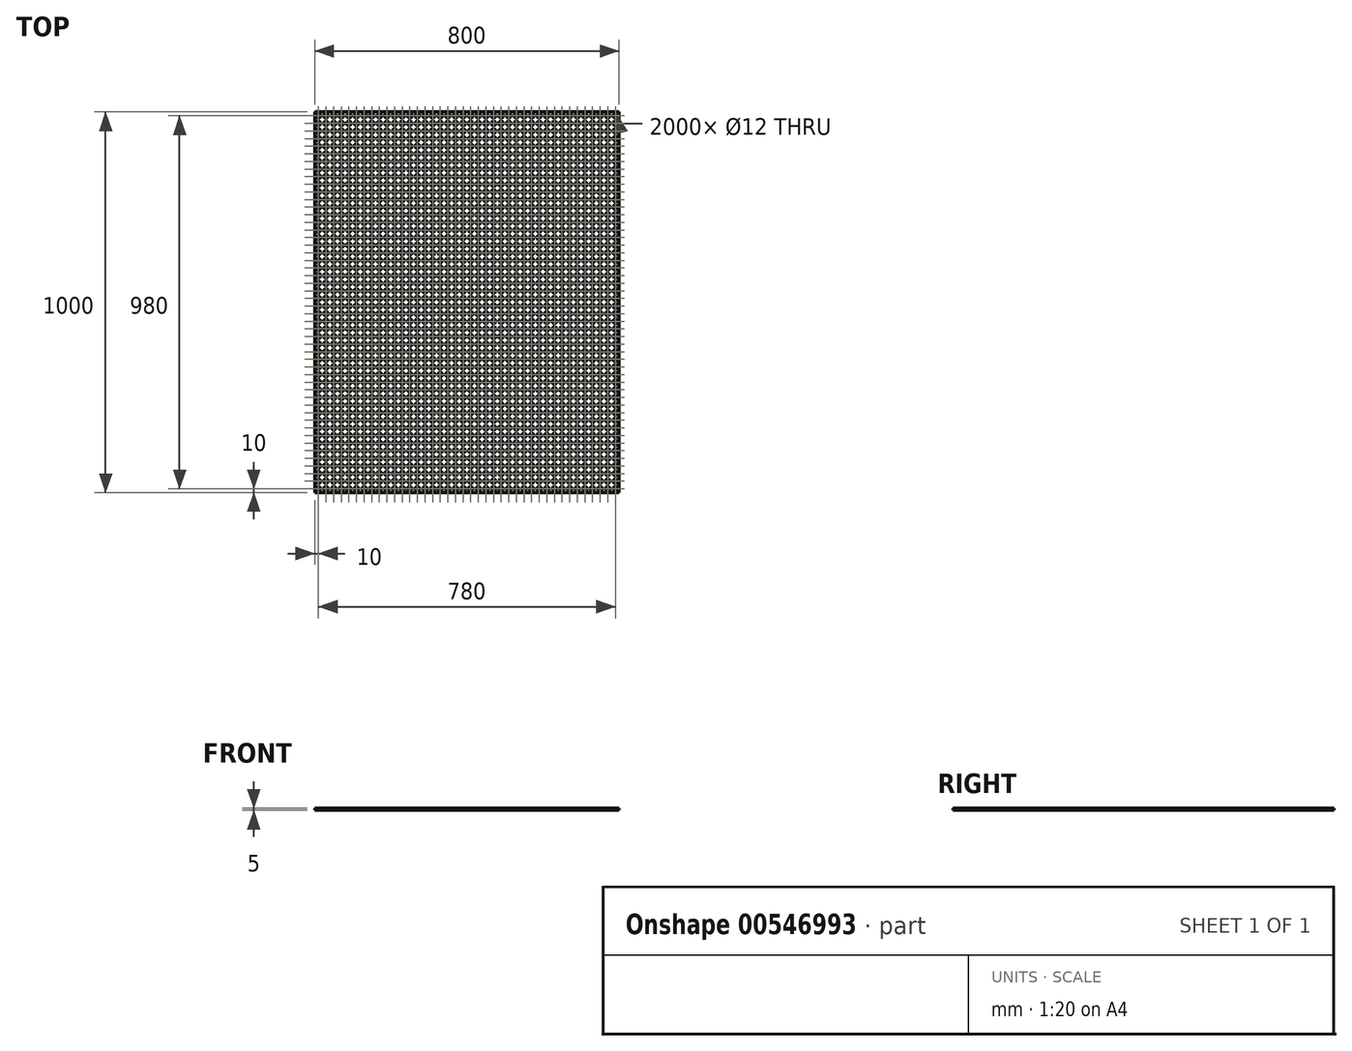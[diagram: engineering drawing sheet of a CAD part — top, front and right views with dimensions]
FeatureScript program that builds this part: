
annotation { "Feature Type Name" : "Feature", "Feature Type Description" : "" }
export const myFeature = defineFeature(function(context is Context, id is Id, definition is map)
    precondition{}
    {
        {
            var Q0;
            Q0=qCreatedBy(makeId("Top.planeOp"),FACE);
            var sketch = newSketch(context, id + "F0", { "sketchPlane" : qUnion([Q0])});
            skLineSegment(sketch, "E0.bottom", {"start": v(-409.32, 246.6) * mm, "end": v(390.68, 246.6) * mm});
            skLineSegment(sketch, "E0.top", {"start": v(-409.32, -753.4) * mm, "end": v(390.68, -753.4) * mm});
            skLineSegment(sketch, "E0.left", {"start": v(-409.32, 246.6) * mm, "end": v(-409.32, -753.4) * mm});
            skLineSegment(sketch, "E0.right", {"start": v(390.68, 246.6) * mm, "end": v(390.68, -753.4) * mm});
            skSolve(sketch);
        }
        {
            var Q0;
            Q0=makeQuery(id+"F0.imprint","IMPRINT",FACE,{"disambiguationData":[TD([[makeQuery(id+"F0.imprint","IMPRINT",EDGE,{"derivedFrom":sQuery(id+"F0.wireOp",EDGE,"E0.bottom")}),-1.0]])]});
            extrude(context, id + "F1", {"entities" : qUnion([Q0]), "depth" : 5 * mm, "offsetDistance" : 25 * mm});
        }
        {
            var Q0;
            Q0=makeQuery(id+"F1.opExtrude","CAP_FACE",FACE,{"disambiguationData":[OSD([sQuery(id+"F0.wireOp",EDGE,"E0.bottom"),sQuery(id+"F0.wireOp",EDGE,"E0.top"),sQuery(id+"F0.wireOp",EDGE,"E0.left"),sQuery(id+"F0.wireOp",EDGE,"E0.right")])],"isStart":false});
            var sketch = newSketch(context, id + "F2", { "sketchPlane" : qUnion([Q0])});
            skCircle(sketch, "E1", {"center": v(-399.32, 236.6) * mm, "radius": 6 * mm});
            skCircle(sketch, "E2.0.1.0", {"center": v(-399.32, 216.6) * mm, "radius": 6 * mm});
            skCircle(sketch, "E2.0.2.0", {"center": v(-399.32, 196.6) * mm, "radius": 6 * mm});
            skCircle(sketch, "E2.0.3.0", {"center": v(-399.32, 176.6) * mm, "radius": 6 * mm});
            skCircle(sketch, "E2.0.4.0", {"center": v(-399.32, 156.6) * mm, "radius": 6 * mm});
            skCircle(sketch, "E2.0.5.0", {"center": v(-399.32, 136.6) * mm, "radius": 6 * mm});
            skCircle(sketch, "E2.0.6.0", {"center": v(-399.32, 116.6) * mm, "radius": 6 * mm});
            skCircle(sketch, "E2.0.7.0", {"center": v(-399.32, 96.6) * mm, "radius": 6 * mm});
            skCircle(sketch, "E2.0.8.0", {"center": v(-399.32, 76.6) * mm, "radius": 6 * mm});
            skCircle(sketch, "E2.0.9.0", {"center": v(-399.32, 56.6) * mm, "radius": 6 * mm});
            skCircle(sketch, "E2.0.10.0", {"center": v(-399.32, 36.6) * mm, "radius": 6 * mm});
            skCircle(sketch, "E2.0.11.0", {"center": v(-399.32, 16.6) * mm, "radius": 6 * mm});
            skCircle(sketch, "E2.0.12.0", {"center": v(-399.32, -3.4) * mm, "radius": 6 * mm});
            skCircle(sketch, "E2.0.13.0", {"center": v(-399.32, -23.4) * mm, "radius": 6 * mm});
            skCircle(sketch, "E2.0.14.0", {"center": v(-399.32, -43.4) * mm, "radius": 6 * mm});
            skCircle(sketch, "E2.0.15.0", {"center": v(-399.32, -63.4) * mm, "radius": 6 * mm});
            skCircle(sketch, "E2.0.16.0", {"center": v(-399.32, -83.4) * mm, "radius": 6 * mm});
            skCircle(sketch, "E2.0.17.0", {"center": v(-399.32, -103.4) * mm, "radius": 6 * mm});
            skCircle(sketch, "E2.0.18.0", {"center": v(-399.32, -123.4) * mm, "radius": 6 * mm});
            skCircle(sketch, "E2.0.19.0", {"center": v(-399.32, -143.4) * mm, "radius": 6 * mm});
            skCircle(sketch, "E2.0.20.0", {"center": v(-399.32, -163.4) * mm, "radius": 6 * mm});
            skCircle(sketch, "E2.0.21.0", {"center": v(-399.32, -183.4) * mm, "radius": 6 * mm});
            skCircle(sketch, "E2.0.22.0", {"center": v(-399.32, -203.4) * mm, "radius": 6 * mm});
            skCircle(sketch, "E2.0.23.0", {"center": v(-399.32, -223.4) * mm, "radius": 6 * mm});
            skCircle(sketch, "E2.0.24.0", {"center": v(-399.32, -243.4) * mm, "radius": 6 * mm});
            skCircle(sketch, "E2.0.25.0", {"center": v(-399.32, -263.4) * mm, "radius": 6 * mm});
            skCircle(sketch, "E2.0.26.0", {"center": v(-399.32, -283.4) * mm, "radius": 6 * mm});
            skCircle(sketch, "E2.0.27.0", {"center": v(-399.32, -303.4) * mm, "radius": 6 * mm});
            skCircle(sketch, "E2.0.28.0", {"center": v(-399.32, -323.4) * mm, "radius": 6 * mm});
            skCircle(sketch, "E2.0.29.0", {"center": v(-399.32, -343.4) * mm, "radius": 6 * mm});
            skCircle(sketch, "E2.0.30.0", {"center": v(-399.32, -363.4) * mm, "radius": 6 * mm});
            skCircle(sketch, "E2.0.31.0", {"center": v(-399.32, -383.4) * mm, "radius": 6 * mm});
            skCircle(sketch, "E2.0.32.0", {"center": v(-399.32, -403.4) * mm, "radius": 6 * mm});
            skCircle(sketch, "E2.0.33.0", {"center": v(-399.32, -423.4) * mm, "radius": 6 * mm});
            skCircle(sketch, "E2.0.34.0", {"center": v(-399.32, -443.4) * mm, "radius": 6 * mm});
            skCircle(sketch, "E2.0.35.0", {"center": v(-399.32, -463.4) * mm, "radius": 6 * mm});
            skCircle(sketch, "E2.0.36.0", {"center": v(-399.32, -483.4) * mm, "radius": 6 * mm});
            skCircle(sketch, "E2.0.37.0", {"center": v(-399.32, -503.4) * mm, "radius": 6 * mm});
            skCircle(sketch, "E2.0.38.0", {"center": v(-399.32, -523.4) * mm, "radius": 6 * mm});
            skCircle(sketch, "E2.0.39.0", {"center": v(-399.32, -543.4) * mm, "radius": 6 * mm});
            skCircle(sketch, "E2.0.40.0", {"center": v(-399.32, -563.4) * mm, "radius": 6 * mm});
            skCircle(sketch, "E2.0.41.0", {"center": v(-399.32, -583.4) * mm, "radius": 6 * mm});
            skCircle(sketch, "E2.0.42.0", {"center": v(-399.32, -603.4) * mm, "radius": 6 * mm});
            skCircle(sketch, "E2.0.43.0", {"center": v(-399.32, -623.4) * mm, "radius": 6 * mm});
            skCircle(sketch, "E2.0.44.0", {"center": v(-399.32, -643.4) * mm, "radius": 6 * mm});
            skCircle(sketch, "E2.0.45.0", {"center": v(-399.32, -663.4) * mm, "radius": 6 * mm});
            skCircle(sketch, "E2.0.46.0", {"center": v(-399.32, -683.4) * mm, "radius": 6 * mm});
            skCircle(sketch, "E2.0.47.0", {"center": v(-399.32, -703.4) * mm, "radius": 6 * mm});
            skCircle(sketch, "E2.0.48.0", {"center": v(-399.32, -723.4) * mm, "radius": 6 * mm});
            skCircle(sketch, "E2.0.49.0", {"center": v(-399.32, -743.4) * mm, "radius": 6 * mm});
            skCircle(sketch, "E2.1.0.0", {"center": v(-379.32, 236.6) * mm, "radius": 6 * mm});
            skCircle(sketch, "E2.1.1.0", {"center": v(-379.32, 216.6) * mm, "radius": 6 * mm});
            skCircle(sketch, "E2.1.2.0", {"center": v(-379.32, 196.6) * mm, "radius": 6 * mm});
            skCircle(sketch, "E2.1.3.0", {"center": v(-379.32, 176.6) * mm, "radius": 6 * mm});
            skCircle(sketch, "E2.1.4.0", {"center": v(-379.32, 156.6) * mm, "radius": 6 * mm});
            skCircle(sketch, "E2.1.5.0", {"center": v(-379.32, 136.6) * mm, "radius": 6 * mm});
            skCircle(sketch, "E2.1.6.0", {"center": v(-379.32, 116.6) * mm, "radius": 6 * mm});
            skCircle(sketch, "E2.1.7.0", {"center": v(-379.32, 96.6) * mm, "radius": 6 * mm});
            skCircle(sketch, "E2.1.8.0", {"center": v(-379.32, 76.6) * mm, "radius": 6 * mm});
            skCircle(sketch, "E2.1.9.0", {"center": v(-379.32, 56.6) * mm, "radius": 6 * mm});
            skCircle(sketch, "E2.1.10.0", {"center": v(-379.32, 36.6) * mm, "radius": 6 * mm});
            skCircle(sketch, "E2.1.11.0", {"center": v(-379.32, 16.6) * mm, "radius": 6 * mm});
            skCircle(sketch, "E2.1.12.0", {"center": v(-379.32, -3.4) * mm, "radius": 6 * mm});
            skCircle(sketch, "E2.1.13.0", {"center": v(-379.32, -23.4) * mm, "radius": 6 * mm});
            skCircle(sketch, "E2.1.14.0", {"center": v(-379.32, -43.4) * mm, "radius": 6 * mm});
            skCircle(sketch, "E2.1.15.0", {"center": v(-379.32, -63.4) * mm, "radius": 6 * mm});
            skCircle(sketch, "E2.1.16.0", {"center": v(-379.32, -83.4) * mm, "radius": 6 * mm});
            skCircle(sketch, "E2.1.17.0", {"center": v(-379.32, -103.4) * mm, "radius": 6 * mm});
            skCircle(sketch, "E2.1.18.0", {"center": v(-379.32, -123.4) * mm, "radius": 6 * mm});
            skCircle(sketch, "E2.1.19.0", {"center": v(-379.32, -143.4) * mm, "radius": 6 * mm});
            skCircle(sketch, "E2.1.20.0", {"center": v(-379.32, -163.4) * mm, "radius": 6 * mm});
            skCircle(sketch, "E2.1.21.0", {"center": v(-379.32, -183.4) * mm, "radius": 6 * mm});
            skCircle(sketch, "E2.1.22.0", {"center": v(-379.32, -203.4) * mm, "radius": 6 * mm});
            skCircle(sketch, "E2.1.23.0", {"center": v(-379.32, -223.4) * mm, "radius": 6 * mm});
            skCircle(sketch, "E2.1.24.0", {"center": v(-379.32, -243.4) * mm, "radius": 6 * mm});
            skCircle(sketch, "E2.1.25.0", {"center": v(-379.32, -263.4) * mm, "radius": 6 * mm});
            skCircle(sketch, "E2.1.26.0", {"center": v(-379.32, -283.4) * mm, "radius": 6 * mm});
            skCircle(sketch, "E2.1.27.0", {"center": v(-379.32, -303.4) * mm, "radius": 6 * mm});
            skCircle(sketch, "E2.1.28.0", {"center": v(-379.32, -323.4) * mm, "radius": 6 * mm});
            skCircle(sketch, "E2.1.29.0", {"center": v(-379.32, -343.4) * mm, "radius": 6 * mm});
            skCircle(sketch, "E2.1.30.0", {"center": v(-379.32, -363.4) * mm, "radius": 6 * mm});
            skCircle(sketch, "E2.1.31.0", {"center": v(-379.32, -383.4) * mm, "radius": 6 * mm});
            skCircle(sketch, "E2.1.32.0", {"center": v(-379.32, -403.4) * mm, "radius": 6 * mm});
            skCircle(sketch, "E2.1.33.0", {"center": v(-379.32, -423.4) * mm, "radius": 6 * mm});
            skCircle(sketch, "E2.1.34.0", {"center": v(-379.32, -443.4) * mm, "radius": 6 * mm});
            skCircle(sketch, "E2.1.35.0", {"center": v(-379.32, -463.4) * mm, "radius": 6 * mm});
            skCircle(sketch, "E2.1.36.0", {"center": v(-379.32, -483.4) * mm, "radius": 6 * mm});
            skCircle(sketch, "E2.1.37.0", {"center": v(-379.32, -503.4) * mm, "radius": 6 * mm});
            skCircle(sketch, "E2.1.38.0", {"center": v(-379.32, -523.4) * mm, "radius": 6 * mm});
            skCircle(sketch, "E2.1.39.0", {"center": v(-379.32, -543.4) * mm, "radius": 6 * mm});
            skCircle(sketch, "E2.1.40.0", {"center": v(-379.32, -563.4) * mm, "radius": 6 * mm});
            skCircle(sketch, "E2.1.41.0", {"center": v(-379.32, -583.4) * mm, "radius": 6 * mm});
            skCircle(sketch, "E2.1.42.0", {"center": v(-379.32, -603.4) * mm, "radius": 6 * mm});
            skCircle(sketch, "E2.1.43.0", {"center": v(-379.32, -623.4) * mm, "radius": 6 * mm});
            skCircle(sketch, "E2.1.44.0", {"center": v(-379.32, -643.4) * mm, "radius": 6 * mm});
            skCircle(sketch, "E2.1.45.0", {"center": v(-379.32, -663.4) * mm, "radius": 6 * mm});
            skCircle(sketch, "E2.1.46.0", {"center": v(-379.32, -683.4) * mm, "radius": 6 * mm});
            skCircle(sketch, "E2.1.47.0", {"center": v(-379.32, -703.4) * mm, "radius": 6 * mm});
            skCircle(sketch, "E2.1.48.0", {"center": v(-379.32, -723.4) * mm, "radius": 6 * mm});
            skCircle(sketch, "E2.1.49.0", {"center": v(-379.32, -743.4) * mm, "radius": 6 * mm});
            skCircle(sketch, "E2.2.0.0", {"center": v(-359.32, 236.6) * mm, "radius": 6 * mm});
            skCircle(sketch, "E2.2.1.0", {"center": v(-359.32, 216.6) * mm, "radius": 6 * mm});
            skCircle(sketch, "E2.2.2.0", {"center": v(-359.32, 196.6) * mm, "radius": 6 * mm});
            skCircle(sketch, "E2.2.3.0", {"center": v(-359.32, 176.6) * mm, "radius": 6 * mm});
            skCircle(sketch, "E2.2.4.0", {"center": v(-359.32, 156.6) * mm, "radius": 6 * mm});
            skCircle(sketch, "E2.2.5.0", {"center": v(-359.32, 136.6) * mm, "radius": 6 * mm});
            skCircle(sketch, "E2.2.6.0", {"center": v(-359.32, 116.6) * mm, "radius": 6 * mm});
            skCircle(sketch, "E2.2.7.0", {"center": v(-359.32, 96.6) * mm, "radius": 6 * mm});
            skCircle(sketch, "E2.2.8.0", {"center": v(-359.32, 76.6) * mm, "radius": 6 * mm});
            skCircle(sketch, "E2.2.9.0", {"center": v(-359.32, 56.6) * mm, "radius": 6 * mm});
            skCircle(sketch, "E2.2.10.0", {"center": v(-359.32, 36.6) * mm, "radius": 6 * mm});
            skCircle(sketch, "E2.2.11.0", {"center": v(-359.32, 16.6) * mm, "radius": 6 * mm});
            skCircle(sketch, "E2.2.12.0", {"center": v(-359.32, -3.4) * mm, "radius": 6 * mm});
            skCircle(sketch, "E2.2.13.0", {"center": v(-359.32, -23.4) * mm, "radius": 6 * mm});
            skCircle(sketch, "E2.2.14.0", {"center": v(-359.32, -43.4) * mm, "radius": 6 * mm});
            skCircle(sketch, "E2.2.15.0", {"center": v(-359.32, -63.4) * mm, "radius": 6 * mm});
            skCircle(sketch, "E2.2.16.0", {"center": v(-359.32, -83.4) * mm, "radius": 6 * mm});
            skCircle(sketch, "E2.2.17.0", {"center": v(-359.32, -103.4) * mm, "radius": 6 * mm});
            skCircle(sketch, "E2.2.18.0", {"center": v(-359.32, -123.4) * mm, "radius": 6 * mm});
            skCircle(sketch, "E2.2.19.0", {"center": v(-359.32, -143.4) * mm, "radius": 6 * mm});
            skCircle(sketch, "E2.2.20.0", {"center": v(-359.32, -163.4) * mm, "radius": 6 * mm});
            skCircle(sketch, "E2.2.21.0", {"center": v(-359.32, -183.4) * mm, "radius": 6 * mm});
            skCircle(sketch, "E2.2.22.0", {"center": v(-359.32, -203.4) * mm, "radius": 6 * mm});
            skCircle(sketch, "E2.2.23.0", {"center": v(-359.32, -223.4) * mm, "radius": 6 * mm});
            skCircle(sketch, "E2.2.24.0", {"center": v(-359.32, -243.4) * mm, "radius": 6 * mm});
            skCircle(sketch, "E2.2.25.0", {"center": v(-359.32, -263.4) * mm, "radius": 6 * mm});
            skCircle(sketch, "E2.2.26.0", {"center": v(-359.32, -283.4) * mm, "radius": 6 * mm});
            skCircle(sketch, "E2.2.27.0", {"center": v(-359.32, -303.4) * mm, "radius": 6 * mm});
            skCircle(sketch, "E2.2.28.0", {"center": v(-359.32, -323.4) * mm, "radius": 6 * mm});
            skCircle(sketch, "E2.2.29.0", {"center": v(-359.32, -343.4) * mm, "radius": 6 * mm});
            skCircle(sketch, "E2.2.30.0", {"center": v(-359.32, -363.4) * mm, "radius": 6 * mm});
            skCircle(sketch, "E2.2.31.0", {"center": v(-359.32, -383.4) * mm, "radius": 6 * mm});
            skCircle(sketch, "E2.2.32.0", {"center": v(-359.32, -403.4) * mm, "radius": 6 * mm});
            skCircle(sketch, "E2.2.33.0", {"center": v(-359.32, -423.4) * mm, "radius": 6 * mm});
            skCircle(sketch, "E2.2.34.0", {"center": v(-359.32, -443.4) * mm, "radius": 6 * mm});
            skCircle(sketch, "E2.2.35.0", {"center": v(-359.32, -463.4) * mm, "radius": 6 * mm});
            skCircle(sketch, "E2.2.36.0", {"center": v(-359.32, -483.4) * mm, "radius": 6 * mm});
            skCircle(sketch, "E2.2.37.0", {"center": v(-359.32, -503.4) * mm, "radius": 6 * mm});
            skCircle(sketch, "E2.2.38.0", {"center": v(-359.32, -523.4) * mm, "radius": 6 * mm});
            skCircle(sketch, "E2.2.39.0", {"center": v(-359.32, -543.4) * mm, "radius": 6 * mm});
            skCircle(sketch, "E2.2.40.0", {"center": v(-359.32, -563.4) * mm, "radius": 6 * mm});
            skCircle(sketch, "E2.2.41.0", {"center": v(-359.32, -583.4) * mm, "radius": 6 * mm});
            skCircle(sketch, "E2.2.42.0", {"center": v(-359.32, -603.4) * mm, "radius": 6 * mm});
            skCircle(sketch, "E2.2.43.0", {"center": v(-359.32, -623.4) * mm, "radius": 6 * mm});
            skCircle(sketch, "E2.2.44.0", {"center": v(-359.32, -643.4) * mm, "radius": 6 * mm});
            skCircle(sketch, "E2.2.45.0", {"center": v(-359.32, -663.4) * mm, "radius": 6 * mm});
            skCircle(sketch, "E2.2.46.0", {"center": v(-359.32, -683.4) * mm, "radius": 6 * mm});
            skCircle(sketch, "E2.2.47.0", {"center": v(-359.32, -703.4) * mm, "radius": 6 * mm});
            skCircle(sketch, "E2.2.48.0", {"center": v(-359.32, -723.4) * mm, "radius": 6 * mm});
            skCircle(sketch, "E2.2.49.0", {"center": v(-359.32, -743.4) * mm, "radius": 6 * mm});
            skCircle(sketch, "E2.3.0.0", {"center": v(-339.32, 236.6) * mm, "radius": 6 * mm});
            skCircle(sketch, "E2.3.1.0", {"center": v(-339.32, 216.6) * mm, "radius": 6 * mm});
            skCircle(sketch, "E2.3.2.0", {"center": v(-339.32, 196.6) * mm, "radius": 6 * mm});
            skCircle(sketch, "E2.3.3.0", {"center": v(-339.32, 176.6) * mm, "radius": 6 * mm});
            skCircle(sketch, "E2.3.4.0", {"center": v(-339.32, 156.6) * mm, "radius": 6 * mm});
            skCircle(sketch, "E2.3.5.0", {"center": v(-339.32, 136.6) * mm, "radius": 6 * mm});
            skCircle(sketch, "E2.3.6.0", {"center": v(-339.32, 116.6) * mm, "radius": 6 * mm});
            skCircle(sketch, "E2.3.7.0", {"center": v(-339.32, 96.6) * mm, "radius": 6 * mm});
            skCircle(sketch, "E2.3.8.0", {"center": v(-339.32, 76.6) * mm, "radius": 6 * mm});
            skCircle(sketch, "E2.3.9.0", {"center": v(-339.32, 56.6) * mm, "radius": 6 * mm});
            skCircle(sketch, "E2.3.10.0", {"center": v(-339.32, 36.6) * mm, "radius": 6 * mm});
            skCircle(sketch, "E2.3.11.0", {"center": v(-339.32, 16.6) * mm, "radius": 6 * mm});
            skCircle(sketch, "E2.3.12.0", {"center": v(-339.32, -3.4) * mm, "radius": 6 * mm});
            skCircle(sketch, "E2.3.13.0", {"center": v(-339.32, -23.4) * mm, "radius": 6 * mm});
            skCircle(sketch, "E2.3.14.0", {"center": v(-339.32, -43.4) * mm, "radius": 6 * mm});
            skCircle(sketch, "E2.3.15.0", {"center": v(-339.32, -63.4) * mm, "radius": 6 * mm});
            skCircle(sketch, "E2.3.16.0", {"center": v(-339.32, -83.4) * mm, "radius": 6 * mm});
            skCircle(sketch, "E2.3.17.0", {"center": v(-339.32, -103.4) * mm, "radius": 6 * mm});
            skCircle(sketch, "E2.3.18.0", {"center": v(-339.32, -123.4) * mm, "radius": 6 * mm});
            skCircle(sketch, "E2.3.19.0", {"center": v(-339.32, -143.4) * mm, "radius": 6 * mm});
            skCircle(sketch, "E2.3.20.0", {"center": v(-339.32, -163.4) * mm, "radius": 6 * mm});
            skCircle(sketch, "E2.3.21.0", {"center": v(-339.32, -183.4) * mm, "radius": 6 * mm});
            skCircle(sketch, "E2.3.22.0", {"center": v(-339.32, -203.4) * mm, "radius": 6 * mm});
            skCircle(sketch, "E2.3.23.0", {"center": v(-339.32, -223.4) * mm, "radius": 6 * mm});
            skCircle(sketch, "E2.3.24.0", {"center": v(-339.32, -243.4) * mm, "radius": 6 * mm});
            skCircle(sketch, "E2.3.25.0", {"center": v(-339.32, -263.4) * mm, "radius": 6 * mm});
            skCircle(sketch, "E2.3.26.0", {"center": v(-339.32, -283.4) * mm, "radius": 6 * mm});
            skCircle(sketch, "E2.3.27.0", {"center": v(-339.32, -303.4) * mm, "radius": 6 * mm});
            skCircle(sketch, "E2.3.28.0", {"center": v(-339.32, -323.4) * mm, "radius": 6 * mm});
            skCircle(sketch, "E2.3.29.0", {"center": v(-339.32, -343.4) * mm, "radius": 6 * mm});
            skCircle(sketch, "E2.3.30.0", {"center": v(-339.32, -363.4) * mm, "radius": 6 * mm});
            skCircle(sketch, "E2.3.31.0", {"center": v(-339.32, -383.4) * mm, "radius": 6 * mm});
            skCircle(sketch, "E2.3.32.0", {"center": v(-339.32, -403.4) * mm, "radius": 6 * mm});
            skCircle(sketch, "E2.3.33.0", {"center": v(-339.32, -423.4) * mm, "radius": 6 * mm});
            skCircle(sketch, "E2.3.34.0", {"center": v(-339.32, -443.4) * mm, "radius": 6 * mm});
            skCircle(sketch, "E2.3.35.0", {"center": v(-339.32, -463.4) * mm, "radius": 6 * mm});
            skCircle(sketch, "E2.3.36.0", {"center": v(-339.32, -483.4) * mm, "radius": 6 * mm});
            skCircle(sketch, "E2.3.37.0", {"center": v(-339.32, -503.4) * mm, "radius": 6 * mm});
            skCircle(sketch, "E2.3.38.0", {"center": v(-339.32, -523.4) * mm, "radius": 6 * mm});
            skCircle(sketch, "E2.3.39.0", {"center": v(-339.32, -543.4) * mm, "radius": 6 * mm});
            skCircle(sketch, "E2.3.40.0", {"center": v(-339.32, -563.4) * mm, "radius": 6 * mm});
            skCircle(sketch, "E2.3.41.0", {"center": v(-339.32, -583.4) * mm, "radius": 6 * mm});
            skCircle(sketch, "E2.3.42.0", {"center": v(-339.32, -603.4) * mm, "radius": 6 * mm});
            skCircle(sketch, "E2.3.43.0", {"center": v(-339.32, -623.4) * mm, "radius": 6 * mm});
            skCircle(sketch, "E2.3.44.0", {"center": v(-339.32, -643.4) * mm, "radius": 6 * mm});
            skCircle(sketch, "E2.3.45.0", {"center": v(-339.32, -663.4) * mm, "radius": 6 * mm});
            skCircle(sketch, "E2.3.46.0", {"center": v(-339.32, -683.4) * mm, "radius": 6 * mm});
            skCircle(sketch, "E2.3.47.0", {"center": v(-339.32, -703.4) * mm, "radius": 6 * mm});
            skCircle(sketch, "E2.3.48.0", {"center": v(-339.32, -723.4) * mm, "radius": 6 * mm});
            skCircle(sketch, "E2.3.49.0", {"center": v(-339.32, -743.4) * mm, "radius": 6 * mm});
            skCircle(sketch, "E2.4.0.0", {"center": v(-319.32, 236.6) * mm, "radius": 6 * mm});
            skCircle(sketch, "E2.4.1.0", {"center": v(-319.32, 216.6) * mm, "radius": 6 * mm});
            skCircle(sketch, "E2.4.2.0", {"center": v(-319.32, 196.6) * mm, "radius": 6 * mm});
            skCircle(sketch, "E2.4.3.0", {"center": v(-319.32, 176.6) * mm, "radius": 6 * mm});
            skCircle(sketch, "E2.4.4.0", {"center": v(-319.32, 156.6) * mm, "radius": 6 * mm});
            skCircle(sketch, "E2.4.5.0", {"center": v(-319.32, 136.6) * mm, "radius": 6 * mm});
            skCircle(sketch, "E2.4.6.0", {"center": v(-319.32, 116.6) * mm, "radius": 6 * mm});
            skCircle(sketch, "E2.4.7.0", {"center": v(-319.32, 96.6) * mm, "radius": 6 * mm});
            skCircle(sketch, "E2.4.8.0", {"center": v(-319.32, 76.6) * mm, "radius": 6 * mm});
            skCircle(sketch, "E2.4.9.0", {"center": v(-319.32, 56.6) * mm, "radius": 6 * mm});
            skCircle(sketch, "E2.4.10.0", {"center": v(-319.32, 36.6) * mm, "radius": 6 * mm});
            skCircle(sketch, "E2.4.11.0", {"center": v(-319.32, 16.6) * mm, "radius": 6 * mm});
            skCircle(sketch, "E2.4.12.0", {"center": v(-319.32, -3.4) * mm, "radius": 6 * mm});
            skCircle(sketch, "E2.4.13.0", {"center": v(-319.32, -23.4) * mm, "radius": 6 * mm});
            skCircle(sketch, "E2.4.14.0", {"center": v(-319.32, -43.4) * mm, "radius": 6 * mm});
            skCircle(sketch, "E2.4.15.0", {"center": v(-319.32, -63.4) * mm, "radius": 6 * mm});
            skCircle(sketch, "E2.4.16.0", {"center": v(-319.32, -83.4) * mm, "radius": 6 * mm});
            skCircle(sketch, "E2.4.17.0", {"center": v(-319.32, -103.4) * mm, "radius": 6 * mm});
            skCircle(sketch, "E2.4.18.0", {"center": v(-319.32, -123.4) * mm, "radius": 6 * mm});
            skCircle(sketch, "E2.4.19.0", {"center": v(-319.32, -143.4) * mm, "radius": 6 * mm});
            skCircle(sketch, "E2.4.20.0", {"center": v(-319.32, -163.4) * mm, "radius": 6 * mm});
            skCircle(sketch, "E2.4.21.0", {"center": v(-319.32, -183.4) * mm, "radius": 6 * mm});
            skCircle(sketch, "E2.4.22.0", {"center": v(-319.32, -203.4) * mm, "radius": 6 * mm});
            skCircle(sketch, "E2.4.23.0", {"center": v(-319.32, -223.4) * mm, "radius": 6 * mm});
            skCircle(sketch, "E2.4.24.0", {"center": v(-319.32, -243.4) * mm, "radius": 6 * mm});
            skCircle(sketch, "E2.4.25.0", {"center": v(-319.32, -263.4) * mm, "radius": 6 * mm});
            skCircle(sketch, "E2.4.26.0", {"center": v(-319.32, -283.4) * mm, "radius": 6 * mm});
            skCircle(sketch, "E2.4.27.0", {"center": v(-319.32, -303.4) * mm, "radius": 6 * mm});
            skCircle(sketch, "E2.4.28.0", {"center": v(-319.32, -323.4) * mm, "radius": 6 * mm});
            skCircle(sketch, "E2.4.29.0", {"center": v(-319.32, -343.4) * mm, "radius": 6 * mm});
            skCircle(sketch, "E2.4.30.0", {"center": v(-319.32, -363.4) * mm, "radius": 6 * mm});
            skCircle(sketch, "E2.4.31.0", {"center": v(-319.32, -383.4) * mm, "radius": 6 * mm});
            skCircle(sketch, "E2.4.32.0", {"center": v(-319.32, -403.4) * mm, "radius": 6 * mm});
            skCircle(sketch, "E2.4.33.0", {"center": v(-319.32, -423.4) * mm, "radius": 6 * mm});
            skCircle(sketch, "E2.4.34.0", {"center": v(-319.32, -443.4) * mm, "radius": 6 * mm});
            skCircle(sketch, "E2.4.35.0", {"center": v(-319.32, -463.4) * mm, "radius": 6 * mm});
            skCircle(sketch, "E2.4.36.0", {"center": v(-319.32, -483.4) * mm, "radius": 6 * mm});
            skCircle(sketch, "E2.4.37.0", {"center": v(-319.32, -503.4) * mm, "radius": 6 * mm});
            skCircle(sketch, "E2.4.38.0", {"center": v(-319.32, -523.4) * mm, "radius": 6 * mm});
            skCircle(sketch, "E2.4.39.0", {"center": v(-319.32, -543.4) * mm, "radius": 6 * mm});
            skCircle(sketch, "E2.4.40.0", {"center": v(-319.32, -563.4) * mm, "radius": 6 * mm});
            skCircle(sketch, "E2.4.41.0", {"center": v(-319.32, -583.4) * mm, "radius": 6 * mm});
            skCircle(sketch, "E2.4.42.0", {"center": v(-319.32, -603.4) * mm, "radius": 6 * mm});
            skCircle(sketch, "E2.4.43.0", {"center": v(-319.32, -623.4) * mm, "radius": 6 * mm});
            skCircle(sketch, "E2.4.44.0", {"center": v(-319.32, -643.4) * mm, "radius": 6 * mm});
            skCircle(sketch, "E2.4.45.0", {"center": v(-319.32, -663.4) * mm, "radius": 6 * mm});
            skCircle(sketch, "E2.4.46.0", {"center": v(-319.32, -683.4) * mm, "radius": 6 * mm});
            skCircle(sketch, "E2.4.47.0", {"center": v(-319.32, -703.4) * mm, "radius": 6 * mm});
            skCircle(sketch, "E2.4.48.0", {"center": v(-319.32, -723.4) * mm, "radius": 6 * mm});
            skCircle(sketch, "E2.4.49.0", {"center": v(-319.32, -743.4) * mm, "radius": 6 * mm});
            skCircle(sketch, "E2.5.0.0", {"center": v(-299.32, 236.6) * mm, "radius": 6 * mm});
            skCircle(sketch, "E2.5.1.0", {"center": v(-299.32, 216.6) * mm, "radius": 6 * mm});
            skCircle(sketch, "E2.5.2.0", {"center": v(-299.32, 196.6) * mm, "radius": 6 * mm});
            skCircle(sketch, "E2.5.3.0", {"center": v(-299.32, 176.6) * mm, "radius": 6 * mm});
            skCircle(sketch, "E2.5.4.0", {"center": v(-299.32, 156.6) * mm, "radius": 6 * mm});
            skCircle(sketch, "E2.5.5.0", {"center": v(-299.32, 136.6) * mm, "radius": 6 * mm});
            skCircle(sketch, "E2.5.6.0", {"center": v(-299.32, 116.6) * mm, "radius": 6 * mm});
            skCircle(sketch, "E2.5.7.0", {"center": v(-299.32, 96.6) * mm, "radius": 6 * mm});
            skCircle(sketch, "E2.5.8.0", {"center": v(-299.32, 76.6) * mm, "radius": 6 * mm});
            skCircle(sketch, "E2.5.9.0", {"center": v(-299.32, 56.6) * mm, "radius": 6 * mm});
            skCircle(sketch, "E2.5.10.0", {"center": v(-299.32, 36.6) * mm, "radius": 6 * mm});
            skCircle(sketch, "E2.5.11.0", {"center": v(-299.32, 16.6) * mm, "radius": 6 * mm});
            skCircle(sketch, "E2.5.12.0", {"center": v(-299.32, -3.4) * mm, "radius": 6 * mm});
            skCircle(sketch, "E2.5.13.0", {"center": v(-299.32, -23.4) * mm, "radius": 6 * mm});
            skCircle(sketch, "E2.5.14.0", {"center": v(-299.32, -43.4) * mm, "radius": 6 * mm});
            skCircle(sketch, "E2.5.15.0", {"center": v(-299.32, -63.4) * mm, "radius": 6 * mm});
            skCircle(sketch, "E2.5.16.0", {"center": v(-299.32, -83.4) * mm, "radius": 6 * mm});
            skCircle(sketch, "E2.5.17.0", {"center": v(-299.32, -103.4) * mm, "radius": 6 * mm});
            skCircle(sketch, "E2.5.18.0", {"center": v(-299.32, -123.4) * mm, "radius": 6 * mm});
            skCircle(sketch, "E2.5.19.0", {"center": v(-299.32, -143.4) * mm, "radius": 6 * mm});
            skCircle(sketch, "E2.5.20.0", {"center": v(-299.32, -163.4) * mm, "radius": 6 * mm});
            skCircle(sketch, "E2.5.21.0", {"center": v(-299.32, -183.4) * mm, "radius": 6 * mm});
            skCircle(sketch, "E2.5.22.0", {"center": v(-299.32, -203.4) * mm, "radius": 6 * mm});
            skCircle(sketch, "E2.5.23.0", {"center": v(-299.32, -223.4) * mm, "radius": 6 * mm});
            skCircle(sketch, "E2.5.24.0", {"center": v(-299.32, -243.4) * mm, "radius": 6 * mm});
            skCircle(sketch, "E2.5.25.0", {"center": v(-299.32, -263.4) * mm, "radius": 6 * mm});
            skCircle(sketch, "E2.5.26.0", {"center": v(-299.32, -283.4) * mm, "radius": 6 * mm});
            skCircle(sketch, "E2.5.27.0", {"center": v(-299.32, -303.4) * mm, "radius": 6 * mm});
            skCircle(sketch, "E2.5.28.0", {"center": v(-299.32, -323.4) * mm, "radius": 6 * mm});
            skCircle(sketch, "E2.5.29.0", {"center": v(-299.32, -343.4) * mm, "radius": 6 * mm});
            skCircle(sketch, "E2.5.30.0", {"center": v(-299.32, -363.4) * mm, "radius": 6 * mm});
            skCircle(sketch, "E2.5.31.0", {"center": v(-299.32, -383.4) * mm, "radius": 6 * mm});
            skCircle(sketch, "E2.5.32.0", {"center": v(-299.32, -403.4) * mm, "radius": 6 * mm});
            skCircle(sketch, "E2.5.33.0", {"center": v(-299.32, -423.4) * mm, "radius": 6 * mm});
            skCircle(sketch, "E2.5.34.0", {"center": v(-299.32, -443.4) * mm, "radius": 6 * mm});
            skCircle(sketch, "E2.5.35.0", {"center": v(-299.32, -463.4) * mm, "radius": 6 * mm});
            skCircle(sketch, "E2.5.36.0", {"center": v(-299.32, -483.4) * mm, "radius": 6 * mm});
            skCircle(sketch, "E2.5.37.0", {"center": v(-299.32, -503.4) * mm, "radius": 6 * mm});
            skCircle(sketch, "E2.5.38.0", {"center": v(-299.32, -523.4) * mm, "radius": 6 * mm});
            skCircle(sketch, "E2.5.39.0", {"center": v(-299.32, -543.4) * mm, "radius": 6 * mm});
            skCircle(sketch, "E2.5.40.0", {"center": v(-299.32, -563.4) * mm, "radius": 6 * mm});
            skCircle(sketch, "E2.5.41.0", {"center": v(-299.32, -583.4) * mm, "radius": 6 * mm});
            skCircle(sketch, "E2.5.42.0", {"center": v(-299.32, -603.4) * mm, "radius": 6 * mm});
            skCircle(sketch, "E2.5.43.0", {"center": v(-299.32, -623.4) * mm, "radius": 6 * mm});
            skCircle(sketch, "E2.5.44.0", {"center": v(-299.32, -643.4) * mm, "radius": 6 * mm});
            skCircle(sketch, "E2.5.45.0", {"center": v(-299.32, -663.4) * mm, "radius": 6 * mm});
            skCircle(sketch, "E2.5.46.0", {"center": v(-299.32, -683.4) * mm, "radius": 6 * mm});
            skCircle(sketch, "E2.5.47.0", {"center": v(-299.32, -703.4) * mm, "radius": 6 * mm});
            skCircle(sketch, "E2.5.48.0", {"center": v(-299.32, -723.4) * mm, "radius": 6 * mm});
            skCircle(sketch, "E2.5.49.0", {"center": v(-299.32, -743.4) * mm, "radius": 6 * mm});
            skCircle(sketch, "E2.6.0.0", {"center": v(-279.32, 236.6) * mm, "radius": 6 * mm});
            skCircle(sketch, "E2.6.1.0", {"center": v(-279.32, 216.6) * mm, "radius": 6 * mm});
            skCircle(sketch, "E2.6.2.0", {"center": v(-279.32, 196.6) * mm, "radius": 6 * mm});
            skCircle(sketch, "E2.6.3.0", {"center": v(-279.32, 176.6) * mm, "radius": 6 * mm});
            skCircle(sketch, "E2.6.4.0", {"center": v(-279.32, 156.6) * mm, "radius": 6 * mm});
            skCircle(sketch, "E2.6.5.0", {"center": v(-279.32, 136.6) * mm, "radius": 6 * mm});
            skCircle(sketch, "E2.6.6.0", {"center": v(-279.32, 116.6) * mm, "radius": 6 * mm});
            skCircle(sketch, "E2.6.7.0", {"center": v(-279.32, 96.6) * mm, "radius": 6 * mm});
            skCircle(sketch, "E2.6.8.0", {"center": v(-279.32, 76.6) * mm, "radius": 6 * mm});
            skCircle(sketch, "E2.6.9.0", {"center": v(-279.32, 56.6) * mm, "radius": 6 * mm});
            skCircle(sketch, "E2.6.10.0", {"center": v(-279.32, 36.6) * mm, "radius": 6 * mm});
            skCircle(sketch, "E2.6.11.0", {"center": v(-279.32, 16.6) * mm, "radius": 6 * mm});
            skCircle(sketch, "E2.6.12.0", {"center": v(-279.32, -3.4) * mm, "radius": 6 * mm});
            skCircle(sketch, "E2.6.13.0", {"center": v(-279.32, -23.4) * mm, "radius": 6 * mm});
            skCircle(sketch, "E2.6.14.0", {"center": v(-279.32, -43.4) * mm, "radius": 6 * mm});
            skCircle(sketch, "E2.6.15.0", {"center": v(-279.32, -63.4) * mm, "radius": 6 * mm});
            skCircle(sketch, "E2.6.16.0", {"center": v(-279.32, -83.4) * mm, "radius": 6 * mm});
            skCircle(sketch, "E2.6.17.0", {"center": v(-279.32, -103.4) * mm, "radius": 6 * mm});
            skCircle(sketch, "E2.6.18.0", {"center": v(-279.32, -123.4) * mm, "radius": 6 * mm});
            skCircle(sketch, "E2.6.19.0", {"center": v(-279.32, -143.4) * mm, "radius": 6 * mm});
            skCircle(sketch, "E2.6.20.0", {"center": v(-279.32, -163.4) * mm, "radius": 6 * mm});
            skCircle(sketch, "E2.6.21.0", {"center": v(-279.32, -183.4) * mm, "radius": 6 * mm});
            skCircle(sketch, "E2.6.22.0", {"center": v(-279.32, -203.4) * mm, "radius": 6 * mm});
            skCircle(sketch, "E2.6.23.0", {"center": v(-279.32, -223.4) * mm, "radius": 6 * mm});
            skCircle(sketch, "E2.6.24.0", {"center": v(-279.32, -243.4) * mm, "radius": 6 * mm});
            skCircle(sketch, "E2.6.25.0", {"center": v(-279.32, -263.4) * mm, "radius": 6 * mm});
            skCircle(sketch, "E2.6.26.0", {"center": v(-279.32, -283.4) * mm, "radius": 6 * mm});
            skCircle(sketch, "E2.6.27.0", {"center": v(-279.32, -303.4) * mm, "radius": 6 * mm});
            skCircle(sketch, "E2.6.28.0", {"center": v(-279.32, -323.4) * mm, "radius": 6 * mm});
            skCircle(sketch, "E2.6.29.0", {"center": v(-279.32, -343.4) * mm, "radius": 6 * mm});
            skCircle(sketch, "E2.6.30.0", {"center": v(-279.32, -363.4) * mm, "radius": 6 * mm});
            skCircle(sketch, "E2.6.31.0", {"center": v(-279.32, -383.4) * mm, "radius": 6 * mm});
            skCircle(sketch, "E2.6.32.0", {"center": v(-279.32, -403.4) * mm, "radius": 6 * mm});
            skCircle(sketch, "E2.6.33.0", {"center": v(-279.32, -423.4) * mm, "radius": 6 * mm});
            skCircle(sketch, "E2.6.34.0", {"center": v(-279.32, -443.4) * mm, "radius": 6 * mm});
            skCircle(sketch, "E2.6.35.0", {"center": v(-279.32, -463.4) * mm, "radius": 6 * mm});
            skCircle(sketch, "E2.6.36.0", {"center": v(-279.32, -483.4) * mm, "radius": 6 * mm});
            skCircle(sketch, "E2.6.37.0", {"center": v(-279.32, -503.4) * mm, "radius": 6 * mm});
            skCircle(sketch, "E2.6.38.0", {"center": v(-279.32, -523.4) * mm, "radius": 6 * mm});
            skCircle(sketch, "E2.6.39.0", {"center": v(-279.32, -543.4) * mm, "radius": 6 * mm});
            skCircle(sketch, "E2.6.40.0", {"center": v(-279.32, -563.4) * mm, "radius": 6 * mm});
            skCircle(sketch, "E2.6.41.0", {"center": v(-279.32, -583.4) * mm, "radius": 6 * mm});
            skCircle(sketch, "E2.6.42.0", {"center": v(-279.32, -603.4) * mm, "radius": 6 * mm});
            skCircle(sketch, "E2.6.43.0", {"center": v(-279.32, -623.4) * mm, "radius": 6 * mm});
            skCircle(sketch, "E2.6.44.0", {"center": v(-279.32, -643.4) * mm, "radius": 6 * mm});
            skCircle(sketch, "E2.6.45.0", {"center": v(-279.32, -663.4) * mm, "radius": 6 * mm});
            skCircle(sketch, "E2.6.46.0", {"center": v(-279.32, -683.4) * mm, "radius": 6 * mm});
            skCircle(sketch, "E2.6.47.0", {"center": v(-279.32, -703.4) * mm, "radius": 6 * mm});
            skCircle(sketch, "E2.6.48.0", {"center": v(-279.32, -723.4) * mm, "radius": 6 * mm});
            skCircle(sketch, "E2.6.49.0", {"center": v(-279.32, -743.4) * mm, "radius": 6 * mm});
            skCircle(sketch, "E2.7.0.0", {"center": v(-259.32, 236.6) * mm, "radius": 6 * mm});
            skCircle(sketch, "E2.7.1.0", {"center": v(-259.32, 216.6) * mm, "radius": 6 * mm});
            skCircle(sketch, "E2.7.2.0", {"center": v(-259.32, 196.6) * mm, "radius": 6 * mm});
            skCircle(sketch, "E2.7.3.0", {"center": v(-259.32, 176.6) * mm, "radius": 6 * mm});
            skCircle(sketch, "E2.7.4.0", {"center": v(-259.32, 156.6) * mm, "radius": 6 * mm});
            skCircle(sketch, "E2.7.5.0", {"center": v(-259.32, 136.6) * mm, "radius": 6 * mm});
            skCircle(sketch, "E2.7.6.0", {"center": v(-259.32, 116.6) * mm, "radius": 6 * mm});
            skCircle(sketch, "E2.7.7.0", {"center": v(-259.32, 96.6) * mm, "radius": 6 * mm});
            skCircle(sketch, "E2.7.8.0", {"center": v(-259.32, 76.6) * mm, "radius": 6 * mm});
            skCircle(sketch, "E2.7.9.0", {"center": v(-259.32, 56.6) * mm, "radius": 6 * mm});
            skCircle(sketch, "E2.7.10.0", {"center": v(-259.32, 36.6) * mm, "radius": 6 * mm});
            skCircle(sketch, "E2.7.11.0", {"center": v(-259.32, 16.6) * mm, "radius": 6 * mm});
            skCircle(sketch, "E2.7.12.0", {"center": v(-259.32, -3.4) * mm, "radius": 6 * mm});
            skCircle(sketch, "E2.7.13.0", {"center": v(-259.32, -23.4) * mm, "radius": 6 * mm});
            skCircle(sketch, "E2.7.14.0", {"center": v(-259.32, -43.4) * mm, "radius": 6 * mm});
            skCircle(sketch, "E2.7.15.0", {"center": v(-259.32, -63.4) * mm, "radius": 6 * mm});
            skCircle(sketch, "E2.7.16.0", {"center": v(-259.32, -83.4) * mm, "radius": 6 * mm});
            skCircle(sketch, "E2.7.17.0", {"center": v(-259.32, -103.4) * mm, "radius": 6 * mm});
            skCircle(sketch, "E2.7.18.0", {"center": v(-259.32, -123.4) * mm, "radius": 6 * mm});
            skCircle(sketch, "E2.7.19.0", {"center": v(-259.32, -143.4) * mm, "radius": 6 * mm});
            skCircle(sketch, "E2.7.20.0", {"center": v(-259.32, -163.4) * mm, "radius": 6 * mm});
            skCircle(sketch, "E2.7.21.0", {"center": v(-259.32, -183.4) * mm, "radius": 6 * mm});
            skCircle(sketch, "E2.7.22.0", {"center": v(-259.32, -203.4) * mm, "radius": 6 * mm});
            skCircle(sketch, "E2.7.23.0", {"center": v(-259.32, -223.4) * mm, "radius": 6 * mm});
            skCircle(sketch, "E2.7.24.0", {"center": v(-259.32, -243.4) * mm, "radius": 6 * mm});
            skCircle(sketch, "E2.7.25.0", {"center": v(-259.32, -263.4) * mm, "radius": 6 * mm});
            skCircle(sketch, "E2.7.26.0", {"center": v(-259.32, -283.4) * mm, "radius": 6 * mm});
            skCircle(sketch, "E2.7.27.0", {"center": v(-259.32, -303.4) * mm, "radius": 6 * mm});
            skCircle(sketch, "E2.7.28.0", {"center": v(-259.32, -323.4) * mm, "radius": 6 * mm});
            skCircle(sketch, "E2.7.29.0", {"center": v(-259.32, -343.4) * mm, "radius": 6 * mm});
            skCircle(sketch, "E2.7.30.0", {"center": v(-259.32, -363.4) * mm, "radius": 6 * mm});
            skCircle(sketch, "E2.7.31.0", {"center": v(-259.32, -383.4) * mm, "radius": 6 * mm});
            skCircle(sketch, "E2.7.32.0", {"center": v(-259.32, -403.4) * mm, "radius": 6 * mm});
            skCircle(sketch, "E2.7.33.0", {"center": v(-259.32, -423.4) * mm, "radius": 6 * mm});
            skCircle(sketch, "E2.7.34.0", {"center": v(-259.32, -443.4) * mm, "radius": 6 * mm});
            skCircle(sketch, "E2.7.35.0", {"center": v(-259.32, -463.4) * mm, "radius": 6 * mm});
            skCircle(sketch, "E2.7.36.0", {"center": v(-259.32, -483.4) * mm, "radius": 6 * mm});
            skCircle(sketch, "E2.7.37.0", {"center": v(-259.32, -503.4) * mm, "radius": 6 * mm});
            skCircle(sketch, "E2.7.38.0", {"center": v(-259.32, -523.4) * mm, "radius": 6 * mm});
            skCircle(sketch, "E2.7.39.0", {"center": v(-259.32, -543.4) * mm, "radius": 6 * mm});
            skCircle(sketch, "E2.7.40.0", {"center": v(-259.32, -563.4) * mm, "radius": 6 * mm});
            skCircle(sketch, "E2.7.41.0", {"center": v(-259.32, -583.4) * mm, "radius": 6 * mm});
            skCircle(sketch, "E2.7.42.0", {"center": v(-259.32, -603.4) * mm, "radius": 6 * mm});
            skCircle(sketch, "E2.7.43.0", {"center": v(-259.32, -623.4) * mm, "radius": 6 * mm});
            skCircle(sketch, "E2.7.44.0", {"center": v(-259.32, -643.4) * mm, "radius": 6 * mm});
            skCircle(sketch, "E2.7.45.0", {"center": v(-259.32, -663.4) * mm, "radius": 6 * mm});
            skCircle(sketch, "E2.7.46.0", {"center": v(-259.32, -683.4) * mm, "radius": 6 * mm});
            skCircle(sketch, "E2.7.47.0", {"center": v(-259.32, -703.4) * mm, "radius": 6 * mm});
            skCircle(sketch, "E2.7.48.0", {"center": v(-259.32, -723.4) * mm, "radius": 6 * mm});
            skCircle(sketch, "E2.7.49.0", {"center": v(-259.32, -743.4) * mm, "radius": 6 * mm});
            skCircle(sketch, "E2.8.0.0", {"center": v(-239.32, 236.6) * mm, "radius": 6 * mm});
            skCircle(sketch, "E2.8.1.0", {"center": v(-239.32, 216.6) * mm, "radius": 6 * mm});
            skCircle(sketch, "E2.8.2.0", {"center": v(-239.32, 196.6) * mm, "radius": 6 * mm});
            skCircle(sketch, "E2.8.3.0", {"center": v(-239.32, 176.6) * mm, "radius": 6 * mm});
            skCircle(sketch, "E2.8.4.0", {"center": v(-239.32, 156.6) * mm, "radius": 6 * mm});
            skCircle(sketch, "E2.8.5.0", {"center": v(-239.32, 136.6) * mm, "radius": 6 * mm});
            skCircle(sketch, "E2.8.6.0", {"center": v(-239.32, 116.6) * mm, "radius": 6 * mm});
            skCircle(sketch, "E2.8.7.0", {"center": v(-239.32, 96.6) * mm, "radius": 6 * mm});
            skCircle(sketch, "E2.8.8.0", {"center": v(-239.32, 76.6) * mm, "radius": 6 * mm});
            skCircle(sketch, "E2.8.9.0", {"center": v(-239.32, 56.6) * mm, "radius": 6 * mm});
            skCircle(sketch, "E2.8.10.0", {"center": v(-239.32, 36.6) * mm, "radius": 6 * mm});
            skCircle(sketch, "E2.8.11.0", {"center": v(-239.32, 16.6) * mm, "radius": 6 * mm});
            skCircle(sketch, "E2.8.12.0", {"center": v(-239.32, -3.4) * mm, "radius": 6 * mm});
            skCircle(sketch, "E2.8.13.0", {"center": v(-239.32, -23.4) * mm, "radius": 6 * mm});
            skCircle(sketch, "E2.8.14.0", {"center": v(-239.32, -43.4) * mm, "radius": 6 * mm});
            skCircle(sketch, "E2.8.15.0", {"center": v(-239.32, -63.4) * mm, "radius": 6 * mm});
            skCircle(sketch, "E2.8.16.0", {"center": v(-239.32, -83.4) * mm, "radius": 6 * mm});
            skCircle(sketch, "E2.8.17.0", {"center": v(-239.32, -103.4) * mm, "radius": 6 * mm});
            skCircle(sketch, "E2.8.18.0", {"center": v(-239.32, -123.4) * mm, "radius": 6 * mm});
            skCircle(sketch, "E2.8.19.0", {"center": v(-239.32, -143.4) * mm, "radius": 6 * mm});
            skCircle(sketch, "E2.8.20.0", {"center": v(-239.32, -163.4) * mm, "radius": 6 * mm});
            skCircle(sketch, "E2.8.21.0", {"center": v(-239.32, -183.4) * mm, "radius": 6 * mm});
            skCircle(sketch, "E2.8.22.0", {"center": v(-239.32, -203.4) * mm, "radius": 6 * mm});
            skCircle(sketch, "E2.8.23.0", {"center": v(-239.32, -223.4) * mm, "radius": 6 * mm});
            skCircle(sketch, "E2.8.24.0", {"center": v(-239.32, -243.4) * mm, "radius": 6 * mm});
            skCircle(sketch, "E2.8.25.0", {"center": v(-239.32, -263.4) * mm, "radius": 6 * mm});
            skCircle(sketch, "E2.8.26.0", {"center": v(-239.32, -283.4) * mm, "radius": 6 * mm});
            skCircle(sketch, "E2.8.27.0", {"center": v(-239.32, -303.4) * mm, "radius": 6 * mm});
            skCircle(sketch, "E2.8.28.0", {"center": v(-239.32, -323.4) * mm, "radius": 6 * mm});
            skCircle(sketch, "E2.8.29.0", {"center": v(-239.32, -343.4) * mm, "radius": 6 * mm});
            skCircle(sketch, "E2.8.30.0", {"center": v(-239.32, -363.4) * mm, "radius": 6 * mm});
            skCircle(sketch, "E2.8.31.0", {"center": v(-239.32, -383.4) * mm, "radius": 6 * mm});
            skCircle(sketch, "E2.8.32.0", {"center": v(-239.32, -403.4) * mm, "radius": 6 * mm});
            skCircle(sketch, "E2.8.33.0", {"center": v(-239.32, -423.4) * mm, "radius": 6 * mm});
            skCircle(sketch, "E2.8.34.0", {"center": v(-239.32, -443.4) * mm, "radius": 6 * mm});
            skCircle(sketch, "E2.8.35.0", {"center": v(-239.32, -463.4) * mm, "radius": 6 * mm});
            skCircle(sketch, "E2.8.36.0", {"center": v(-239.32, -483.4) * mm, "radius": 6 * mm});
            skCircle(sketch, "E2.8.37.0", {"center": v(-239.32, -503.4) * mm, "radius": 6 * mm});
            skCircle(sketch, "E2.8.38.0", {"center": v(-239.32, -523.4) * mm, "radius": 6 * mm});
            skCircle(sketch, "E2.8.39.0", {"center": v(-239.32, -543.4) * mm, "radius": 6 * mm});
            skCircle(sketch, "E2.8.40.0", {"center": v(-239.32, -563.4) * mm, "radius": 6 * mm});
            skCircle(sketch, "E2.8.41.0", {"center": v(-239.32, -583.4) * mm, "radius": 6 * mm});
            skCircle(sketch, "E2.8.42.0", {"center": v(-239.32, -603.4) * mm, "radius": 6 * mm});
            skCircle(sketch, "E2.8.43.0", {"center": v(-239.32, -623.4) * mm, "radius": 6 * mm});
            skCircle(sketch, "E2.8.44.0", {"center": v(-239.32, -643.4) * mm, "radius": 6 * mm});
            skCircle(sketch, "E2.8.45.0", {"center": v(-239.32, -663.4) * mm, "radius": 6 * mm});
            skCircle(sketch, "E2.8.46.0", {"center": v(-239.32, -683.4) * mm, "radius": 6 * mm});
            skCircle(sketch, "E2.8.47.0", {"center": v(-239.32, -703.4) * mm, "radius": 6 * mm});
            skCircle(sketch, "E2.8.48.0", {"center": v(-239.32, -723.4) * mm, "radius": 6 * mm});
            skCircle(sketch, "E2.8.49.0", {"center": v(-239.32, -743.4) * mm, "radius": 6 * mm});
            skCircle(sketch, "E2.9.0.0", {"center": v(-219.32, 236.6) * mm, "radius": 6 * mm});
            skCircle(sketch, "E2.9.1.0", {"center": v(-219.32, 216.6) * mm, "radius": 6 * mm});
            skCircle(sketch, "E2.9.2.0", {"center": v(-219.32, 196.6) * mm, "radius": 6 * mm});
            skCircle(sketch, "E2.9.3.0", {"center": v(-219.32, 176.6) * mm, "radius": 6 * mm});
            skCircle(sketch, "E2.9.4.0", {"center": v(-219.32, 156.6) * mm, "radius": 6 * mm});
            skCircle(sketch, "E2.9.5.0", {"center": v(-219.32, 136.6) * mm, "radius": 6 * mm});
            skCircle(sketch, "E2.9.6.0", {"center": v(-219.32, 116.6) * mm, "radius": 6 * mm});
            skCircle(sketch, "E2.9.7.0", {"center": v(-219.32, 96.6) * mm, "radius": 6 * mm});
            skCircle(sketch, "E2.9.8.0", {"center": v(-219.32, 76.6) * mm, "radius": 6 * mm});
            skCircle(sketch, "E2.9.9.0", {"center": v(-219.32, 56.6) * mm, "radius": 6 * mm});
            skCircle(sketch, "E2.9.10.0", {"center": v(-219.32, 36.6) * mm, "radius": 6 * mm});
            skCircle(sketch, "E2.9.11.0", {"center": v(-219.32, 16.6) * mm, "radius": 6 * mm});
            skCircle(sketch, "E2.9.12.0", {"center": v(-219.32, -3.4) * mm, "radius": 6 * mm});
            skCircle(sketch, "E2.9.13.0", {"center": v(-219.32, -23.4) * mm, "radius": 6 * mm});
            skCircle(sketch, "E2.9.14.0", {"center": v(-219.32, -43.4) * mm, "radius": 6 * mm});
            skCircle(sketch, "E2.9.15.0", {"center": v(-219.32, -63.4) * mm, "radius": 6 * mm});
            skCircle(sketch, "E2.9.16.0", {"center": v(-219.32, -83.4) * mm, "radius": 6 * mm});
            skCircle(sketch, "E2.9.17.0", {"center": v(-219.32, -103.4) * mm, "radius": 6 * mm});
            skCircle(sketch, "E2.9.18.0", {"center": v(-219.32, -123.4) * mm, "radius": 6 * mm});
            skCircle(sketch, "E2.9.19.0", {"center": v(-219.32, -143.4) * mm, "radius": 6 * mm});
            skCircle(sketch, "E2.9.20.0", {"center": v(-219.32, -163.4) * mm, "radius": 6 * mm});
            skCircle(sketch, "E2.9.21.0", {"center": v(-219.32, -183.4) * mm, "radius": 6 * mm});
            skCircle(sketch, "E2.9.22.0", {"center": v(-219.32, -203.4) * mm, "radius": 6 * mm});
            skCircle(sketch, "E2.9.23.0", {"center": v(-219.32, -223.4) * mm, "radius": 6 * mm});
            skCircle(sketch, "E2.9.24.0", {"center": v(-219.32, -243.4) * mm, "radius": 6 * mm});
            skCircle(sketch, "E2.9.25.0", {"center": v(-219.32, -263.4) * mm, "radius": 6 * mm});
            skCircle(sketch, "E2.9.26.0", {"center": v(-219.32, -283.4) * mm, "radius": 6 * mm});
            skCircle(sketch, "E2.9.27.0", {"center": v(-219.32, -303.4) * mm, "radius": 6 * mm});
            skCircle(sketch, "E2.9.28.0", {"center": v(-219.32, -323.4) * mm, "radius": 6 * mm});
            skCircle(sketch, "E2.9.29.0", {"center": v(-219.32, -343.4) * mm, "radius": 6 * mm});
            skCircle(sketch, "E2.9.30.0", {"center": v(-219.32, -363.4) * mm, "radius": 6 * mm});
            skCircle(sketch, "E2.9.31.0", {"center": v(-219.32, -383.4) * mm, "radius": 6 * mm});
            skCircle(sketch, "E2.9.32.0", {"center": v(-219.32, -403.4) * mm, "radius": 6 * mm});
            skCircle(sketch, "E2.9.33.0", {"center": v(-219.32, -423.4) * mm, "radius": 6 * mm});
            skCircle(sketch, "E2.9.34.0", {"center": v(-219.32, -443.4) * mm, "radius": 6 * mm});
            skCircle(sketch, "E2.9.35.0", {"center": v(-219.32, -463.4) * mm, "radius": 6 * mm});
            skCircle(sketch, "E2.9.36.0", {"center": v(-219.32, -483.4) * mm, "radius": 6 * mm});
            skCircle(sketch, "E2.9.37.0", {"center": v(-219.32, -503.4) * mm, "radius": 6 * mm});
            skCircle(sketch, "E2.9.38.0", {"center": v(-219.32, -523.4) * mm, "radius": 6 * mm});
            skCircle(sketch, "E2.9.39.0", {"center": v(-219.32, -543.4) * mm, "radius": 6 * mm});
            skCircle(sketch, "E2.9.40.0", {"center": v(-219.32, -563.4) * mm, "radius": 6 * mm});
            skCircle(sketch, "E2.9.41.0", {"center": v(-219.32, -583.4) * mm, "radius": 6 * mm});
            skCircle(sketch, "E2.9.42.0", {"center": v(-219.32, -603.4) * mm, "radius": 6 * mm});
            skCircle(sketch, "E2.9.43.0", {"center": v(-219.32, -623.4) * mm, "radius": 6 * mm});
            skCircle(sketch, "E2.9.44.0", {"center": v(-219.32, -643.4) * mm, "radius": 6 * mm});
            skCircle(sketch, "E2.9.45.0", {"center": v(-219.32, -663.4) * mm, "radius": 6 * mm});
            skCircle(sketch, "E2.9.46.0", {"center": v(-219.32, -683.4) * mm, "radius": 6 * mm});
            skCircle(sketch, "E2.9.47.0", {"center": v(-219.32, -703.4) * mm, "radius": 6 * mm});
            skCircle(sketch, "E2.9.48.0", {"center": v(-219.32, -723.4) * mm, "radius": 6 * mm});
            skCircle(sketch, "E2.9.49.0", {"center": v(-219.32, -743.4) * mm, "radius": 6 * mm});
            skCircle(sketch, "E2.10.0.0", {"center": v(-199.32, 236.6) * mm, "radius": 6 * mm});
            skCircle(sketch, "E2.10.1.0", {"center": v(-199.32, 216.6) * mm, "radius": 6 * mm});
            skCircle(sketch, "E2.10.2.0", {"center": v(-199.32, 196.6) * mm, "radius": 6 * mm});
            skCircle(sketch, "E2.10.3.0", {"center": v(-199.32, 176.6) * mm, "radius": 6 * mm});
            skCircle(sketch, "E2.10.4.0", {"center": v(-199.32, 156.6) * mm, "radius": 6 * mm});
            skCircle(sketch, "E2.10.5.0", {"center": v(-199.32, 136.6) * mm, "radius": 6 * mm});
            skCircle(sketch, "E2.10.6.0", {"center": v(-199.32, 116.6) * mm, "radius": 6 * mm});
            skCircle(sketch, "E2.10.7.0", {"center": v(-199.32, 96.6) * mm, "radius": 6 * mm});
            skCircle(sketch, "E2.10.8.0", {"center": v(-199.32, 76.6) * mm, "radius": 6 * mm});
            skCircle(sketch, "E2.10.9.0", {"center": v(-199.32, 56.6) * mm, "radius": 6 * mm});
            skCircle(sketch, "E2.10.10.0", {"center": v(-199.32, 36.6) * mm, "radius": 6 * mm});
            skCircle(sketch, "E2.10.11.0", {"center": v(-199.32, 16.6) * mm, "radius": 6 * mm});
            skCircle(sketch, "E2.10.12.0", {"center": v(-199.32, -3.4) * mm, "radius": 6 * mm});
            skCircle(sketch, "E2.10.13.0", {"center": v(-199.32, -23.4) * mm, "radius": 6 * mm});
            skCircle(sketch, "E2.10.14.0", {"center": v(-199.32, -43.4) * mm, "radius": 6 * mm});
            skCircle(sketch, "E2.10.15.0", {"center": v(-199.32, -63.4) * mm, "radius": 6 * mm});
            skCircle(sketch, "E2.10.16.0", {"center": v(-199.32, -83.4) * mm, "radius": 6 * mm});
            skCircle(sketch, "E2.10.17.0", {"center": v(-199.32, -103.4) * mm, "radius": 6 * mm});
            skCircle(sketch, "E2.10.18.0", {"center": v(-199.32, -123.4) * mm, "radius": 6 * mm});
            skCircle(sketch, "E2.10.19.0", {"center": v(-199.32, -143.4) * mm, "radius": 6 * mm});
            skCircle(sketch, "E2.10.20.0", {"center": v(-199.32, -163.4) * mm, "radius": 6 * mm});
            skCircle(sketch, "E2.10.21.0", {"center": v(-199.32, -183.4) * mm, "radius": 6 * mm});
            skCircle(sketch, "E2.10.22.0", {"center": v(-199.32, -203.4) * mm, "radius": 6 * mm});
            skCircle(sketch, "E2.10.23.0", {"center": v(-199.32, -223.4) * mm, "radius": 6 * mm});
            skCircle(sketch, "E2.10.24.0", {"center": v(-199.32, -243.4) * mm, "radius": 6 * mm});
            skCircle(sketch, "E2.10.25.0", {"center": v(-199.32, -263.4) * mm, "radius": 6 * mm});
            skCircle(sketch, "E2.10.26.0", {"center": v(-199.32, -283.4) * mm, "radius": 6 * mm});
            skCircle(sketch, "E2.10.27.0", {"center": v(-199.32, -303.4) * mm, "radius": 6 * mm});
            skCircle(sketch, "E2.10.28.0", {"center": v(-199.32, -323.4) * mm, "radius": 6 * mm});
            skCircle(sketch, "E2.10.29.0", {"center": v(-199.32, -343.4) * mm, "radius": 6 * mm});
            skCircle(sketch, "E2.10.30.0", {"center": v(-199.32, -363.4) * mm, "radius": 6 * mm});
            skCircle(sketch, "E2.10.31.0", {"center": v(-199.32, -383.4) * mm, "radius": 6 * mm});
            skCircle(sketch, "E2.10.32.0", {"center": v(-199.32, -403.4) * mm, "radius": 6 * mm});
            skCircle(sketch, "E2.10.33.0", {"center": v(-199.32, -423.4) * mm, "radius": 6 * mm});
            skCircle(sketch, "E2.10.34.0", {"center": v(-199.32, -443.4) * mm, "radius": 6 * mm});
            skCircle(sketch, "E2.10.35.0", {"center": v(-199.32, -463.4) * mm, "radius": 6 * mm});
            skCircle(sketch, "E2.10.36.0", {"center": v(-199.32, -483.4) * mm, "radius": 6 * mm});
            skCircle(sketch, "E2.10.37.0", {"center": v(-199.32, -503.4) * mm, "radius": 6 * mm});
            skCircle(sketch, "E2.10.38.0", {"center": v(-199.32, -523.4) * mm, "radius": 6 * mm});
            skCircle(sketch, "E2.10.39.0", {"center": v(-199.32, -543.4) * mm, "radius": 6 * mm});
            skCircle(sketch, "E2.10.40.0", {"center": v(-199.32, -563.4) * mm, "radius": 6 * mm});
            skCircle(sketch, "E2.10.41.0", {"center": v(-199.32, -583.4) * mm, "radius": 6 * mm});
            skCircle(sketch, "E2.10.42.0", {"center": v(-199.32, -603.4) * mm, "radius": 6 * mm});
            skCircle(sketch, "E2.10.43.0", {"center": v(-199.32, -623.4) * mm, "radius": 6 * mm});
            skCircle(sketch, "E2.10.44.0", {"center": v(-199.32, -643.4) * mm, "radius": 6 * mm});
            skCircle(sketch, "E2.10.45.0", {"center": v(-199.32, -663.4) * mm, "radius": 6 * mm});
            skCircle(sketch, "E2.10.46.0", {"center": v(-199.32, -683.4) * mm, "radius": 6 * mm});
            skCircle(sketch, "E2.10.47.0", {"center": v(-199.32, -703.4) * mm, "radius": 6 * mm});
            skCircle(sketch, "E2.10.48.0", {"center": v(-199.32, -723.4) * mm, "radius": 6 * mm});
            skCircle(sketch, "E2.10.49.0", {"center": v(-199.32, -743.4) * mm, "radius": 6 * mm});
            skCircle(sketch, "E2.11.0.0", {"center": v(-179.32, 236.6) * mm, "radius": 6 * mm});
            skCircle(sketch, "E2.11.1.0", {"center": v(-179.32, 216.6) * mm, "radius": 6 * mm});
            skCircle(sketch, "E2.11.2.0", {"center": v(-179.32, 196.6) * mm, "radius": 6 * mm});
            skCircle(sketch, "E2.11.3.0", {"center": v(-179.32, 176.6) * mm, "radius": 6 * mm});
            skCircle(sketch, "E2.11.4.0", {"center": v(-179.32, 156.6) * mm, "radius": 6 * mm});
            skCircle(sketch, "E2.11.5.0", {"center": v(-179.32, 136.6) * mm, "radius": 6 * mm});
            skCircle(sketch, "E2.11.6.0", {"center": v(-179.32, 116.6) * mm, "radius": 6 * mm});
            skCircle(sketch, "E2.11.7.0", {"center": v(-179.32, 96.6) * mm, "radius": 6 * mm});
            skCircle(sketch, "E2.11.8.0", {"center": v(-179.32, 76.6) * mm, "radius": 6 * mm});
            skCircle(sketch, "E2.11.9.0", {"center": v(-179.32, 56.6) * mm, "radius": 6 * mm});
            skCircle(sketch, "E2.11.10.0", {"center": v(-179.32, 36.6) * mm, "radius": 6 * mm});
            skCircle(sketch, "E2.11.11.0", {"center": v(-179.32, 16.6) * mm, "radius": 6 * mm});
            skCircle(sketch, "E2.11.12.0", {"center": v(-179.32, -3.4) * mm, "radius": 6 * mm});
            skCircle(sketch, "E2.11.13.0", {"center": v(-179.32, -23.4) * mm, "radius": 6 * mm});
            skCircle(sketch, "E2.11.14.0", {"center": v(-179.32, -43.4) * mm, "radius": 6 * mm});
            skCircle(sketch, "E2.11.15.0", {"center": v(-179.32, -63.4) * mm, "radius": 6 * mm});
            skCircle(sketch, "E2.11.16.0", {"center": v(-179.32, -83.4) * mm, "radius": 6 * mm});
            skCircle(sketch, "E2.11.17.0", {"center": v(-179.32, -103.4) * mm, "radius": 6 * mm});
            skCircle(sketch, "E2.11.18.0", {"center": v(-179.32, -123.4) * mm, "radius": 6 * mm});
            skCircle(sketch, "E2.11.19.0", {"center": v(-179.32, -143.4) * mm, "radius": 6 * mm});
            skCircle(sketch, "E2.11.20.0", {"center": v(-179.32, -163.4) * mm, "radius": 6 * mm});
            skCircle(sketch, "E2.11.21.0", {"center": v(-179.32, -183.4) * mm, "radius": 6 * mm});
            skCircle(sketch, "E2.11.22.0", {"center": v(-179.32, -203.4) * mm, "radius": 6 * mm});
            skCircle(sketch, "E2.11.23.0", {"center": v(-179.32, -223.4) * mm, "radius": 6 * mm});
            skCircle(sketch, "E2.11.24.0", {"center": v(-179.32, -243.4) * mm, "radius": 6 * mm});
            skCircle(sketch, "E2.11.25.0", {"center": v(-179.32, -263.4) * mm, "radius": 6 * mm});
            skCircle(sketch, "E2.11.26.0", {"center": v(-179.32, -283.4) * mm, "radius": 6 * mm});
            skCircle(sketch, "E2.11.27.0", {"center": v(-179.32, -303.4) * mm, "radius": 6 * mm});
            skCircle(sketch, "E2.11.28.0", {"center": v(-179.32, -323.4) * mm, "radius": 6 * mm});
            skCircle(sketch, "E2.11.29.0", {"center": v(-179.32, -343.4) * mm, "radius": 6 * mm});
            skCircle(sketch, "E2.11.30.0", {"center": v(-179.32, -363.4) * mm, "radius": 6 * mm});
            skCircle(sketch, "E2.11.31.0", {"center": v(-179.32, -383.4) * mm, "radius": 6 * mm});
            skCircle(sketch, "E2.11.32.0", {"center": v(-179.32, -403.4) * mm, "radius": 6 * mm});
            skCircle(sketch, "E2.11.33.0", {"center": v(-179.32, -423.4) * mm, "radius": 6 * mm});
            skCircle(sketch, "E2.11.34.0", {"center": v(-179.32, -443.4) * mm, "radius": 6 * mm});
            skCircle(sketch, "E2.11.35.0", {"center": v(-179.32, -463.4) * mm, "radius": 6 * mm});
            skCircle(sketch, "E2.11.36.0", {"center": v(-179.32, -483.4) * mm, "radius": 6 * mm});
            skCircle(sketch, "E2.11.37.0", {"center": v(-179.32, -503.4) * mm, "radius": 6 * mm});
            skCircle(sketch, "E2.11.38.0", {"center": v(-179.32, -523.4) * mm, "radius": 6 * mm});
            skCircle(sketch, "E2.11.39.0", {"center": v(-179.32, -543.4) * mm, "radius": 6 * mm});
            skCircle(sketch, "E2.11.40.0", {"center": v(-179.32, -563.4) * mm, "radius": 6 * mm});
            skCircle(sketch, "E2.11.41.0", {"center": v(-179.32, -583.4) * mm, "radius": 6 * mm});
            skCircle(sketch, "E2.11.42.0", {"center": v(-179.32, -603.4) * mm, "radius": 6 * mm});
            skCircle(sketch, "E2.11.43.0", {"center": v(-179.32, -623.4) * mm, "radius": 6 * mm});
            skCircle(sketch, "E2.11.44.0", {"center": v(-179.32, -643.4) * mm, "radius": 6 * mm});
            skCircle(sketch, "E2.11.45.0", {"center": v(-179.32, -663.4) * mm, "radius": 6 * mm});
            skCircle(sketch, "E2.11.46.0", {"center": v(-179.32, -683.4) * mm, "radius": 6 * mm});
            skCircle(sketch, "E2.11.47.0", {"center": v(-179.32, -703.4) * mm, "radius": 6 * mm});
            skCircle(sketch, "E2.11.48.0", {"center": v(-179.32, -723.4) * mm, "radius": 6 * mm});
            skCircle(sketch, "E2.11.49.0", {"center": v(-179.32, -743.4) * mm, "radius": 6 * mm});
            skCircle(sketch, "E2.12.0.0", {"center": v(-159.32, 236.6) * mm, "radius": 6 * mm});
            skCircle(sketch, "E2.12.1.0", {"center": v(-159.32, 216.6) * mm, "radius": 6 * mm});
            skCircle(sketch, "E2.12.2.0", {"center": v(-159.32, 196.6) * mm, "radius": 6 * mm});
            skCircle(sketch, "E2.12.3.0", {"center": v(-159.32, 176.6) * mm, "radius": 6 * mm});
            skCircle(sketch, "E2.12.4.0", {"center": v(-159.32, 156.6) * mm, "radius": 6 * mm});
            skCircle(sketch, "E2.12.5.0", {"center": v(-159.32, 136.6) * mm, "radius": 6 * mm});
            skCircle(sketch, "E2.12.6.0", {"center": v(-159.32, 116.6) * mm, "radius": 6 * mm});
            skCircle(sketch, "E2.12.7.0", {"center": v(-159.32, 96.6) * mm, "radius": 6 * mm});
            skCircle(sketch, "E2.12.8.0", {"center": v(-159.32, 76.6) * mm, "radius": 6 * mm});
            skCircle(sketch, "E2.12.9.0", {"center": v(-159.32, 56.6) * mm, "radius": 6 * mm});
            skCircle(sketch, "E2.12.10.0", {"center": v(-159.32, 36.6) * mm, "radius": 6 * mm});
            skCircle(sketch, "E2.12.11.0", {"center": v(-159.32, 16.6) * mm, "radius": 6 * mm});
            skCircle(sketch, "E2.12.12.0", {"center": v(-159.32, -3.4) * mm, "radius": 6 * mm});
            skCircle(sketch, "E2.12.13.0", {"center": v(-159.32, -23.4) * mm, "radius": 6 * mm});
            skCircle(sketch, "E2.12.14.0", {"center": v(-159.32, -43.4) * mm, "radius": 6 * mm});
            skCircle(sketch, "E2.12.15.0", {"center": v(-159.32, -63.4) * mm, "radius": 6 * mm});
            skCircle(sketch, "E2.12.16.0", {"center": v(-159.32, -83.4) * mm, "radius": 6 * mm});
            skCircle(sketch, "E2.12.17.0", {"center": v(-159.32, -103.4) * mm, "radius": 6 * mm});
            skCircle(sketch, "E2.12.18.0", {"center": v(-159.32, -123.4) * mm, "radius": 6 * mm});
            skCircle(sketch, "E2.12.19.0", {"center": v(-159.32, -143.4) * mm, "radius": 6 * mm});
            skCircle(sketch, "E2.12.20.0", {"center": v(-159.32, -163.4) * mm, "radius": 6 * mm});
            skCircle(sketch, "E2.12.21.0", {"center": v(-159.32, -183.4) * mm, "radius": 6 * mm});
            skCircle(sketch, "E2.12.22.0", {"center": v(-159.32, -203.4) * mm, "radius": 6 * mm});
            skCircle(sketch, "E2.12.23.0", {"center": v(-159.32, -223.4) * mm, "radius": 6 * mm});
            skCircle(sketch, "E2.12.24.0", {"center": v(-159.32, -243.4) * mm, "radius": 6 * mm});
            skCircle(sketch, "E2.12.25.0", {"center": v(-159.32, -263.4) * mm, "radius": 6 * mm});
            skCircle(sketch, "E2.12.26.0", {"center": v(-159.32, -283.4) * mm, "radius": 6 * mm});
            skCircle(sketch, "E2.12.27.0", {"center": v(-159.32, -303.4) * mm, "radius": 6 * mm});
            skCircle(sketch, "E2.12.28.0", {"center": v(-159.32, -323.4) * mm, "radius": 6 * mm});
            skCircle(sketch, "E2.12.29.0", {"center": v(-159.32, -343.4) * mm, "radius": 6 * mm});
            skCircle(sketch, "E2.12.30.0", {"center": v(-159.32, -363.4) * mm, "radius": 6 * mm});
            skCircle(sketch, "E2.12.31.0", {"center": v(-159.32, -383.4) * mm, "radius": 6 * mm});
            skCircle(sketch, "E2.12.32.0", {"center": v(-159.32, -403.4) * mm, "radius": 6 * mm});
            skCircle(sketch, "E2.12.33.0", {"center": v(-159.32, -423.4) * mm, "radius": 6 * mm});
            skCircle(sketch, "E2.12.34.0", {"center": v(-159.32, -443.4) * mm, "radius": 6 * mm});
            skCircle(sketch, "E2.12.35.0", {"center": v(-159.32, -463.4) * mm, "radius": 6 * mm});
            skCircle(sketch, "E2.12.36.0", {"center": v(-159.32, -483.4) * mm, "radius": 6 * mm});
            skCircle(sketch, "E2.12.37.0", {"center": v(-159.32, -503.4) * mm, "radius": 6 * mm});
            skCircle(sketch, "E2.12.38.0", {"center": v(-159.32, -523.4) * mm, "radius": 6 * mm});
            skCircle(sketch, "E2.12.39.0", {"center": v(-159.32, -543.4) * mm, "radius": 6 * mm});
            skCircle(sketch, "E2.12.40.0", {"center": v(-159.32, -563.4) * mm, "radius": 6 * mm});
            skCircle(sketch, "E2.12.41.0", {"center": v(-159.32, -583.4) * mm, "radius": 6 * mm});
            skCircle(sketch, "E2.12.42.0", {"center": v(-159.32, -603.4) * mm, "radius": 6 * mm});
            skCircle(sketch, "E2.12.43.0", {"center": v(-159.32, -623.4) * mm, "radius": 6 * mm});
            skCircle(sketch, "E2.12.44.0", {"center": v(-159.32, -643.4) * mm, "radius": 6 * mm});
            skCircle(sketch, "E2.12.45.0", {"center": v(-159.32, -663.4) * mm, "radius": 6 * mm});
            skCircle(sketch, "E2.12.46.0", {"center": v(-159.32, -683.4) * mm, "radius": 6 * mm});
            skCircle(sketch, "E2.12.47.0", {"center": v(-159.32, -703.4) * mm, "radius": 6 * mm});
            skCircle(sketch, "E2.12.48.0", {"center": v(-159.32, -723.4) * mm, "radius": 6 * mm});
            skCircle(sketch, "E2.12.49.0", {"center": v(-159.32, -743.4) * mm, "radius": 6 * mm});
            skCircle(sketch, "E2.13.0.0", {"center": v(-139.32, 236.6) * mm, "radius": 6 * mm});
            skCircle(sketch, "E2.13.1.0", {"center": v(-139.32, 216.6) * mm, "radius": 6 * mm});
            skCircle(sketch, "E2.13.2.0", {"center": v(-139.32, 196.6) * mm, "radius": 6 * mm});
            skCircle(sketch, "E2.13.3.0", {"center": v(-139.32, 176.6) * mm, "radius": 6 * mm});
            skCircle(sketch, "E2.13.4.0", {"center": v(-139.32, 156.6) * mm, "radius": 6 * mm});
            skCircle(sketch, "E2.13.5.0", {"center": v(-139.32, 136.6) * mm, "radius": 6 * mm});
            skCircle(sketch, "E2.13.6.0", {"center": v(-139.32, 116.6) * mm, "radius": 6 * mm});
            skCircle(sketch, "E2.13.7.0", {"center": v(-139.32, 96.6) * mm, "radius": 6 * mm});
            skCircle(sketch, "E2.13.8.0", {"center": v(-139.32, 76.6) * mm, "radius": 6 * mm});
            skCircle(sketch, "E2.13.9.0", {"center": v(-139.32, 56.6) * mm, "radius": 6 * mm});
            skCircle(sketch, "E2.13.10.0", {"center": v(-139.32, 36.6) * mm, "radius": 6 * mm});
            skCircle(sketch, "E2.13.11.0", {"center": v(-139.32, 16.6) * mm, "radius": 6 * mm});
            skCircle(sketch, "E2.13.12.0", {"center": v(-139.32, -3.4) * mm, "radius": 6 * mm});
            skCircle(sketch, "E2.13.13.0", {"center": v(-139.32, -23.4) * mm, "radius": 6 * mm});
            skCircle(sketch, "E2.13.14.0", {"center": v(-139.32, -43.4) * mm, "radius": 6 * mm});
            skCircle(sketch, "E2.13.15.0", {"center": v(-139.32, -63.4) * mm, "radius": 6 * mm});
            skCircle(sketch, "E2.13.16.0", {"center": v(-139.32, -83.4) * mm, "radius": 6 * mm});
            skCircle(sketch, "E2.13.17.0", {"center": v(-139.32, -103.4) * mm, "radius": 6 * mm});
            skCircle(sketch, "E2.13.18.0", {"center": v(-139.32, -123.4) * mm, "radius": 6 * mm});
            skCircle(sketch, "E2.13.19.0", {"center": v(-139.32, -143.4) * mm, "radius": 6 * mm});
            skCircle(sketch, "E2.13.20.0", {"center": v(-139.32, -163.4) * mm, "radius": 6 * mm});
            skCircle(sketch, "E2.13.21.0", {"center": v(-139.32, -183.4) * mm, "radius": 6 * mm});
            skCircle(sketch, "E2.13.22.0", {"center": v(-139.32, -203.4) * mm, "radius": 6 * mm});
            skCircle(sketch, "E2.13.23.0", {"center": v(-139.32, -223.4) * mm, "radius": 6 * mm});
            skCircle(sketch, "E2.13.24.0", {"center": v(-139.32, -243.4) * mm, "radius": 6 * mm});
            skCircle(sketch, "E2.13.25.0", {"center": v(-139.32, -263.4) * mm, "radius": 6 * mm});
            skCircle(sketch, "E2.13.26.0", {"center": v(-139.32, -283.4) * mm, "radius": 6 * mm});
            skCircle(sketch, "E2.13.27.0", {"center": v(-139.32, -303.4) * mm, "radius": 6 * mm});
            skCircle(sketch, "E2.13.28.0", {"center": v(-139.32, -323.4) * mm, "radius": 6 * mm});
            skCircle(sketch, "E2.13.29.0", {"center": v(-139.32, -343.4) * mm, "radius": 6 * mm});
            skCircle(sketch, "E2.13.30.0", {"center": v(-139.32, -363.4) * mm, "radius": 6 * mm});
            skCircle(sketch, "E2.13.31.0", {"center": v(-139.32, -383.4) * mm, "radius": 6 * mm});
            skCircle(sketch, "E2.13.32.0", {"center": v(-139.32, -403.4) * mm, "radius": 6 * mm});
            skCircle(sketch, "E2.13.33.0", {"center": v(-139.32, -423.4) * mm, "radius": 6 * mm});
            skCircle(sketch, "E2.13.34.0", {"center": v(-139.32, -443.4) * mm, "radius": 6 * mm});
            skCircle(sketch, "E2.13.35.0", {"center": v(-139.32, -463.4) * mm, "radius": 6 * mm});
            skCircle(sketch, "E2.13.36.0", {"center": v(-139.32, -483.4) * mm, "radius": 6 * mm});
            skCircle(sketch, "E2.13.37.0", {"center": v(-139.32, -503.4) * mm, "radius": 6 * mm});
            skCircle(sketch, "E2.13.38.0", {"center": v(-139.32, -523.4) * mm, "radius": 6 * mm});
            skCircle(sketch, "E2.13.39.0", {"center": v(-139.32, -543.4) * mm, "radius": 6 * mm});
            skCircle(sketch, "E2.13.40.0", {"center": v(-139.32, -563.4) * mm, "radius": 6 * mm});
            skCircle(sketch, "E2.13.41.0", {"center": v(-139.32, -583.4) * mm, "radius": 6 * mm});
            skCircle(sketch, "E2.13.42.0", {"center": v(-139.32, -603.4) * mm, "radius": 6 * mm});
            skCircle(sketch, "E2.13.43.0", {"center": v(-139.32, -623.4) * mm, "radius": 6 * mm});
            skCircle(sketch, "E2.13.44.0", {"center": v(-139.32, -643.4) * mm, "radius": 6 * mm});
            skCircle(sketch, "E2.13.45.0", {"center": v(-139.32, -663.4) * mm, "radius": 6 * mm});
            skCircle(sketch, "E2.13.46.0", {"center": v(-139.32, -683.4) * mm, "radius": 6 * mm});
            skCircle(sketch, "E2.13.47.0", {"center": v(-139.32, -703.4) * mm, "radius": 6 * mm});
            skCircle(sketch, "E2.13.48.0", {"center": v(-139.32, -723.4) * mm, "radius": 6 * mm});
            skCircle(sketch, "E2.13.49.0", {"center": v(-139.32, -743.4) * mm, "radius": 6 * mm});
            skCircle(sketch, "E2.14.0.0", {"center": v(-119.32, 236.6) * mm, "radius": 6 * mm});
            skCircle(sketch, "E2.14.1.0", {"center": v(-119.32, 216.6) * mm, "radius": 6 * mm});
            skCircle(sketch, "E2.14.2.0", {"center": v(-119.32, 196.6) * mm, "radius": 6 * mm});
            skCircle(sketch, "E2.14.3.0", {"center": v(-119.32, 176.6) * mm, "radius": 6 * mm});
            skCircle(sketch, "E2.14.4.0", {"center": v(-119.32, 156.6) * mm, "radius": 6 * mm});
            skCircle(sketch, "E2.14.5.0", {"center": v(-119.32, 136.6) * mm, "radius": 6 * mm});
            skCircle(sketch, "E2.14.6.0", {"center": v(-119.32, 116.6) * mm, "radius": 6 * mm});
            skCircle(sketch, "E2.14.7.0", {"center": v(-119.32, 96.6) * mm, "radius": 6 * mm});
            skCircle(sketch, "E2.14.8.0", {"center": v(-119.32, 76.6) * mm, "radius": 6 * mm});
            skCircle(sketch, "E2.14.9.0", {"center": v(-119.32, 56.6) * mm, "radius": 6 * mm});
            skCircle(sketch, "E2.14.10.0", {"center": v(-119.32, 36.6) * mm, "radius": 6 * mm});
            skCircle(sketch, "E2.14.11.0", {"center": v(-119.32, 16.6) * mm, "radius": 6 * mm});
            skCircle(sketch, "E2.14.12.0", {"center": v(-119.32, -3.4) * mm, "radius": 6 * mm});
            skCircle(sketch, "E2.14.13.0", {"center": v(-119.32, -23.4) * mm, "radius": 6 * mm});
            skCircle(sketch, "E2.14.14.0", {"center": v(-119.32, -43.4) * mm, "radius": 6 * mm});
            skCircle(sketch, "E2.14.15.0", {"center": v(-119.32, -63.4) * mm, "radius": 6 * mm});
            skCircle(sketch, "E2.14.16.0", {"center": v(-119.32, -83.4) * mm, "radius": 6 * mm});
            skCircle(sketch, "E2.14.17.0", {"center": v(-119.32, -103.4) * mm, "radius": 6 * mm});
            skCircle(sketch, "E2.14.18.0", {"center": v(-119.32, -123.4) * mm, "radius": 6 * mm});
            skCircle(sketch, "E2.14.19.0", {"center": v(-119.32, -143.4) * mm, "radius": 6 * mm});
            skCircle(sketch, "E2.14.20.0", {"center": v(-119.32, -163.4) * mm, "radius": 6 * mm});
            skCircle(sketch, "E2.14.21.0", {"center": v(-119.32, -183.4) * mm, "radius": 6 * mm});
            skCircle(sketch, "E2.14.22.0", {"center": v(-119.32, -203.4) * mm, "radius": 6 * mm});
            skCircle(sketch, "E2.14.23.0", {"center": v(-119.32, -223.4) * mm, "radius": 6 * mm});
            skCircle(sketch, "E2.14.24.0", {"center": v(-119.32, -243.4) * mm, "radius": 6 * mm});
            skCircle(sketch, "E2.14.25.0", {"center": v(-119.32, -263.4) * mm, "radius": 6 * mm});
            skCircle(sketch, "E2.14.26.0", {"center": v(-119.32, -283.4) * mm, "radius": 6 * mm});
            skCircle(sketch, "E2.14.27.0", {"center": v(-119.32, -303.4) * mm, "radius": 6 * mm});
            skCircle(sketch, "E2.14.28.0", {"center": v(-119.32, -323.4) * mm, "radius": 6 * mm});
            skCircle(sketch, "E2.14.29.0", {"center": v(-119.32, -343.4) * mm, "radius": 6 * mm});
            skCircle(sketch, "E2.14.30.0", {"center": v(-119.32, -363.4) * mm, "radius": 6 * mm});
            skCircle(sketch, "E2.14.31.0", {"center": v(-119.32, -383.4) * mm, "radius": 6 * mm});
            skCircle(sketch, "E2.14.32.0", {"center": v(-119.32, -403.4) * mm, "radius": 6 * mm});
            skCircle(sketch, "E2.14.33.0", {"center": v(-119.32, -423.4) * mm, "radius": 6 * mm});
            skCircle(sketch, "E2.14.34.0", {"center": v(-119.32, -443.4) * mm, "radius": 6 * mm});
            skCircle(sketch, "E2.14.35.0", {"center": v(-119.32, -463.4) * mm, "radius": 6 * mm});
            skCircle(sketch, "E2.14.36.0", {"center": v(-119.32, -483.4) * mm, "radius": 6 * mm});
            skCircle(sketch, "E2.14.37.0", {"center": v(-119.32, -503.4) * mm, "radius": 6 * mm});
            skCircle(sketch, "E2.14.38.0", {"center": v(-119.32, -523.4) * mm, "radius": 6 * mm});
            skCircle(sketch, "E2.14.39.0", {"center": v(-119.32, -543.4) * mm, "radius": 6 * mm});
            skCircle(sketch, "E2.14.40.0", {"center": v(-119.32, -563.4) * mm, "radius": 6 * mm});
            skCircle(sketch, "E2.14.41.0", {"center": v(-119.32, -583.4) * mm, "radius": 6 * mm});
            skCircle(sketch, "E2.14.42.0", {"center": v(-119.32, -603.4) * mm, "radius": 6 * mm});
            skCircle(sketch, "E2.14.43.0", {"center": v(-119.32, -623.4) * mm, "radius": 6 * mm});
            skCircle(sketch, "E2.14.44.0", {"center": v(-119.32, -643.4) * mm, "radius": 6 * mm});
            skCircle(sketch, "E2.14.45.0", {"center": v(-119.32, -663.4) * mm, "radius": 6 * mm});
            skCircle(sketch, "E2.14.46.0", {"center": v(-119.32, -683.4) * mm, "radius": 6 * mm});
            skCircle(sketch, "E2.14.47.0", {"center": v(-119.32, -703.4) * mm, "radius": 6 * mm});
            skCircle(sketch, "E2.14.48.0", {"center": v(-119.32, -723.4) * mm, "radius": 6 * mm});
            skCircle(sketch, "E2.14.49.0", {"center": v(-119.32, -743.4) * mm, "radius": 6 * mm});
            skCircle(sketch, "E2.15.0.0", {"center": v(-99.32, 236.6) * mm, "radius": 6 * mm});
            skCircle(sketch, "E2.15.1.0", {"center": v(-99.32, 216.6) * mm, "radius": 6 * mm});
            skCircle(sketch, "E2.15.2.0", {"center": v(-99.32, 196.6) * mm, "radius": 6 * mm});
            skCircle(sketch, "E2.15.3.0", {"center": v(-99.32, 176.6) * mm, "radius": 6 * mm});
            skCircle(sketch, "E2.15.4.0", {"center": v(-99.32, 156.6) * mm, "radius": 6 * mm});
            skCircle(sketch, "E2.15.5.0", {"center": v(-99.32, 136.6) * mm, "radius": 6 * mm});
            skCircle(sketch, "E2.15.6.0", {"center": v(-99.32, 116.6) * mm, "radius": 6 * mm});
            skCircle(sketch, "E2.15.7.0", {"center": v(-99.32, 96.6) * mm, "radius": 6 * mm});
            skCircle(sketch, "E2.15.8.0", {"center": v(-99.32, 76.6) * mm, "radius": 6 * mm});
            skCircle(sketch, "E2.15.9.0", {"center": v(-99.32, 56.6) * mm, "radius": 6 * mm});
            skCircle(sketch, "E2.15.10.0", {"center": v(-99.32, 36.6) * mm, "radius": 6 * mm});
            skCircle(sketch, "E2.15.11.0", {"center": v(-99.32, 16.6) * mm, "radius": 6 * mm});
            skCircle(sketch, "E2.15.12.0", {"center": v(-99.32, -3.4) * mm, "radius": 6 * mm});
            skCircle(sketch, "E2.15.13.0", {"center": v(-99.32, -23.4) * mm, "radius": 6 * mm});
            skCircle(sketch, "E2.15.14.0", {"center": v(-99.32, -43.4) * mm, "radius": 6 * mm});
            skCircle(sketch, "E2.15.15.0", {"center": v(-99.32, -63.4) * mm, "radius": 6 * mm});
            skCircle(sketch, "E2.15.16.0", {"center": v(-99.32, -83.4) * mm, "radius": 6 * mm});
            skCircle(sketch, "E2.15.17.0", {"center": v(-99.32, -103.4) * mm, "radius": 6 * mm});
            skCircle(sketch, "E2.15.18.0", {"center": v(-99.32, -123.4) * mm, "radius": 6 * mm});
            skCircle(sketch, "E2.15.19.0", {"center": v(-99.32, -143.4) * mm, "radius": 6 * mm});
            skCircle(sketch, "E2.15.20.0", {"center": v(-99.32, -163.4) * mm, "radius": 6 * mm});
            skCircle(sketch, "E2.15.21.0", {"center": v(-99.32, -183.4) * mm, "radius": 6 * mm});
            skCircle(sketch, "E2.15.22.0", {"center": v(-99.32, -203.4) * mm, "radius": 6 * mm});
            skCircle(sketch, "E2.15.23.0", {"center": v(-99.32, -223.4) * mm, "radius": 6 * mm});
            skCircle(sketch, "E2.15.24.0", {"center": v(-99.32, -243.4) * mm, "radius": 6 * mm});
            skCircle(sketch, "E2.15.25.0", {"center": v(-99.32, -263.4) * mm, "radius": 6 * mm});
            skCircle(sketch, "E2.15.26.0", {"center": v(-99.32, -283.4) * mm, "radius": 6 * mm});
            skCircle(sketch, "E2.15.27.0", {"center": v(-99.32, -303.4) * mm, "radius": 6 * mm});
            skCircle(sketch, "E2.15.28.0", {"center": v(-99.32, -323.4) * mm, "radius": 6 * mm});
            skCircle(sketch, "E2.15.29.0", {"center": v(-99.32, -343.4) * mm, "radius": 6 * mm});
            skCircle(sketch, "E2.15.30.0", {"center": v(-99.32, -363.4) * mm, "radius": 6 * mm});
            skCircle(sketch, "E2.15.31.0", {"center": v(-99.32, -383.4) * mm, "radius": 6 * mm});
            skCircle(sketch, "E2.15.32.0", {"center": v(-99.32, -403.4) * mm, "radius": 6 * mm});
            skCircle(sketch, "E2.15.33.0", {"center": v(-99.32, -423.4) * mm, "radius": 6 * mm});
            skCircle(sketch, "E2.15.34.0", {"center": v(-99.32, -443.4) * mm, "radius": 6 * mm});
            skCircle(sketch, "E2.15.35.0", {"center": v(-99.32, -463.4) * mm, "radius": 6 * mm});
            skCircle(sketch, "E2.15.36.0", {"center": v(-99.32, -483.4) * mm, "radius": 6 * mm});
            skCircle(sketch, "E2.15.37.0", {"center": v(-99.32, -503.4) * mm, "radius": 6 * mm});
            skCircle(sketch, "E2.15.38.0", {"center": v(-99.32, -523.4) * mm, "radius": 6 * mm});
            skCircle(sketch, "E2.15.39.0", {"center": v(-99.32, -543.4) * mm, "radius": 6 * mm});
            skCircle(sketch, "E2.15.40.0", {"center": v(-99.32, -563.4) * mm, "radius": 6 * mm});
            skCircle(sketch, "E2.15.41.0", {"center": v(-99.32, -583.4) * mm, "radius": 6 * mm});
            skCircle(sketch, "E2.15.42.0", {"center": v(-99.32, -603.4) * mm, "radius": 6 * mm});
            skCircle(sketch, "E2.15.43.0", {"center": v(-99.32, -623.4) * mm, "radius": 6 * mm});
            skCircle(sketch, "E2.15.44.0", {"center": v(-99.32, -643.4) * mm, "radius": 6 * mm});
            skCircle(sketch, "E2.15.45.0", {"center": v(-99.32, -663.4) * mm, "radius": 6 * mm});
            skCircle(sketch, "E2.15.46.0", {"center": v(-99.32, -683.4) * mm, "radius": 6 * mm});
            skCircle(sketch, "E2.15.47.0", {"center": v(-99.32, -703.4) * mm, "radius": 6 * mm});
            skCircle(sketch, "E2.15.48.0", {"center": v(-99.32, -723.4) * mm, "radius": 6 * mm});
            skCircle(sketch, "E2.15.49.0", {"center": v(-99.32, -743.4) * mm, "radius": 6 * mm});
            skCircle(sketch, "E2.16.0.0", {"center": v(-79.32, 236.6) * mm, "radius": 6 * mm});
            skCircle(sketch, "E2.16.1.0", {"center": v(-79.32, 216.6) * mm, "radius": 6 * mm});
            skCircle(sketch, "E2.16.2.0", {"center": v(-79.32, 196.6) * mm, "radius": 6 * mm});
            skCircle(sketch, "E2.16.3.0", {"center": v(-79.32, 176.6) * mm, "radius": 6 * mm});
            skCircle(sketch, "E2.16.4.0", {"center": v(-79.32, 156.6) * mm, "radius": 6 * mm});
            skCircle(sketch, "E2.16.5.0", {"center": v(-79.32, 136.6) * mm, "radius": 6 * mm});
            skCircle(sketch, "E2.16.6.0", {"center": v(-79.32, 116.6) * mm, "radius": 6 * mm});
            skCircle(sketch, "E2.16.7.0", {"center": v(-79.32, 96.6) * mm, "radius": 6 * mm});
            skCircle(sketch, "E2.16.8.0", {"center": v(-79.32, 76.6) * mm, "radius": 6 * mm});
            skCircle(sketch, "E2.16.9.0", {"center": v(-79.32, 56.6) * mm, "radius": 6 * mm});
            skCircle(sketch, "E2.16.10.0", {"center": v(-79.32, 36.6) * mm, "radius": 6 * mm});
            skCircle(sketch, "E2.16.11.0", {"center": v(-79.32, 16.6) * mm, "radius": 6 * mm});
            skCircle(sketch, "E2.16.12.0", {"center": v(-79.32, -3.4) * mm, "radius": 6 * mm});
            skCircle(sketch, "E2.16.13.0", {"center": v(-79.32, -23.4) * mm, "radius": 6 * mm});
            skCircle(sketch, "E2.16.14.0", {"center": v(-79.32, -43.4) * mm, "radius": 6 * mm});
            skCircle(sketch, "E2.16.15.0", {"center": v(-79.32, -63.4) * mm, "radius": 6 * mm});
            skCircle(sketch, "E2.16.16.0", {"center": v(-79.32, -83.4) * mm, "radius": 6 * mm});
            skCircle(sketch, "E2.16.17.0", {"center": v(-79.32, -103.4) * mm, "radius": 6 * mm});
            skCircle(sketch, "E2.16.18.0", {"center": v(-79.32, -123.4) * mm, "radius": 6 * mm});
            skCircle(sketch, "E2.16.19.0", {"center": v(-79.32, -143.4) * mm, "radius": 6 * mm});
            skCircle(sketch, "E2.16.20.0", {"center": v(-79.32, -163.4) * mm, "radius": 6 * mm});
            skCircle(sketch, "E2.16.21.0", {"center": v(-79.32, -183.4) * mm, "radius": 6 * mm});
            skCircle(sketch, "E2.16.22.0", {"center": v(-79.32, -203.4) * mm, "radius": 6 * mm});
            skCircle(sketch, "E2.16.23.0", {"center": v(-79.32, -223.4) * mm, "radius": 6 * mm});
            skCircle(sketch, "E2.16.24.0", {"center": v(-79.32, -243.4) * mm, "radius": 6 * mm});
            skCircle(sketch, "E2.16.25.0", {"center": v(-79.32, -263.4) * mm, "radius": 6 * mm});
            skCircle(sketch, "E2.16.26.0", {"center": v(-79.32, -283.4) * mm, "radius": 6 * mm});
            skCircle(sketch, "E2.16.27.0", {"center": v(-79.32, -303.4) * mm, "radius": 6 * mm});
            skCircle(sketch, "E2.16.28.0", {"center": v(-79.32, -323.4) * mm, "radius": 6 * mm});
            skCircle(sketch, "E2.16.29.0", {"center": v(-79.32, -343.4) * mm, "radius": 6 * mm});
            skCircle(sketch, "E2.16.30.0", {"center": v(-79.32, -363.4) * mm, "radius": 6 * mm});
            skCircle(sketch, "E2.16.31.0", {"center": v(-79.32, -383.4) * mm, "radius": 6 * mm});
            skCircle(sketch, "E2.16.32.0", {"center": v(-79.32, -403.4) * mm, "radius": 6 * mm});
            skCircle(sketch, "E2.16.33.0", {"center": v(-79.32, -423.4) * mm, "radius": 6 * mm});
            skCircle(sketch, "E2.16.34.0", {"center": v(-79.32, -443.4) * mm, "radius": 6 * mm});
            skCircle(sketch, "E2.16.35.0", {"center": v(-79.32, -463.4) * mm, "radius": 6 * mm});
            skCircle(sketch, "E2.16.36.0", {"center": v(-79.32, -483.4) * mm, "radius": 6 * mm});
            skCircle(sketch, "E2.16.37.0", {"center": v(-79.32, -503.4) * mm, "radius": 6 * mm});
            skCircle(sketch, "E2.16.38.0", {"center": v(-79.32, -523.4) * mm, "radius": 6 * mm});
            skCircle(sketch, "E2.16.39.0", {"center": v(-79.32, -543.4) * mm, "radius": 6 * mm});
            skCircle(sketch, "E2.16.40.0", {"center": v(-79.32, -563.4) * mm, "radius": 6 * mm});
            skCircle(sketch, "E2.16.41.0", {"center": v(-79.32, -583.4) * mm, "radius": 6 * mm});
            skCircle(sketch, "E2.16.42.0", {"center": v(-79.32, -603.4) * mm, "radius": 6 * mm});
            skCircle(sketch, "E2.16.43.0", {"center": v(-79.32, -623.4) * mm, "radius": 6 * mm});
            skCircle(sketch, "E2.16.44.0", {"center": v(-79.32, -643.4) * mm, "radius": 6 * mm});
            skCircle(sketch, "E2.16.45.0", {"center": v(-79.32, -663.4) * mm, "radius": 6 * mm});
            skCircle(sketch, "E2.16.46.0", {"center": v(-79.32, -683.4) * mm, "radius": 6 * mm});
            skCircle(sketch, "E2.16.47.0", {"center": v(-79.32, -703.4) * mm, "radius": 6 * mm});
            skCircle(sketch, "E2.16.48.0", {"center": v(-79.32, -723.4) * mm, "radius": 6 * mm});
            skCircle(sketch, "E2.16.49.0", {"center": v(-79.32, -743.4) * mm, "radius": 6 * mm});
            skCircle(sketch, "E2.17.0.0", {"center": v(-59.32, 236.6) * mm, "radius": 6 * mm});
            skCircle(sketch, "E2.17.1.0", {"center": v(-59.32, 216.6) * mm, "radius": 6 * mm});
            skCircle(sketch, "E2.17.2.0", {"center": v(-59.32, 196.6) * mm, "radius": 6 * mm});
            skCircle(sketch, "E2.17.3.0", {"center": v(-59.32, 176.6) * mm, "radius": 6 * mm});
            skCircle(sketch, "E2.17.4.0", {"center": v(-59.32, 156.6) * mm, "radius": 6 * mm});
            skCircle(sketch, "E2.17.5.0", {"center": v(-59.32, 136.6) * mm, "radius": 6 * mm});
            skCircle(sketch, "E2.17.6.0", {"center": v(-59.32, 116.6) * mm, "radius": 6 * mm});
            skCircle(sketch, "E2.17.7.0", {"center": v(-59.32, 96.6) * mm, "radius": 6 * mm});
            skCircle(sketch, "E2.17.8.0", {"center": v(-59.32, 76.6) * mm, "radius": 6 * mm});
            skCircle(sketch, "E2.17.9.0", {"center": v(-59.32, 56.6) * mm, "radius": 6 * mm});
            skCircle(sketch, "E2.17.10.0", {"center": v(-59.32, 36.6) * mm, "radius": 6 * mm});
            skCircle(sketch, "E2.17.11.0", {"center": v(-59.32, 16.6) * mm, "radius": 6 * mm});
            skCircle(sketch, "E2.17.12.0", {"center": v(-59.32, -3.4) * mm, "radius": 6 * mm});
            skCircle(sketch, "E2.17.13.0", {"center": v(-59.32, -23.4) * mm, "radius": 6 * mm});
            skCircle(sketch, "E2.17.14.0", {"center": v(-59.32, -43.4) * mm, "radius": 6 * mm});
            skCircle(sketch, "E2.17.15.0", {"center": v(-59.32, -63.4) * mm, "radius": 6 * mm});
            skCircle(sketch, "E2.17.16.0", {"center": v(-59.32, -83.4) * mm, "radius": 6 * mm});
            skCircle(sketch, "E2.17.17.0", {"center": v(-59.32, -103.4) * mm, "radius": 6 * mm});
            skCircle(sketch, "E2.17.18.0", {"center": v(-59.32, -123.4) * mm, "radius": 6 * mm});
            skCircle(sketch, "E2.17.19.0", {"center": v(-59.32, -143.4) * mm, "radius": 6 * mm});
            skCircle(sketch, "E2.17.20.0", {"center": v(-59.32, -163.4) * mm, "radius": 6 * mm});
            skCircle(sketch, "E2.17.21.0", {"center": v(-59.32, -183.4) * mm, "radius": 6 * mm});
            skCircle(sketch, "E2.17.22.0", {"center": v(-59.32, -203.4) * mm, "radius": 6 * mm});
            skCircle(sketch, "E2.17.23.0", {"center": v(-59.32, -223.4) * mm, "radius": 6 * mm});
            skCircle(sketch, "E2.17.24.0", {"center": v(-59.32, -243.4) * mm, "radius": 6 * mm});
            skCircle(sketch, "E2.17.25.0", {"center": v(-59.32, -263.4) * mm, "radius": 6 * mm});
            skCircle(sketch, "E2.17.26.0", {"center": v(-59.32, -283.4) * mm, "radius": 6 * mm});
            skCircle(sketch, "E2.17.27.0", {"center": v(-59.32, -303.4) * mm, "radius": 6 * mm});
            skCircle(sketch, "E2.17.28.0", {"center": v(-59.32, -323.4) * mm, "radius": 6 * mm});
            skCircle(sketch, "E2.17.29.0", {"center": v(-59.32, -343.4) * mm, "radius": 6 * mm});
            skCircle(sketch, "E2.17.30.0", {"center": v(-59.32, -363.4) * mm, "radius": 6 * mm});
            skCircle(sketch, "E2.17.31.0", {"center": v(-59.32, -383.4) * mm, "radius": 6 * mm});
            skCircle(sketch, "E2.17.32.0", {"center": v(-59.32, -403.4) * mm, "radius": 6 * mm});
            skCircle(sketch, "E2.17.33.0", {"center": v(-59.32, -423.4) * mm, "radius": 6 * mm});
            skCircle(sketch, "E2.17.34.0", {"center": v(-59.32, -443.4) * mm, "radius": 6 * mm});
            skCircle(sketch, "E2.17.35.0", {"center": v(-59.32, -463.4) * mm, "radius": 6 * mm});
            skCircle(sketch, "E2.17.36.0", {"center": v(-59.32, -483.4) * mm, "radius": 6 * mm});
            skCircle(sketch, "E2.17.37.0", {"center": v(-59.32, -503.4) * mm, "radius": 6 * mm});
            skCircle(sketch, "E2.17.38.0", {"center": v(-59.32, -523.4) * mm, "radius": 6 * mm});
            skCircle(sketch, "E2.17.39.0", {"center": v(-59.32, -543.4) * mm, "radius": 6 * mm});
            skCircle(sketch, "E2.17.40.0", {"center": v(-59.32, -563.4) * mm, "radius": 6 * mm});
            skCircle(sketch, "E2.17.41.0", {"center": v(-59.32, -583.4) * mm, "radius": 6 * mm});
            skCircle(sketch, "E2.17.42.0", {"center": v(-59.32, -603.4) * mm, "radius": 6 * mm});
            skCircle(sketch, "E2.17.43.0", {"center": v(-59.32, -623.4) * mm, "radius": 6 * mm});
            skCircle(sketch, "E2.17.44.0", {"center": v(-59.32, -643.4) * mm, "radius": 6 * mm});
            skCircle(sketch, "E2.17.45.0", {"center": v(-59.32, -663.4) * mm, "radius": 6 * mm});
            skCircle(sketch, "E2.17.46.0", {"center": v(-59.32, -683.4) * mm, "radius": 6 * mm});
            skCircle(sketch, "E2.17.47.0", {"center": v(-59.32, -703.4) * mm, "radius": 6 * mm});
            skCircle(sketch, "E2.17.48.0", {"center": v(-59.32, -723.4) * mm, "radius": 6 * mm});
            skCircle(sketch, "E2.17.49.0", {"center": v(-59.32, -743.4) * mm, "radius": 6 * mm});
            skCircle(sketch, "E2.18.0.0", {"center": v(-39.32, 236.6) * mm, "radius": 6 * mm});
            skCircle(sketch, "E2.18.1.0", {"center": v(-39.32, 216.6) * mm, "radius": 6 * mm});
            skCircle(sketch, "E2.18.2.0", {"center": v(-39.32, 196.6) * mm, "radius": 6 * mm});
            skCircle(sketch, "E2.18.3.0", {"center": v(-39.32, 176.6) * mm, "radius": 6 * mm});
            skCircle(sketch, "E2.18.4.0", {"center": v(-39.32, 156.6) * mm, "radius": 6 * mm});
            skCircle(sketch, "E2.18.5.0", {"center": v(-39.32, 136.6) * mm, "radius": 6 * mm});
            skCircle(sketch, "E2.18.6.0", {"center": v(-39.32, 116.6) * mm, "radius": 6 * mm});
            skCircle(sketch, "E2.18.7.0", {"center": v(-39.32, 96.6) * mm, "radius": 6 * mm});
            skCircle(sketch, "E2.18.8.0", {"center": v(-39.32, 76.6) * mm, "radius": 6 * mm});
            skCircle(sketch, "E2.18.9.0", {"center": v(-39.32, 56.6) * mm, "radius": 6 * mm});
            skCircle(sketch, "E2.18.10.0", {"center": v(-39.32, 36.6) * mm, "radius": 6 * mm});
            skCircle(sketch, "E2.18.11.0", {"center": v(-39.32, 16.6) * mm, "radius": 6 * mm});
            skCircle(sketch, "E2.18.12.0", {"center": v(-39.32, -3.4) * mm, "radius": 6 * mm});
            skCircle(sketch, "E2.18.13.0", {"center": v(-39.32, -23.4) * mm, "radius": 6 * mm});
            skCircle(sketch, "E2.18.14.0", {"center": v(-39.32, -43.4) * mm, "radius": 6 * mm});
            skCircle(sketch, "E2.18.15.0", {"center": v(-39.32, -63.4) * mm, "radius": 6 * mm});
            skCircle(sketch, "E2.18.16.0", {"center": v(-39.32, -83.4) * mm, "radius": 6 * mm});
            skCircle(sketch, "E2.18.17.0", {"center": v(-39.32, -103.4) * mm, "radius": 6 * mm});
            skCircle(sketch, "E2.18.18.0", {"center": v(-39.32, -123.4) * mm, "radius": 6 * mm});
            skCircle(sketch, "E2.18.19.0", {"center": v(-39.32, -143.4) * mm, "radius": 6 * mm});
            skCircle(sketch, "E2.18.20.0", {"center": v(-39.32, -163.4) * mm, "radius": 6 * mm});
            skCircle(sketch, "E2.18.21.0", {"center": v(-39.32, -183.4) * mm, "radius": 6 * mm});
            skCircle(sketch, "E2.18.22.0", {"center": v(-39.32, -203.4) * mm, "radius": 6 * mm});
            skCircle(sketch, "E2.18.23.0", {"center": v(-39.32, -223.4) * mm, "radius": 6 * mm});
            skCircle(sketch, "E2.18.24.0", {"center": v(-39.32, -243.4) * mm, "radius": 6 * mm});
            skCircle(sketch, "E2.18.25.0", {"center": v(-39.32, -263.4) * mm, "radius": 6 * mm});
            skCircle(sketch, "E2.18.26.0", {"center": v(-39.32, -283.4) * mm, "radius": 6 * mm});
            skCircle(sketch, "E2.18.27.0", {"center": v(-39.32, -303.4) * mm, "radius": 6 * mm});
            skCircle(sketch, "E2.18.28.0", {"center": v(-39.32, -323.4) * mm, "radius": 6 * mm});
            skCircle(sketch, "E2.18.29.0", {"center": v(-39.32, -343.4) * mm, "radius": 6 * mm});
            skCircle(sketch, "E2.18.30.0", {"center": v(-39.32, -363.4) * mm, "radius": 6 * mm});
            skCircle(sketch, "E2.18.31.0", {"center": v(-39.32, -383.4) * mm, "radius": 6 * mm});
            skCircle(sketch, "E2.18.32.0", {"center": v(-39.32, -403.4) * mm, "radius": 6 * mm});
            skCircle(sketch, "E2.18.33.0", {"center": v(-39.32, -423.4) * mm, "radius": 6 * mm});
            skCircle(sketch, "E2.18.34.0", {"center": v(-39.32, -443.4) * mm, "radius": 6 * mm});
            skCircle(sketch, "E2.18.35.0", {"center": v(-39.32, -463.4) * mm, "radius": 6 * mm});
            skCircle(sketch, "E2.18.36.0", {"center": v(-39.32, -483.4) * mm, "radius": 6 * mm});
            skCircle(sketch, "E2.18.37.0", {"center": v(-39.32, -503.4) * mm, "radius": 6 * mm});
            skCircle(sketch, "E2.18.38.0", {"center": v(-39.32, -523.4) * mm, "radius": 6 * mm});
            skCircle(sketch, "E2.18.39.0", {"center": v(-39.32, -543.4) * mm, "radius": 6 * mm});
            skCircle(sketch, "E2.18.40.0", {"center": v(-39.32, -563.4) * mm, "radius": 6 * mm});
            skCircle(sketch, "E2.18.41.0", {"center": v(-39.32, -583.4) * mm, "radius": 6 * mm});
            skCircle(sketch, "E2.18.42.0", {"center": v(-39.32, -603.4) * mm, "radius": 6 * mm});
            skCircle(sketch, "E2.18.43.0", {"center": v(-39.32, -623.4) * mm, "radius": 6 * mm});
            skCircle(sketch, "E2.18.44.0", {"center": v(-39.32, -643.4) * mm, "radius": 6 * mm});
            skCircle(sketch, "E2.18.45.0", {"center": v(-39.32, -663.4) * mm, "radius": 6 * mm});
            skCircle(sketch, "E2.18.46.0", {"center": v(-39.32, -683.4) * mm, "radius": 6 * mm});
            skCircle(sketch, "E2.18.47.0", {"center": v(-39.32, -703.4) * mm, "radius": 6 * mm});
            skCircle(sketch, "E2.18.48.0", {"center": v(-39.32, -723.4) * mm, "radius": 6 * mm});
            skCircle(sketch, "E2.18.49.0", {"center": v(-39.32, -743.4) * mm, "radius": 6 * mm});
            skCircle(sketch, "E2.19.0.0", {"center": v(-19.32, 236.6) * mm, "radius": 6 * mm});
            skCircle(sketch, "E2.19.1.0", {"center": v(-19.32, 216.6) * mm, "radius": 6 * mm});
            skCircle(sketch, "E2.19.2.0", {"center": v(-19.32, 196.6) * mm, "radius": 6 * mm});
            skCircle(sketch, "E2.19.3.0", {"center": v(-19.32, 176.6) * mm, "radius": 6 * mm});
            skCircle(sketch, "E2.19.4.0", {"center": v(-19.32, 156.6) * mm, "radius": 6 * mm});
            skCircle(sketch, "E2.19.5.0", {"center": v(-19.32, 136.6) * mm, "radius": 6 * mm});
            skCircle(sketch, "E2.19.6.0", {"center": v(-19.32, 116.6) * mm, "radius": 6 * mm});
            skCircle(sketch, "E2.19.7.0", {"center": v(-19.32, 96.6) * mm, "radius": 6 * mm});
            skCircle(sketch, "E2.19.8.0", {"center": v(-19.32, 76.6) * mm, "radius": 6 * mm});
            skCircle(sketch, "E2.19.9.0", {"center": v(-19.32, 56.6) * mm, "radius": 6 * mm});
            skCircle(sketch, "E2.19.10.0", {"center": v(-19.32, 36.6) * mm, "radius": 6 * mm});
            skCircle(sketch, "E2.19.11.0", {"center": v(-19.32, 16.6) * mm, "radius": 6 * mm});
            skCircle(sketch, "E2.19.12.0", {"center": v(-19.32, -3.4) * mm, "radius": 6 * mm});
            skCircle(sketch, "E2.19.13.0", {"center": v(-19.32, -23.4) * mm, "radius": 6 * mm});
            skCircle(sketch, "E2.19.14.0", {"center": v(-19.32, -43.4) * mm, "radius": 6 * mm});
            skCircle(sketch, "E2.19.15.0", {"center": v(-19.32, -63.4) * mm, "radius": 6 * mm});
            skCircle(sketch, "E2.19.16.0", {"center": v(-19.32, -83.4) * mm, "radius": 6 * mm});
            skCircle(sketch, "E2.19.17.0", {"center": v(-19.32, -103.4) * mm, "radius": 6 * mm});
            skCircle(sketch, "E2.19.18.0", {"center": v(-19.32, -123.4) * mm, "radius": 6 * mm});
            skCircle(sketch, "E2.19.19.0", {"center": v(-19.32, -143.4) * mm, "radius": 6 * mm});
            skCircle(sketch, "E2.19.20.0", {"center": v(-19.32, -163.4) * mm, "radius": 6 * mm});
            skCircle(sketch, "E2.19.21.0", {"center": v(-19.32, -183.4) * mm, "radius": 6 * mm});
            skCircle(sketch, "E2.19.22.0", {"center": v(-19.32, -203.4) * mm, "radius": 6 * mm});
            skCircle(sketch, "E2.19.23.0", {"center": v(-19.32, -223.4) * mm, "radius": 6 * mm});
            skCircle(sketch, "E2.19.24.0", {"center": v(-19.32, -243.4) * mm, "radius": 6 * mm});
            skCircle(sketch, "E2.19.25.0", {"center": v(-19.32, -263.4) * mm, "radius": 6 * mm});
            skCircle(sketch, "E2.19.26.0", {"center": v(-19.32, -283.4) * mm, "radius": 6 * mm});
            skCircle(sketch, "E2.19.27.0", {"center": v(-19.32, -303.4) * mm, "radius": 6 * mm});
            skCircle(sketch, "E2.19.28.0", {"center": v(-19.32, -323.4) * mm, "radius": 6 * mm});
            skCircle(sketch, "E2.19.29.0", {"center": v(-19.32, -343.4) * mm, "radius": 6 * mm});
            skCircle(sketch, "E2.19.30.0", {"center": v(-19.32, -363.4) * mm, "radius": 6 * mm});
            skCircle(sketch, "E2.19.31.0", {"center": v(-19.32, -383.4) * mm, "radius": 6 * mm});
            skCircle(sketch, "E2.19.32.0", {"center": v(-19.32, -403.4) * mm, "radius": 6 * mm});
            skCircle(sketch, "E2.19.33.0", {"center": v(-19.32, -423.4) * mm, "radius": 6 * mm});
            skCircle(sketch, "E2.19.34.0", {"center": v(-19.32, -443.4) * mm, "radius": 6 * mm});
            skCircle(sketch, "E2.19.35.0", {"center": v(-19.32, -463.4) * mm, "radius": 6 * mm});
            skCircle(sketch, "E2.19.36.0", {"center": v(-19.32, -483.4) * mm, "radius": 6 * mm});
            skCircle(sketch, "E2.19.37.0", {"center": v(-19.32, -503.4) * mm, "radius": 6 * mm});
            skCircle(sketch, "E2.19.38.0", {"center": v(-19.32, -523.4) * mm, "radius": 6 * mm});
            skCircle(sketch, "E2.19.39.0", {"center": v(-19.32, -543.4) * mm, "radius": 6 * mm});
            skCircle(sketch, "E2.19.40.0", {"center": v(-19.32, -563.4) * mm, "radius": 6 * mm});
            skCircle(sketch, "E2.19.41.0", {"center": v(-19.32, -583.4) * mm, "radius": 6 * mm});
            skCircle(sketch, "E2.19.42.0", {"center": v(-19.32, -603.4) * mm, "radius": 6 * mm});
            skCircle(sketch, "E2.19.43.0", {"center": v(-19.32, -623.4) * mm, "radius": 6 * mm});
            skCircle(sketch, "E2.19.44.0", {"center": v(-19.32, -643.4) * mm, "radius": 6 * mm});
            skCircle(sketch, "E2.19.45.0", {"center": v(-19.32, -663.4) * mm, "radius": 6 * mm});
            skCircle(sketch, "E2.19.46.0", {"center": v(-19.32, -683.4) * mm, "radius": 6 * mm});
            skCircle(sketch, "E2.19.47.0", {"center": v(-19.32, -703.4) * mm, "radius": 6 * mm});
            skCircle(sketch, "E2.19.48.0", {"center": v(-19.32, -723.4) * mm, "radius": 6 * mm});
            skCircle(sketch, "E2.19.49.0", {"center": v(-19.32, -743.4) * mm, "radius": 6 * mm});
            skCircle(sketch, "E2.20.0.0", {"center": v(0.68, 236.6) * mm, "radius": 6 * mm});
            skCircle(sketch, "E2.20.1.0", {"center": v(0.68, 216.6) * mm, "radius": 6 * mm});
            skCircle(sketch, "E2.20.2.0", {"center": v(0.68, 196.6) * mm, "radius": 6 * mm});
            skCircle(sketch, "E2.20.3.0", {"center": v(0.68, 176.6) * mm, "radius": 6 * mm});
            skCircle(sketch, "E2.20.4.0", {"center": v(0.68, 156.6) * mm, "radius": 6 * mm});
            skCircle(sketch, "E2.20.5.0", {"center": v(0.68, 136.6) * mm, "radius": 6 * mm});
            skCircle(sketch, "E2.20.6.0", {"center": v(0.68, 116.6) * mm, "radius": 6 * mm});
            skCircle(sketch, "E2.20.7.0", {"center": v(0.68, 96.6) * mm, "radius": 6 * mm});
            skCircle(sketch, "E2.20.8.0", {"center": v(0.68, 76.6) * mm, "radius": 6 * mm});
            skCircle(sketch, "E2.20.9.0", {"center": v(0.68, 56.6) * mm, "radius": 6 * mm});
            skCircle(sketch, "E2.20.10.0", {"center": v(0.68, 36.6) * mm, "radius": 6 * mm});
            skCircle(sketch, "E2.20.11.0", {"center": v(0.68, 16.6) * mm, "radius": 6 * mm});
            skCircle(sketch, "E2.20.12.0", {"center": v(0.68, -3.4) * mm, "radius": 6 * mm});
            skCircle(sketch, "E2.20.13.0", {"center": v(0.68, -23.4) * mm, "radius": 6 * mm});
            skCircle(sketch, "E2.20.14.0", {"center": v(0.68, -43.4) * mm, "radius": 6 * mm});
            skCircle(sketch, "E2.20.15.0", {"center": v(0.68, -63.4) * mm, "radius": 6 * mm});
            skCircle(sketch, "E2.20.16.0", {"center": v(0.68, -83.4) * mm, "radius": 6 * mm});
            skCircle(sketch, "E2.20.17.0", {"center": v(0.68, -103.4) * mm, "radius": 6 * mm});
            skCircle(sketch, "E2.20.18.0", {"center": v(0.68, -123.4) * mm, "radius": 6 * mm});
            skCircle(sketch, "E2.20.19.0", {"center": v(0.68, -143.4) * mm, "radius": 6 * mm});
            skCircle(sketch, "E2.20.20.0", {"center": v(0.68, -163.4) * mm, "radius": 6 * mm});
            skCircle(sketch, "E2.20.21.0", {"center": v(0.68, -183.4) * mm, "radius": 6 * mm});
            skCircle(sketch, "E2.20.22.0", {"center": v(0.68, -203.4) * mm, "radius": 6 * mm});
            skCircle(sketch, "E2.20.23.0", {"center": v(0.68, -223.4) * mm, "radius": 6 * mm});
            skCircle(sketch, "E2.20.24.0", {"center": v(0.68, -243.4) * mm, "radius": 6 * mm});
            skCircle(sketch, "E2.20.25.0", {"center": v(0.68, -263.4) * mm, "radius": 6 * mm});
            skCircle(sketch, "E2.20.26.0", {"center": v(0.68, -283.4) * mm, "radius": 6 * mm});
            skCircle(sketch, "E2.20.27.0", {"center": v(0.68, -303.4) * mm, "radius": 6 * mm});
            skCircle(sketch, "E2.20.28.0", {"center": v(0.68, -323.4) * mm, "radius": 6 * mm});
            skCircle(sketch, "E2.20.29.0", {"center": v(0.68, -343.4) * mm, "radius": 6 * mm});
            skCircle(sketch, "E2.20.30.0", {"center": v(0.68, -363.4) * mm, "radius": 6 * mm});
            skCircle(sketch, "E2.20.31.0", {"center": v(0.68, -383.4) * mm, "radius": 6 * mm});
            skCircle(sketch, "E2.20.32.0", {"center": v(0.68, -403.4) * mm, "radius": 6 * mm});
            skCircle(sketch, "E2.20.33.0", {"center": v(0.68, -423.4) * mm, "radius": 6 * mm});
            skCircle(sketch, "E2.20.34.0", {"center": v(0.68, -443.4) * mm, "radius": 6 * mm});
            skCircle(sketch, "E2.20.35.0", {"center": v(0.68, -463.4) * mm, "radius": 6 * mm});
            skCircle(sketch, "E2.20.36.0", {"center": v(0.68, -483.4) * mm, "radius": 6 * mm});
            skCircle(sketch, "E2.20.37.0", {"center": v(0.68, -503.4) * mm, "radius": 6 * mm});
            skCircle(sketch, "E2.20.38.0", {"center": v(0.68, -523.4) * mm, "radius": 6 * mm});
            skCircle(sketch, "E2.20.39.0", {"center": v(0.68, -543.4) * mm, "radius": 6 * mm});
            skCircle(sketch, "E2.20.40.0", {"center": v(0.68, -563.4) * mm, "radius": 6 * mm});
            skCircle(sketch, "E2.20.41.0", {"center": v(0.68, -583.4) * mm, "radius": 6 * mm});
            skCircle(sketch, "E2.20.42.0", {"center": v(0.68, -603.4) * mm, "radius": 6 * mm});
            skCircle(sketch, "E2.20.43.0", {"center": v(0.68, -623.4) * mm, "radius": 6 * mm});
            skCircle(sketch, "E2.20.44.0", {"center": v(0.68, -643.4) * mm, "radius": 6 * mm});
            skCircle(sketch, "E2.20.45.0", {"center": v(0.68, -663.4) * mm, "radius": 6 * mm});
            skCircle(sketch, "E2.20.46.0", {"center": v(0.68, -683.4) * mm, "radius": 6 * mm});
            skCircle(sketch, "E2.20.47.0", {"center": v(0.68, -703.4) * mm, "radius": 6 * mm});
            skCircle(sketch, "E2.20.48.0", {"center": v(0.68, -723.4) * mm, "radius": 6 * mm});
            skCircle(sketch, "E2.20.49.0", {"center": v(0.68, -743.4) * mm, "radius": 6 * mm});
            skCircle(sketch, "E2.21.0.0", {"center": v(20.68, 236.6) * mm, "radius": 6 * mm});
            skCircle(sketch, "E2.21.1.0", {"center": v(20.68, 216.6) * mm, "radius": 6 * mm});
            skCircle(sketch, "E2.21.2.0", {"center": v(20.68, 196.6) * mm, "radius": 6 * mm});
            skCircle(sketch, "E2.21.3.0", {"center": v(20.68, 176.6) * mm, "radius": 6 * mm});
            skCircle(sketch, "E2.21.4.0", {"center": v(20.68, 156.6) * mm, "radius": 6 * mm});
            skCircle(sketch, "E2.21.5.0", {"center": v(20.68, 136.6) * mm, "radius": 6 * mm});
            skCircle(sketch, "E2.21.6.0", {"center": v(20.68, 116.6) * mm, "radius": 6 * mm});
            skCircle(sketch, "E2.21.7.0", {"center": v(20.68, 96.6) * mm, "radius": 6 * mm});
            skCircle(sketch, "E2.21.8.0", {"center": v(20.68, 76.6) * mm, "radius": 6 * mm});
            skCircle(sketch, "E2.21.9.0", {"center": v(20.68, 56.6) * mm, "radius": 6 * mm});
            skCircle(sketch, "E2.21.10.0", {"center": v(20.68, 36.6) * mm, "radius": 6 * mm});
            skCircle(sketch, "E2.21.11.0", {"center": v(20.68, 16.6) * mm, "radius": 6 * mm});
            skCircle(sketch, "E2.21.12.0", {"center": v(20.68, -3.4) * mm, "radius": 6 * mm});
            skCircle(sketch, "E2.21.13.0", {"center": v(20.68, -23.4) * mm, "radius": 6 * mm});
            skCircle(sketch, "E2.21.14.0", {"center": v(20.68, -43.4) * mm, "radius": 6 * mm});
            skCircle(sketch, "E2.21.15.0", {"center": v(20.68, -63.4) * mm, "radius": 6 * mm});
            skCircle(sketch, "E2.21.16.0", {"center": v(20.68, -83.4) * mm, "radius": 6 * mm});
            skCircle(sketch, "E2.21.17.0", {"center": v(20.68, -103.4) * mm, "radius": 6 * mm});
            skCircle(sketch, "E2.21.18.0", {"center": v(20.68, -123.4) * mm, "radius": 6 * mm});
            skCircle(sketch, "E2.21.19.0", {"center": v(20.68, -143.4) * mm, "radius": 6 * mm});
            skCircle(sketch, "E2.21.20.0", {"center": v(20.68, -163.4) * mm, "radius": 6 * mm});
            skCircle(sketch, "E2.21.21.0", {"center": v(20.68, -183.4) * mm, "radius": 6 * mm});
            skCircle(sketch, "E2.21.22.0", {"center": v(20.68, -203.4) * mm, "radius": 6 * mm});
            skCircle(sketch, "E2.21.23.0", {"center": v(20.68, -223.4) * mm, "radius": 6 * mm});
            skCircle(sketch, "E2.21.24.0", {"center": v(20.68, -243.4) * mm, "radius": 6 * mm});
            skCircle(sketch, "E2.21.25.0", {"center": v(20.68, -263.4) * mm, "radius": 6 * mm});
            skCircle(sketch, "E2.21.26.0", {"center": v(20.68, -283.4) * mm, "radius": 6 * mm});
            skCircle(sketch, "E2.21.27.0", {"center": v(20.68, -303.4) * mm, "radius": 6 * mm});
            skCircle(sketch, "E2.21.28.0", {"center": v(20.68, -323.4) * mm, "radius": 6 * mm});
            skCircle(sketch, "E2.21.29.0", {"center": v(20.68, -343.4) * mm, "radius": 6 * mm});
            skCircle(sketch, "E2.21.30.0", {"center": v(20.68, -363.4) * mm, "radius": 6 * mm});
            skCircle(sketch, "E2.21.31.0", {"center": v(20.68, -383.4) * mm, "radius": 6 * mm});
            skCircle(sketch, "E2.21.32.0", {"center": v(20.68, -403.4) * mm, "radius": 6 * mm});
            skCircle(sketch, "E2.21.33.0", {"center": v(20.68, -423.4) * mm, "radius": 6 * mm});
            skCircle(sketch, "E2.21.34.0", {"center": v(20.68, -443.4) * mm, "radius": 6 * mm});
            skCircle(sketch, "E2.21.35.0", {"center": v(20.68, -463.4) * mm, "radius": 6 * mm});
            skCircle(sketch, "E2.21.36.0", {"center": v(20.68, -483.4) * mm, "radius": 6 * mm});
            skCircle(sketch, "E2.21.37.0", {"center": v(20.68, -503.4) * mm, "radius": 6 * mm});
            skCircle(sketch, "E2.21.38.0", {"center": v(20.68, -523.4) * mm, "radius": 6 * mm});
            skCircle(sketch, "E2.21.39.0", {"center": v(20.68, -543.4) * mm, "radius": 6 * mm});
            skCircle(sketch, "E2.21.40.0", {"center": v(20.68, -563.4) * mm, "radius": 6 * mm});
            skCircle(sketch, "E2.21.41.0", {"center": v(20.68, -583.4) * mm, "radius": 6 * mm});
            skCircle(sketch, "E2.21.42.0", {"center": v(20.68, -603.4) * mm, "radius": 6 * mm});
            skCircle(sketch, "E2.21.43.0", {"center": v(20.68, -623.4) * mm, "radius": 6 * mm});
            skCircle(sketch, "E2.21.44.0", {"center": v(20.68, -643.4) * mm, "radius": 6 * mm});
            skCircle(sketch, "E2.21.45.0", {"center": v(20.68, -663.4) * mm, "radius": 6 * mm});
            skCircle(sketch, "E2.21.46.0", {"center": v(20.68, -683.4) * mm, "radius": 6 * mm});
            skCircle(sketch, "E2.21.47.0", {"center": v(20.68, -703.4) * mm, "radius": 6 * mm});
            skCircle(sketch, "E2.21.48.0", {"center": v(20.68, -723.4) * mm, "radius": 6 * mm});
            skCircle(sketch, "E2.21.49.0", {"center": v(20.68, -743.4) * mm, "radius": 6 * mm});
            skCircle(sketch, "E2.22.0.0", {"center": v(40.68, 236.6) * mm, "radius": 6 * mm});
            skCircle(sketch, "E2.22.1.0", {"center": v(40.68, 216.6) * mm, "radius": 6 * mm});
            skCircle(sketch, "E2.22.2.0", {"center": v(40.68, 196.6) * mm, "radius": 6 * mm});
            skCircle(sketch, "E2.22.3.0", {"center": v(40.68, 176.6) * mm, "radius": 6 * mm});
            skCircle(sketch, "E2.22.4.0", {"center": v(40.68, 156.6) * mm, "radius": 6 * mm});
            skCircle(sketch, "E2.22.5.0", {"center": v(40.68, 136.6) * mm, "radius": 6 * mm});
            skCircle(sketch, "E2.22.6.0", {"center": v(40.68, 116.6) * mm, "radius": 6 * mm});
            skCircle(sketch, "E2.22.7.0", {"center": v(40.68, 96.6) * mm, "radius": 6 * mm});
            skCircle(sketch, "E2.22.8.0", {"center": v(40.68, 76.6) * mm, "radius": 6 * mm});
            skCircle(sketch, "E2.22.9.0", {"center": v(40.68, 56.6) * mm, "radius": 6 * mm});
            skCircle(sketch, "E2.22.10.0", {"center": v(40.68, 36.6) * mm, "radius": 6 * mm});
            skCircle(sketch, "E2.22.11.0", {"center": v(40.68, 16.6) * mm, "radius": 6 * mm});
            skCircle(sketch, "E2.22.12.0", {"center": v(40.68, -3.4) * mm, "radius": 6 * mm});
            skCircle(sketch, "E2.22.13.0", {"center": v(40.68, -23.4) * mm, "radius": 6 * mm});
            skCircle(sketch, "E2.22.14.0", {"center": v(40.68, -43.4) * mm, "radius": 6 * mm});
            skCircle(sketch, "E2.22.15.0", {"center": v(40.68, -63.4) * mm, "radius": 6 * mm});
            skCircle(sketch, "E2.22.16.0", {"center": v(40.68, -83.4) * mm, "radius": 6 * mm});
            skCircle(sketch, "E2.22.17.0", {"center": v(40.68, -103.4) * mm, "radius": 6 * mm});
            skCircle(sketch, "E2.22.18.0", {"center": v(40.68, -123.4) * mm, "radius": 6 * mm});
            skCircle(sketch, "E2.22.19.0", {"center": v(40.68, -143.4) * mm, "radius": 6 * mm});
            skCircle(sketch, "E2.22.20.0", {"center": v(40.68, -163.4) * mm, "radius": 6 * mm});
            skCircle(sketch, "E2.22.21.0", {"center": v(40.68, -183.4) * mm, "radius": 6 * mm});
            skCircle(sketch, "E2.22.22.0", {"center": v(40.68, -203.4) * mm, "radius": 6 * mm});
            skCircle(sketch, "E2.22.23.0", {"center": v(40.68, -223.4) * mm, "radius": 6 * mm});
            skCircle(sketch, "E2.22.24.0", {"center": v(40.68, -243.4) * mm, "radius": 6 * mm});
            skCircle(sketch, "E2.22.25.0", {"center": v(40.68, -263.4) * mm, "radius": 6 * mm});
            skCircle(sketch, "E2.22.26.0", {"center": v(40.68, -283.4) * mm, "radius": 6 * mm});
            skCircle(sketch, "E2.22.27.0", {"center": v(40.68, -303.4) * mm, "radius": 6 * mm});
            skCircle(sketch, "E2.22.28.0", {"center": v(40.68, -323.4) * mm, "radius": 6 * mm});
            skCircle(sketch, "E2.22.29.0", {"center": v(40.68, -343.4) * mm, "radius": 6 * mm});
            skCircle(sketch, "E2.22.30.0", {"center": v(40.68, -363.4) * mm, "radius": 6 * mm});
            skCircle(sketch, "E2.22.31.0", {"center": v(40.68, -383.4) * mm, "radius": 6 * mm});
            skCircle(sketch, "E2.22.32.0", {"center": v(40.68, -403.4) * mm, "radius": 6 * mm});
            skCircle(sketch, "E2.22.33.0", {"center": v(40.68, -423.4) * mm, "radius": 6 * mm});
            skCircle(sketch, "E2.22.34.0", {"center": v(40.68, -443.4) * mm, "radius": 6 * mm});
            skCircle(sketch, "E2.22.35.0", {"center": v(40.68, -463.4) * mm, "radius": 6 * mm});
            skCircle(sketch, "E2.22.36.0", {"center": v(40.68, -483.4) * mm, "radius": 6 * mm});
            skCircle(sketch, "E2.22.37.0", {"center": v(40.68, -503.4) * mm, "radius": 6 * mm});
            skCircle(sketch, "E2.22.38.0", {"center": v(40.68, -523.4) * mm, "radius": 6 * mm});
            skCircle(sketch, "E2.22.39.0", {"center": v(40.68, -543.4) * mm, "radius": 6 * mm});
            skCircle(sketch, "E2.22.40.0", {"center": v(40.68, -563.4) * mm, "radius": 6 * mm});
            skCircle(sketch, "E2.22.41.0", {"center": v(40.68, -583.4) * mm, "radius": 6 * mm});
            skCircle(sketch, "E2.22.42.0", {"center": v(40.68, -603.4) * mm, "radius": 6 * mm});
            skCircle(sketch, "E2.22.43.0", {"center": v(40.68, -623.4) * mm, "radius": 6 * mm});
            skCircle(sketch, "E2.22.44.0", {"center": v(40.68, -643.4) * mm, "radius": 6 * mm});
            skCircle(sketch, "E2.22.45.0", {"center": v(40.68, -663.4) * mm, "radius": 6 * mm});
            skCircle(sketch, "E2.22.46.0", {"center": v(40.68, -683.4) * mm, "radius": 6 * mm});
            skCircle(sketch, "E2.22.47.0", {"center": v(40.68, -703.4) * mm, "radius": 6 * mm});
            skCircle(sketch, "E2.22.48.0", {"center": v(40.68, -723.4) * mm, "radius": 6 * mm});
            skCircle(sketch, "E2.22.49.0", {"center": v(40.68, -743.4) * mm, "radius": 6 * mm});
            skCircle(sketch, "E2.23.0.0", {"center": v(60.68, 236.6) * mm, "radius": 6 * mm});
            skCircle(sketch, "E2.23.1.0", {"center": v(60.68, 216.6) * mm, "radius": 6 * mm});
            skCircle(sketch, "E2.23.2.0", {"center": v(60.68, 196.6) * mm, "radius": 6 * mm});
            skCircle(sketch, "E2.23.3.0", {"center": v(60.68, 176.6) * mm, "radius": 6 * mm});
            skCircle(sketch, "E2.23.4.0", {"center": v(60.68, 156.6) * mm, "radius": 6 * mm});
            skCircle(sketch, "E2.23.5.0", {"center": v(60.68, 136.6) * mm, "radius": 6 * mm});
            skCircle(sketch, "E2.23.6.0", {"center": v(60.68, 116.6) * mm, "radius": 6 * mm});
            skCircle(sketch, "E2.23.7.0", {"center": v(60.68, 96.6) * mm, "radius": 6 * mm});
            skCircle(sketch, "E2.23.8.0", {"center": v(60.68, 76.6) * mm, "radius": 6 * mm});
            skCircle(sketch, "E2.23.9.0", {"center": v(60.68, 56.6) * mm, "radius": 6 * mm});
            skCircle(sketch, "E2.23.10.0", {"center": v(60.68, 36.6) * mm, "radius": 6 * mm});
            skCircle(sketch, "E2.23.11.0", {"center": v(60.68, 16.6) * mm, "radius": 6 * mm});
            skCircle(sketch, "E2.23.12.0", {"center": v(60.68, -3.4) * mm, "radius": 6 * mm});
            skCircle(sketch, "E2.23.13.0", {"center": v(60.68, -23.4) * mm, "radius": 6 * mm});
            skCircle(sketch, "E2.23.14.0", {"center": v(60.68, -43.4) * mm, "radius": 6 * mm});
            skCircle(sketch, "E2.23.15.0", {"center": v(60.68, -63.4) * mm, "radius": 6 * mm});
            skCircle(sketch, "E2.23.16.0", {"center": v(60.68, -83.4) * mm, "radius": 6 * mm});
            skCircle(sketch, "E2.23.17.0", {"center": v(60.68, -103.4) * mm, "radius": 6 * mm});
            skCircle(sketch, "E2.23.18.0", {"center": v(60.68, -123.4) * mm, "radius": 6 * mm});
            skCircle(sketch, "E2.23.19.0", {"center": v(60.68, -143.4) * mm, "radius": 6 * mm});
            skCircle(sketch, "E2.23.20.0", {"center": v(60.68, -163.4) * mm, "radius": 6 * mm});
            skCircle(sketch, "E2.23.21.0", {"center": v(60.68, -183.4) * mm, "radius": 6 * mm});
            skCircle(sketch, "E2.23.22.0", {"center": v(60.68, -203.4) * mm, "radius": 6 * mm});
            skCircle(sketch, "E2.23.23.0", {"center": v(60.68, -223.4) * mm, "radius": 6 * mm});
            skCircle(sketch, "E2.23.24.0", {"center": v(60.68, -243.4) * mm, "radius": 6 * mm});
            skCircle(sketch, "E2.23.25.0", {"center": v(60.68, -263.4) * mm, "radius": 6 * mm});
            skCircle(sketch, "E2.23.26.0", {"center": v(60.68, -283.4) * mm, "radius": 6 * mm});
            skCircle(sketch, "E2.23.27.0", {"center": v(60.68, -303.4) * mm, "radius": 6 * mm});
            skCircle(sketch, "E2.23.28.0", {"center": v(60.68, -323.4) * mm, "radius": 6 * mm});
            skCircle(sketch, "E2.23.29.0", {"center": v(60.68, -343.4) * mm, "radius": 6 * mm});
            skCircle(sketch, "E2.23.30.0", {"center": v(60.68, -363.4) * mm, "radius": 6 * mm});
            skCircle(sketch, "E2.23.31.0", {"center": v(60.68, -383.4) * mm, "radius": 6 * mm});
            skCircle(sketch, "E2.23.32.0", {"center": v(60.68, -403.4) * mm, "radius": 6 * mm});
            skCircle(sketch, "E2.23.33.0", {"center": v(60.68, -423.4) * mm, "radius": 6 * mm});
            skCircle(sketch, "E2.23.34.0", {"center": v(60.68, -443.4) * mm, "radius": 6 * mm});
            skCircle(sketch, "E2.23.35.0", {"center": v(60.68, -463.4) * mm, "radius": 6 * mm});
            skCircle(sketch, "E2.23.36.0", {"center": v(60.68, -483.4) * mm, "radius": 6 * mm});
            skCircle(sketch, "E2.23.37.0", {"center": v(60.68, -503.4) * mm, "radius": 6 * mm});
            skCircle(sketch, "E2.23.38.0", {"center": v(60.68, -523.4) * mm, "radius": 6 * mm});
            skCircle(sketch, "E2.23.39.0", {"center": v(60.68, -543.4) * mm, "radius": 6 * mm});
            skCircle(sketch, "E2.23.40.0", {"center": v(60.68, -563.4) * mm, "radius": 6 * mm});
            skCircle(sketch, "E2.23.41.0", {"center": v(60.68, -583.4) * mm, "radius": 6 * mm});
            skCircle(sketch, "E2.23.42.0", {"center": v(60.68, -603.4) * mm, "radius": 6 * mm});
            skCircle(sketch, "E2.23.43.0", {"center": v(60.68, -623.4) * mm, "radius": 6 * mm});
            skCircle(sketch, "E2.23.44.0", {"center": v(60.68, -643.4) * mm, "radius": 6 * mm});
            skCircle(sketch, "E2.23.45.0", {"center": v(60.68, -663.4) * mm, "radius": 6 * mm});
            skCircle(sketch, "E2.23.46.0", {"center": v(60.68, -683.4) * mm, "radius": 6 * mm});
            skCircle(sketch, "E2.23.47.0", {"center": v(60.68, -703.4) * mm, "radius": 6 * mm});
            skCircle(sketch, "E2.23.48.0", {"center": v(60.68, -723.4) * mm, "radius": 6 * mm});
            skCircle(sketch, "E2.23.49.0", {"center": v(60.68, -743.4) * mm, "radius": 6 * mm});
            skCircle(sketch, "E2.24.0.0", {"center": v(80.68, 236.6) * mm, "radius": 6 * mm});
            skCircle(sketch, "E2.24.1.0", {"center": v(80.68, 216.6) * mm, "radius": 6 * mm});
            skCircle(sketch, "E2.24.2.0", {"center": v(80.68, 196.6) * mm, "radius": 6 * mm});
            skCircle(sketch, "E2.24.3.0", {"center": v(80.68, 176.6) * mm, "radius": 6 * mm});
            skCircle(sketch, "E2.24.4.0", {"center": v(80.68, 156.6) * mm, "radius": 6 * mm});
            skCircle(sketch, "E2.24.5.0", {"center": v(80.68, 136.6) * mm, "radius": 6 * mm});
            skCircle(sketch, "E2.24.6.0", {"center": v(80.68, 116.6) * mm, "radius": 6 * mm});
            skCircle(sketch, "E2.24.7.0", {"center": v(80.68, 96.6) * mm, "radius": 6 * mm});
            skCircle(sketch, "E2.24.8.0", {"center": v(80.68, 76.6) * mm, "radius": 6 * mm});
            skCircle(sketch, "E2.24.9.0", {"center": v(80.68, 56.6) * mm, "radius": 6 * mm});
            skCircle(sketch, "E2.24.10.0", {"center": v(80.68, 36.6) * mm, "radius": 6 * mm});
            skCircle(sketch, "E2.24.11.0", {"center": v(80.68, 16.6) * mm, "radius": 6 * mm});
            skCircle(sketch, "E2.24.12.0", {"center": v(80.68, -3.4) * mm, "radius": 6 * mm});
            skCircle(sketch, "E2.24.13.0", {"center": v(80.68, -23.4) * mm, "radius": 6 * mm});
            skCircle(sketch, "E2.24.14.0", {"center": v(80.68, -43.4) * mm, "radius": 6 * mm});
            skCircle(sketch, "E2.24.15.0", {"center": v(80.68, -63.4) * mm, "radius": 6 * mm});
            skCircle(sketch, "E2.24.16.0", {"center": v(80.68, -83.4) * mm, "radius": 6 * mm});
            skCircle(sketch, "E2.24.17.0", {"center": v(80.68, -103.4) * mm, "radius": 6 * mm});
            skCircle(sketch, "E2.24.18.0", {"center": v(80.68, -123.4) * mm, "radius": 6 * mm});
            skCircle(sketch, "E2.24.19.0", {"center": v(80.68, -143.4) * mm, "radius": 6 * mm});
            skCircle(sketch, "E2.24.20.0", {"center": v(80.68, -163.4) * mm, "radius": 6 * mm});
            skCircle(sketch, "E2.24.21.0", {"center": v(80.68, -183.4) * mm, "radius": 6 * mm});
            skCircle(sketch, "E2.24.22.0", {"center": v(80.68, -203.4) * mm, "radius": 6 * mm});
            skCircle(sketch, "E2.24.23.0", {"center": v(80.68, -223.4) * mm, "radius": 6 * mm});
            skCircle(sketch, "E2.24.24.0", {"center": v(80.68, -243.4) * mm, "radius": 6 * mm});
            skCircle(sketch, "E2.24.25.0", {"center": v(80.68, -263.4) * mm, "radius": 6 * mm});
            skCircle(sketch, "E2.24.26.0", {"center": v(80.68, -283.4) * mm, "radius": 6 * mm});
            skCircle(sketch, "E2.24.27.0", {"center": v(80.68, -303.4) * mm, "radius": 6 * mm});
            skCircle(sketch, "E2.24.28.0", {"center": v(80.68, -323.4) * mm, "radius": 6 * mm});
            skCircle(sketch, "E2.24.29.0", {"center": v(80.68, -343.4) * mm, "radius": 6 * mm});
            skCircle(sketch, "E2.24.30.0", {"center": v(80.68, -363.4) * mm, "radius": 6 * mm});
            skCircle(sketch, "E2.24.31.0", {"center": v(80.68, -383.4) * mm, "radius": 6 * mm});
            skCircle(sketch, "E2.24.32.0", {"center": v(80.68, -403.4) * mm, "radius": 6 * mm});
            skCircle(sketch, "E2.24.33.0", {"center": v(80.68, -423.4) * mm, "radius": 6 * mm});
            skCircle(sketch, "E2.24.34.0", {"center": v(80.68, -443.4) * mm, "radius": 6 * mm});
            skCircle(sketch, "E2.24.35.0", {"center": v(80.68, -463.4) * mm, "radius": 6 * mm});
            skCircle(sketch, "E2.24.36.0", {"center": v(80.68, -483.4) * mm, "radius": 6 * mm});
            skCircle(sketch, "E2.24.37.0", {"center": v(80.68, -503.4) * mm, "radius": 6 * mm});
            skCircle(sketch, "E2.24.38.0", {"center": v(80.68, -523.4) * mm, "radius": 6 * mm});
            skCircle(sketch, "E2.24.39.0", {"center": v(80.68, -543.4) * mm, "radius": 6 * mm});
            skCircle(sketch, "E2.24.40.0", {"center": v(80.68, -563.4) * mm, "radius": 6 * mm});
            skCircle(sketch, "E2.24.41.0", {"center": v(80.68, -583.4) * mm, "radius": 6 * mm});
            skCircle(sketch, "E2.24.42.0", {"center": v(80.68, -603.4) * mm, "radius": 6 * mm});
            skCircle(sketch, "E2.24.43.0", {"center": v(80.68, -623.4) * mm, "radius": 6 * mm});
            skCircle(sketch, "E2.24.44.0", {"center": v(80.68, -643.4) * mm, "radius": 6 * mm});
            skCircle(sketch, "E2.24.45.0", {"center": v(80.68, -663.4) * mm, "radius": 6 * mm});
            skCircle(sketch, "E2.24.46.0", {"center": v(80.68, -683.4) * mm, "radius": 6 * mm});
            skCircle(sketch, "E2.24.47.0", {"center": v(80.68, -703.4) * mm, "radius": 6 * mm});
            skCircle(sketch, "E2.24.48.0", {"center": v(80.68, -723.4) * mm, "radius": 6 * mm});
            skCircle(sketch, "E2.24.49.0", {"center": v(80.68, -743.4) * mm, "radius": 6 * mm});
            skCircle(sketch, "E2.25.0.0", {"center": v(100.68, 236.6) * mm, "radius": 6 * mm});
            skCircle(sketch, "E2.25.1.0", {"center": v(100.68, 216.6) * mm, "radius": 6 * mm});
            skCircle(sketch, "E2.25.2.0", {"center": v(100.68, 196.6) * mm, "radius": 6 * mm});
            skCircle(sketch, "E2.25.3.0", {"center": v(100.68, 176.6) * mm, "radius": 6 * mm});
            skCircle(sketch, "E2.25.4.0", {"center": v(100.68, 156.6) * mm, "radius": 6 * mm});
            skCircle(sketch, "E2.25.5.0", {"center": v(100.68, 136.6) * mm, "radius": 6 * mm});
            skCircle(sketch, "E2.25.6.0", {"center": v(100.68, 116.6) * mm, "radius": 6 * mm});
            skCircle(sketch, "E2.25.7.0", {"center": v(100.68, 96.6) * mm, "radius": 6 * mm});
            skCircle(sketch, "E2.25.8.0", {"center": v(100.68, 76.6) * mm, "radius": 6 * mm});
            skCircle(sketch, "E2.25.9.0", {"center": v(100.68, 56.6) * mm, "radius": 6 * mm});
            skCircle(sketch, "E2.25.10.0", {"center": v(100.68, 36.6) * mm, "radius": 6 * mm});
            skCircle(sketch, "E2.25.11.0", {"center": v(100.68, 16.6) * mm, "radius": 6 * mm});
            skCircle(sketch, "E2.25.12.0", {"center": v(100.68, -3.4) * mm, "radius": 6 * mm});
            skCircle(sketch, "E2.25.13.0", {"center": v(100.68, -23.4) * mm, "radius": 6 * mm});
            skCircle(sketch, "E2.25.14.0", {"center": v(100.68, -43.4) * mm, "radius": 6 * mm});
            skCircle(sketch, "E2.25.15.0", {"center": v(100.68, -63.4) * mm, "radius": 6 * mm});
            skCircle(sketch, "E2.25.16.0", {"center": v(100.68, -83.4) * mm, "radius": 6 * mm});
            skCircle(sketch, "E2.25.17.0", {"center": v(100.68, -103.4) * mm, "radius": 6 * mm});
            skCircle(sketch, "E2.25.18.0", {"center": v(100.68, -123.4) * mm, "radius": 6 * mm});
            skCircle(sketch, "E2.25.19.0", {"center": v(100.68, -143.4) * mm, "radius": 6 * mm});
            skCircle(sketch, "E2.25.20.0", {"center": v(100.68, -163.4) * mm, "radius": 6 * mm});
            skCircle(sketch, "E2.25.21.0", {"center": v(100.68, -183.4) * mm, "radius": 6 * mm});
            skCircle(sketch, "E2.25.22.0", {"center": v(100.68, -203.4) * mm, "radius": 6 * mm});
            skCircle(sketch, "E2.25.23.0", {"center": v(100.68, -223.4) * mm, "radius": 6 * mm});
            skCircle(sketch, "E2.25.24.0", {"center": v(100.68, -243.4) * mm, "radius": 6 * mm});
            skCircle(sketch, "E2.25.25.0", {"center": v(100.68, -263.4) * mm, "radius": 6 * mm});
            skCircle(sketch, "E2.25.26.0", {"center": v(100.68, -283.4) * mm, "radius": 6 * mm});
            skCircle(sketch, "E2.25.27.0", {"center": v(100.68, -303.4) * mm, "radius": 6 * mm});
            skCircle(sketch, "E2.25.28.0", {"center": v(100.68, -323.4) * mm, "radius": 6 * mm});
            skCircle(sketch, "E2.25.29.0", {"center": v(100.68, -343.4) * mm, "radius": 6 * mm});
            skCircle(sketch, "E2.25.30.0", {"center": v(100.68, -363.4) * mm, "radius": 6 * mm});
            skCircle(sketch, "E2.25.31.0", {"center": v(100.68, -383.4) * mm, "radius": 6 * mm});
            skCircle(sketch, "E2.25.32.0", {"center": v(100.68, -403.4) * mm, "radius": 6 * mm});
            skCircle(sketch, "E2.25.33.0", {"center": v(100.68, -423.4) * mm, "radius": 6 * mm});
            skCircle(sketch, "E2.25.34.0", {"center": v(100.68, -443.4) * mm, "radius": 6 * mm});
            skCircle(sketch, "E2.25.35.0", {"center": v(100.68, -463.4) * mm, "radius": 6 * mm});
            skCircle(sketch, "E2.25.36.0", {"center": v(100.68, -483.4) * mm, "radius": 6 * mm});
            skCircle(sketch, "E2.25.37.0", {"center": v(100.68, -503.4) * mm, "radius": 6 * mm});
            skCircle(sketch, "E2.25.38.0", {"center": v(100.68, -523.4) * mm, "radius": 6 * mm});
            skCircle(sketch, "E2.25.39.0", {"center": v(100.68, -543.4) * mm, "radius": 6 * mm});
            skCircle(sketch, "E2.25.40.0", {"center": v(100.68, -563.4) * mm, "radius": 6 * mm});
            skCircle(sketch, "E2.25.41.0", {"center": v(100.68, -583.4) * mm, "radius": 6 * mm});
            skCircle(sketch, "E2.25.42.0", {"center": v(100.68, -603.4) * mm, "radius": 6 * mm});
            skCircle(sketch, "E2.25.43.0", {"center": v(100.68, -623.4) * mm, "radius": 6 * mm});
            skCircle(sketch, "E2.25.44.0", {"center": v(100.68, -643.4) * mm, "radius": 6 * mm});
            skCircle(sketch, "E2.25.45.0", {"center": v(100.68, -663.4) * mm, "radius": 6 * mm});
            skCircle(sketch, "E2.25.46.0", {"center": v(100.68, -683.4) * mm, "radius": 6 * mm});
            skCircle(sketch, "E2.25.47.0", {"center": v(100.68, -703.4) * mm, "radius": 6 * mm});
            skCircle(sketch, "E2.25.48.0", {"center": v(100.68, -723.4) * mm, "radius": 6 * mm});
            skCircle(sketch, "E2.25.49.0", {"center": v(100.68, -743.4) * mm, "radius": 6 * mm});
            skCircle(sketch, "E2.26.0.0", {"center": v(120.68, 236.6) * mm, "radius": 6 * mm});
            skCircle(sketch, "E2.26.1.0", {"center": v(120.68, 216.6) * mm, "radius": 6 * mm});
            skCircle(sketch, "E2.26.2.0", {"center": v(120.68, 196.6) * mm, "radius": 6 * mm});
            skCircle(sketch, "E2.26.3.0", {"center": v(120.68, 176.6) * mm, "radius": 6 * mm});
            skCircle(sketch, "E2.26.4.0", {"center": v(120.68, 156.6) * mm, "radius": 6 * mm});
            skCircle(sketch, "E2.26.5.0", {"center": v(120.68, 136.6) * mm, "radius": 6 * mm});
            skCircle(sketch, "E2.26.6.0", {"center": v(120.68, 116.6) * mm, "radius": 6 * mm});
            skCircle(sketch, "E2.26.7.0", {"center": v(120.68, 96.6) * mm, "radius": 6 * mm});
            skCircle(sketch, "E2.26.8.0", {"center": v(120.68, 76.6) * mm, "radius": 6 * mm});
            skCircle(sketch, "E2.26.9.0", {"center": v(120.68, 56.6) * mm, "radius": 6 * mm});
            skCircle(sketch, "E2.26.10.0", {"center": v(120.68, 36.6) * mm, "radius": 6 * mm});
            skCircle(sketch, "E2.26.11.0", {"center": v(120.68, 16.6) * mm, "radius": 6 * mm});
            skCircle(sketch, "E2.26.12.0", {"center": v(120.68, -3.4) * mm, "radius": 6 * mm});
            skCircle(sketch, "E2.26.13.0", {"center": v(120.68, -23.4) * mm, "radius": 6 * mm});
            skCircle(sketch, "E2.26.14.0", {"center": v(120.68, -43.4) * mm, "radius": 6 * mm});
            skCircle(sketch, "E2.26.15.0", {"center": v(120.68, -63.4) * mm, "radius": 6 * mm});
            skCircle(sketch, "E2.26.16.0", {"center": v(120.68, -83.4) * mm, "radius": 6 * mm});
            skCircle(sketch, "E2.26.17.0", {"center": v(120.68, -103.4) * mm, "radius": 6 * mm});
            skCircle(sketch, "E2.26.18.0", {"center": v(120.68, -123.4) * mm, "radius": 6 * mm});
            skCircle(sketch, "E2.26.19.0", {"center": v(120.68, -143.4) * mm, "radius": 6 * mm});
            skCircle(sketch, "E2.26.20.0", {"center": v(120.68, -163.4) * mm, "radius": 6 * mm});
            skCircle(sketch, "E2.26.21.0", {"center": v(120.68, -183.4) * mm, "radius": 6 * mm});
            skCircle(sketch, "E2.26.22.0", {"center": v(120.68, -203.4) * mm, "radius": 6 * mm});
            skCircle(sketch, "E2.26.23.0", {"center": v(120.68, -223.4) * mm, "radius": 6 * mm});
            skCircle(sketch, "E2.26.24.0", {"center": v(120.68, -243.4) * mm, "radius": 6 * mm});
            skCircle(sketch, "E2.26.25.0", {"center": v(120.68, -263.4) * mm, "radius": 6 * mm});
            skCircle(sketch, "E2.26.26.0", {"center": v(120.68, -283.4) * mm, "radius": 6 * mm});
            skCircle(sketch, "E2.26.27.0", {"center": v(120.68, -303.4) * mm, "radius": 6 * mm});
            skCircle(sketch, "E2.26.28.0", {"center": v(120.68, -323.4) * mm, "radius": 6 * mm});
            skCircle(sketch, "E2.26.29.0", {"center": v(120.68, -343.4) * mm, "radius": 6 * mm});
            skCircle(sketch, "E2.26.30.0", {"center": v(120.68, -363.4) * mm, "radius": 6 * mm});
            skCircle(sketch, "E2.26.31.0", {"center": v(120.68, -383.4) * mm, "radius": 6 * mm});
            skCircle(sketch, "E2.26.32.0", {"center": v(120.68, -403.4) * mm, "radius": 6 * mm});
            skCircle(sketch, "E2.26.33.0", {"center": v(120.68, -423.4) * mm, "radius": 6 * mm});
            skCircle(sketch, "E2.26.34.0", {"center": v(120.68, -443.4) * mm, "radius": 6 * mm});
            skCircle(sketch, "E2.26.35.0", {"center": v(120.68, -463.4) * mm, "radius": 6 * mm});
            skCircle(sketch, "E2.26.36.0", {"center": v(120.68, -483.4) * mm, "radius": 6 * mm});
            skCircle(sketch, "E2.26.37.0", {"center": v(120.68, -503.4) * mm, "radius": 6 * mm});
            skCircle(sketch, "E2.26.38.0", {"center": v(120.68, -523.4) * mm, "radius": 6 * mm});
            skCircle(sketch, "E2.26.39.0", {"center": v(120.68, -543.4) * mm, "radius": 6 * mm});
            skCircle(sketch, "E2.26.40.0", {"center": v(120.68, -563.4) * mm, "radius": 6 * mm});
            skCircle(sketch, "E2.26.41.0", {"center": v(120.68, -583.4) * mm, "radius": 6 * mm});
            skCircle(sketch, "E2.26.42.0", {"center": v(120.68, -603.4) * mm, "radius": 6 * mm});
            skCircle(sketch, "E2.26.43.0", {"center": v(120.68, -623.4) * mm, "radius": 6 * mm});
            skCircle(sketch, "E2.26.44.0", {"center": v(120.68, -643.4) * mm, "radius": 6 * mm});
            skCircle(sketch, "E2.26.45.0", {"center": v(120.68, -663.4) * mm, "radius": 6 * mm});
            skCircle(sketch, "E2.26.46.0", {"center": v(120.68, -683.4) * mm, "radius": 6 * mm});
            skCircle(sketch, "E2.26.47.0", {"center": v(120.68, -703.4) * mm, "radius": 6 * mm});
            skCircle(sketch, "E2.26.48.0", {"center": v(120.68, -723.4) * mm, "radius": 6 * mm});
            skCircle(sketch, "E2.26.49.0", {"center": v(120.68, -743.4) * mm, "radius": 6 * mm});
            skCircle(sketch, "E2.27.0.0", {"center": v(140.68, 236.6) * mm, "radius": 6 * mm});
            skCircle(sketch, "E2.27.1.0", {"center": v(140.68, 216.6) * mm, "radius": 6 * mm});
            skCircle(sketch, "E2.27.2.0", {"center": v(140.68, 196.6) * mm, "radius": 6 * mm});
            skCircle(sketch, "E2.27.3.0", {"center": v(140.68, 176.6) * mm, "radius": 6 * mm});
            skCircle(sketch, "E2.27.4.0", {"center": v(140.68, 156.6) * mm, "radius": 6 * mm});
            skCircle(sketch, "E2.27.5.0", {"center": v(140.68, 136.6) * mm, "radius": 6 * mm});
            skCircle(sketch, "E2.27.6.0", {"center": v(140.68, 116.6) * mm, "radius": 6 * mm});
            skCircle(sketch, "E2.27.7.0", {"center": v(140.68, 96.6) * mm, "radius": 6 * mm});
            skCircle(sketch, "E2.27.8.0", {"center": v(140.68, 76.6) * mm, "radius": 6 * mm});
            skCircle(sketch, "E2.27.9.0", {"center": v(140.68, 56.6) * mm, "radius": 6 * mm});
            skCircle(sketch, "E2.27.10.0", {"center": v(140.68, 36.6) * mm, "radius": 6 * mm});
            skCircle(sketch, "E2.27.11.0", {"center": v(140.68, 16.6) * mm, "radius": 6 * mm});
            skCircle(sketch, "E2.27.12.0", {"center": v(140.68, -3.4) * mm, "radius": 6 * mm});
            skCircle(sketch, "E2.27.13.0", {"center": v(140.68, -23.4) * mm, "radius": 6 * mm});
            skCircle(sketch, "E2.27.14.0", {"center": v(140.68, -43.4) * mm, "radius": 6 * mm});
            skCircle(sketch, "E2.27.15.0", {"center": v(140.68, -63.4) * mm, "radius": 6 * mm});
            skCircle(sketch, "E2.27.16.0", {"center": v(140.68, -83.4) * mm, "radius": 6 * mm});
            skCircle(sketch, "E2.27.17.0", {"center": v(140.68, -103.4) * mm, "radius": 6 * mm});
            skCircle(sketch, "E2.27.18.0", {"center": v(140.68, -123.4) * mm, "radius": 6 * mm});
            skCircle(sketch, "E2.27.19.0", {"center": v(140.68, -143.4) * mm, "radius": 6 * mm});
            skCircle(sketch, "E2.27.20.0", {"center": v(140.68, -163.4) * mm, "radius": 6 * mm});
            skCircle(sketch, "E2.27.21.0", {"center": v(140.68, -183.4) * mm, "radius": 6 * mm});
            skCircle(sketch, "E2.27.22.0", {"center": v(140.68, -203.4) * mm, "radius": 6 * mm});
            skCircle(sketch, "E2.27.23.0", {"center": v(140.68, -223.4) * mm, "radius": 6 * mm});
            skCircle(sketch, "E2.27.24.0", {"center": v(140.68, -243.4) * mm, "radius": 6 * mm});
            skCircle(sketch, "E2.27.25.0", {"center": v(140.68, -263.4) * mm, "radius": 6 * mm});
            skCircle(sketch, "E2.27.26.0", {"center": v(140.68, -283.4) * mm, "radius": 6 * mm});
            skCircle(sketch, "E2.27.27.0", {"center": v(140.68, -303.4) * mm, "radius": 6 * mm});
            skCircle(sketch, "E2.27.28.0", {"center": v(140.68, -323.4) * mm, "radius": 6 * mm});
            skCircle(sketch, "E2.27.29.0", {"center": v(140.68, -343.4) * mm, "radius": 6 * mm});
            skCircle(sketch, "E2.27.30.0", {"center": v(140.68, -363.4) * mm, "radius": 6 * mm});
            skCircle(sketch, "E2.27.31.0", {"center": v(140.68, -383.4) * mm, "radius": 6 * mm});
            skCircle(sketch, "E2.27.32.0", {"center": v(140.68, -403.4) * mm, "radius": 6 * mm});
            skCircle(sketch, "E2.27.33.0", {"center": v(140.68, -423.4) * mm, "radius": 6 * mm});
            skCircle(sketch, "E2.27.34.0", {"center": v(140.68, -443.4) * mm, "radius": 6 * mm});
            skCircle(sketch, "E2.27.35.0", {"center": v(140.68, -463.4) * mm, "radius": 6 * mm});
            skCircle(sketch, "E2.27.36.0", {"center": v(140.68, -483.4) * mm, "radius": 6 * mm});
            skCircle(sketch, "E2.27.37.0", {"center": v(140.68, -503.4) * mm, "radius": 6 * mm});
            skCircle(sketch, "E2.27.38.0", {"center": v(140.68, -523.4) * mm, "radius": 6 * mm});
            skCircle(sketch, "E2.27.39.0", {"center": v(140.68, -543.4) * mm, "radius": 6 * mm});
            skCircle(sketch, "E2.27.40.0", {"center": v(140.68, -563.4) * mm, "radius": 6 * mm});
            skCircle(sketch, "E2.27.41.0", {"center": v(140.68, -583.4) * mm, "radius": 6 * mm});
            skCircle(sketch, "E2.27.42.0", {"center": v(140.68, -603.4) * mm, "radius": 6 * mm});
            skCircle(sketch, "E2.27.43.0", {"center": v(140.68, -623.4) * mm, "radius": 6 * mm});
            skCircle(sketch, "E2.27.44.0", {"center": v(140.68, -643.4) * mm, "radius": 6 * mm});
            skCircle(sketch, "E2.27.45.0", {"center": v(140.68, -663.4) * mm, "radius": 6 * mm});
            skCircle(sketch, "E2.27.46.0", {"center": v(140.68, -683.4) * mm, "radius": 6 * mm});
            skCircle(sketch, "E2.27.47.0", {"center": v(140.68, -703.4) * mm, "radius": 6 * mm});
            skCircle(sketch, "E2.27.48.0", {"center": v(140.68, -723.4) * mm, "radius": 6 * mm});
            skCircle(sketch, "E2.27.49.0", {"center": v(140.68, -743.4) * mm, "radius": 6 * mm});
            skCircle(sketch, "E2.28.0.0", {"center": v(160.68, 236.6) * mm, "radius": 6 * mm});
            skCircle(sketch, "E2.28.1.0", {"center": v(160.68, 216.6) * mm, "radius": 6 * mm});
            skCircle(sketch, "E2.28.2.0", {"center": v(160.68, 196.6) * mm, "radius": 6 * mm});
            skCircle(sketch, "E2.28.3.0", {"center": v(160.68, 176.6) * mm, "radius": 6 * mm});
            skCircle(sketch, "E2.28.4.0", {"center": v(160.68, 156.6) * mm, "radius": 6 * mm});
            skCircle(sketch, "E2.28.5.0", {"center": v(160.68, 136.6) * mm, "radius": 6 * mm});
            skCircle(sketch, "E2.28.6.0", {"center": v(160.68, 116.6) * mm, "radius": 6 * mm});
            skCircle(sketch, "E2.28.7.0", {"center": v(160.68, 96.6) * mm, "radius": 6 * mm});
            skCircle(sketch, "E2.28.8.0", {"center": v(160.68, 76.6) * mm, "radius": 6 * mm});
            skCircle(sketch, "E2.28.9.0", {"center": v(160.68, 56.6) * mm, "radius": 6 * mm});
            skCircle(sketch, "E2.28.10.0", {"center": v(160.68, 36.6) * mm, "radius": 6 * mm});
            skCircle(sketch, "E2.28.11.0", {"center": v(160.68, 16.6) * mm, "radius": 6 * mm});
            skCircle(sketch, "E2.28.12.0", {"center": v(160.68, -3.4) * mm, "radius": 6 * mm});
            skCircle(sketch, "E2.28.13.0", {"center": v(160.68, -23.4) * mm, "radius": 6 * mm});
            skCircle(sketch, "E2.28.14.0", {"center": v(160.68, -43.4) * mm, "radius": 6 * mm});
            skCircle(sketch, "E2.28.15.0", {"center": v(160.68, -63.4) * mm, "radius": 6 * mm});
            skCircle(sketch, "E2.28.16.0", {"center": v(160.68, -83.4) * mm, "radius": 6 * mm});
            skCircle(sketch, "E2.28.17.0", {"center": v(160.68, -103.4) * mm, "radius": 6 * mm});
            skCircle(sketch, "E2.28.18.0", {"center": v(160.68, -123.4) * mm, "radius": 6 * mm});
            skCircle(sketch, "E2.28.19.0", {"center": v(160.68, -143.4) * mm, "radius": 6 * mm});
            skCircle(sketch, "E2.28.20.0", {"center": v(160.68, -163.4) * mm, "radius": 6 * mm});
            skCircle(sketch, "E2.28.21.0", {"center": v(160.68, -183.4) * mm, "radius": 6 * mm});
            skCircle(sketch, "E2.28.22.0", {"center": v(160.68, -203.4) * mm, "radius": 6 * mm});
            skCircle(sketch, "E2.28.23.0", {"center": v(160.68, -223.4) * mm, "radius": 6 * mm});
            skCircle(sketch, "E2.28.24.0", {"center": v(160.68, -243.4) * mm, "radius": 6 * mm});
            skCircle(sketch, "E2.28.25.0", {"center": v(160.68, -263.4) * mm, "radius": 6 * mm});
            skCircle(sketch, "E2.28.26.0", {"center": v(160.68, -283.4) * mm, "radius": 6 * mm});
            skCircle(sketch, "E2.28.27.0", {"center": v(160.68, -303.4) * mm, "radius": 6 * mm});
            skCircle(sketch, "E2.28.28.0", {"center": v(160.68, -323.4) * mm, "radius": 6 * mm});
            skCircle(sketch, "E2.28.29.0", {"center": v(160.68, -343.4) * mm, "radius": 6 * mm});
            skCircle(sketch, "E2.28.30.0", {"center": v(160.68, -363.4) * mm, "radius": 6 * mm});
            skCircle(sketch, "E2.28.31.0", {"center": v(160.68, -383.4) * mm, "radius": 6 * mm});
            skCircle(sketch, "E2.28.32.0", {"center": v(160.68, -403.4) * mm, "radius": 6 * mm});
            skCircle(sketch, "E2.28.33.0", {"center": v(160.68, -423.4) * mm, "radius": 6 * mm});
            skCircle(sketch, "E2.28.34.0", {"center": v(160.68, -443.4) * mm, "radius": 6 * mm});
            skCircle(sketch, "E2.28.35.0", {"center": v(160.68, -463.4) * mm, "radius": 6 * mm});
            skCircle(sketch, "E2.28.36.0", {"center": v(160.68, -483.4) * mm, "radius": 6 * mm});
            skCircle(sketch, "E2.28.37.0", {"center": v(160.68, -503.4) * mm, "radius": 6 * mm});
            skCircle(sketch, "E2.28.38.0", {"center": v(160.68, -523.4) * mm, "radius": 6 * mm});
            skCircle(sketch, "E2.28.39.0", {"center": v(160.68, -543.4) * mm, "radius": 6 * mm});
            skCircle(sketch, "E2.28.40.0", {"center": v(160.68, -563.4) * mm, "radius": 6 * mm});
            skCircle(sketch, "E2.28.41.0", {"center": v(160.68, -583.4) * mm, "radius": 6 * mm});
            skCircle(sketch, "E2.28.42.0", {"center": v(160.68, -603.4) * mm, "radius": 6 * mm});
            skCircle(sketch, "E2.28.43.0", {"center": v(160.68, -623.4) * mm, "radius": 6 * mm});
            skCircle(sketch, "E2.28.44.0", {"center": v(160.68, -643.4) * mm, "radius": 6 * mm});
            skCircle(sketch, "E2.28.45.0", {"center": v(160.68, -663.4) * mm, "radius": 6 * mm});
            skCircle(sketch, "E2.28.46.0", {"center": v(160.68, -683.4) * mm, "radius": 6 * mm});
            skCircle(sketch, "E2.28.47.0", {"center": v(160.68, -703.4) * mm, "radius": 6 * mm});
            skCircle(sketch, "E2.28.48.0", {"center": v(160.68, -723.4) * mm, "radius": 6 * mm});
            skCircle(sketch, "E2.28.49.0", {"center": v(160.68, -743.4) * mm, "radius": 6 * mm});
            skCircle(sketch, "E2.29.0.0", {"center": v(180.68, 236.6) * mm, "radius": 6 * mm});
            skCircle(sketch, "E2.29.1.0", {"center": v(180.68, 216.6) * mm, "radius": 6 * mm});
            skCircle(sketch, "E2.29.2.0", {"center": v(180.68, 196.6) * mm, "radius": 6 * mm});
            skCircle(sketch, "E2.29.3.0", {"center": v(180.68, 176.6) * mm, "radius": 6 * mm});
            skCircle(sketch, "E2.29.4.0", {"center": v(180.68, 156.6) * mm, "radius": 6 * mm});
            skCircle(sketch, "E2.29.5.0", {"center": v(180.68, 136.6) * mm, "radius": 6 * mm});
            skCircle(sketch, "E2.29.6.0", {"center": v(180.68, 116.6) * mm, "radius": 6 * mm});
            skCircle(sketch, "E2.29.7.0", {"center": v(180.68, 96.6) * mm, "radius": 6 * mm});
            skCircle(sketch, "E2.29.8.0", {"center": v(180.68, 76.6) * mm, "radius": 6 * mm});
            skCircle(sketch, "E2.29.9.0", {"center": v(180.68, 56.6) * mm, "radius": 6 * mm});
            skCircle(sketch, "E2.29.10.0", {"center": v(180.68, 36.6) * mm, "radius": 6 * mm});
            skCircle(sketch, "E2.29.11.0", {"center": v(180.68, 16.6) * mm, "radius": 6 * mm});
            skCircle(sketch, "E2.29.12.0", {"center": v(180.68, -3.4) * mm, "radius": 6 * mm});
            skCircle(sketch, "E2.29.13.0", {"center": v(180.68, -23.4) * mm, "radius": 6 * mm});
            skCircle(sketch, "E2.29.14.0", {"center": v(180.68, -43.4) * mm, "radius": 6 * mm});
            skCircle(sketch, "E2.29.15.0", {"center": v(180.68, -63.4) * mm, "radius": 6 * mm});
            skCircle(sketch, "E2.29.16.0", {"center": v(180.68, -83.4) * mm, "radius": 6 * mm});
            skCircle(sketch, "E2.29.17.0", {"center": v(180.68, -103.4) * mm, "radius": 6 * mm});
            skCircle(sketch, "E2.29.18.0", {"center": v(180.68, -123.4) * mm, "radius": 6 * mm});
            skCircle(sketch, "E2.29.19.0", {"center": v(180.68, -143.4) * mm, "radius": 6 * mm});
            skCircle(sketch, "E2.29.20.0", {"center": v(180.68, -163.4) * mm, "radius": 6 * mm});
            skCircle(sketch, "E2.29.21.0", {"center": v(180.68, -183.4) * mm, "radius": 6 * mm});
            skCircle(sketch, "E2.29.22.0", {"center": v(180.68, -203.4) * mm, "radius": 6 * mm});
            skCircle(sketch, "E2.29.23.0", {"center": v(180.68, -223.4) * mm, "radius": 6 * mm});
            skCircle(sketch, "E2.29.24.0", {"center": v(180.68, -243.4) * mm, "radius": 6 * mm});
            skCircle(sketch, "E2.29.25.0", {"center": v(180.68, -263.4) * mm, "radius": 6 * mm});
            skCircle(sketch, "E2.29.26.0", {"center": v(180.68, -283.4) * mm, "radius": 6 * mm});
            skCircle(sketch, "E2.29.27.0", {"center": v(180.68, -303.4) * mm, "radius": 6 * mm});
            skCircle(sketch, "E2.29.28.0", {"center": v(180.68, -323.4) * mm, "radius": 6 * mm});
            skCircle(sketch, "E2.29.29.0", {"center": v(180.68, -343.4) * mm, "radius": 6 * mm});
            skCircle(sketch, "E2.29.30.0", {"center": v(180.68, -363.4) * mm, "radius": 6 * mm});
            skCircle(sketch, "E2.29.31.0", {"center": v(180.68, -383.4) * mm, "radius": 6 * mm});
            skCircle(sketch, "E2.29.32.0", {"center": v(180.68, -403.4) * mm, "radius": 6 * mm});
            skCircle(sketch, "E2.29.33.0", {"center": v(180.68, -423.4) * mm, "radius": 6 * mm});
            skCircle(sketch, "E2.29.34.0", {"center": v(180.68, -443.4) * mm, "radius": 6 * mm});
            skCircle(sketch, "E2.29.35.0", {"center": v(180.68, -463.4) * mm, "radius": 6 * mm});
            skCircle(sketch, "E2.29.36.0", {"center": v(180.68, -483.4) * mm, "radius": 6 * mm});
            skCircle(sketch, "E2.29.37.0", {"center": v(180.68, -503.4) * mm, "radius": 6 * mm});
            skCircle(sketch, "E2.29.38.0", {"center": v(180.68, -523.4) * mm, "radius": 6 * mm});
            skCircle(sketch, "E2.29.39.0", {"center": v(180.68, -543.4) * mm, "radius": 6 * mm});
            skCircle(sketch, "E2.29.40.0", {"center": v(180.68, -563.4) * mm, "radius": 6 * mm});
            skCircle(sketch, "E2.29.41.0", {"center": v(180.68, -583.4) * mm, "radius": 6 * mm});
            skCircle(sketch, "E2.29.42.0", {"center": v(180.68, -603.4) * mm, "radius": 6 * mm});
            skCircle(sketch, "E2.29.43.0", {"center": v(180.68, -623.4) * mm, "radius": 6 * mm});
            skCircle(sketch, "E2.29.44.0", {"center": v(180.68, -643.4) * mm, "radius": 6 * mm});
            skCircle(sketch, "E2.29.45.0", {"center": v(180.68, -663.4) * mm, "radius": 6 * mm});
            skCircle(sketch, "E2.29.46.0", {"center": v(180.68, -683.4) * mm, "radius": 6 * mm});
            skCircle(sketch, "E2.29.47.0", {"center": v(180.68, -703.4) * mm, "radius": 6 * mm});
            skCircle(sketch, "E2.29.48.0", {"center": v(180.68, -723.4) * mm, "radius": 6 * mm});
            skCircle(sketch, "E2.29.49.0", {"center": v(180.68, -743.4) * mm, "radius": 6 * mm});
            skCircle(sketch, "E2.30.0.0", {"center": v(200.68, 236.6) * mm, "radius": 6 * mm});
            skCircle(sketch, "E2.30.1.0", {"center": v(200.68, 216.6) * mm, "radius": 6 * mm});
            skCircle(sketch, "E2.30.2.0", {"center": v(200.68, 196.6) * mm, "radius": 6 * mm});
            skCircle(sketch, "E2.30.3.0", {"center": v(200.68, 176.6) * mm, "radius": 6 * mm});
            skCircle(sketch, "E2.30.4.0", {"center": v(200.68, 156.6) * mm, "radius": 6 * mm});
            skCircle(sketch, "E2.30.5.0", {"center": v(200.68, 136.6) * mm, "radius": 6 * mm});
            skCircle(sketch, "E2.30.6.0", {"center": v(200.68, 116.6) * mm, "radius": 6 * mm});
            skCircle(sketch, "E2.30.7.0", {"center": v(200.68, 96.6) * mm, "radius": 6 * mm});
            skCircle(sketch, "E2.30.8.0", {"center": v(200.68, 76.6) * mm, "radius": 6 * mm});
            skCircle(sketch, "E2.30.9.0", {"center": v(200.68, 56.6) * mm, "radius": 6 * mm});
            skCircle(sketch, "E2.30.10.0", {"center": v(200.68, 36.6) * mm, "radius": 6 * mm});
            skCircle(sketch, "E2.30.11.0", {"center": v(200.68, 16.6) * mm, "radius": 6 * mm});
            skCircle(sketch, "E2.30.12.0", {"center": v(200.68, -3.4) * mm, "radius": 6 * mm});
            skCircle(sketch, "E2.30.13.0", {"center": v(200.68, -23.4) * mm, "radius": 6 * mm});
            skCircle(sketch, "E2.30.14.0", {"center": v(200.68, -43.4) * mm, "radius": 6 * mm});
            skCircle(sketch, "E2.30.15.0", {"center": v(200.68, -63.4) * mm, "radius": 6 * mm});
            skCircle(sketch, "E2.30.16.0", {"center": v(200.68, -83.4) * mm, "radius": 6 * mm});
            skCircle(sketch, "E2.30.17.0", {"center": v(200.68, -103.4) * mm, "radius": 6 * mm});
            skCircle(sketch, "E2.30.18.0", {"center": v(200.68, -123.4) * mm, "radius": 6 * mm});
            skCircle(sketch, "E2.30.19.0", {"center": v(200.68, -143.4) * mm, "radius": 6 * mm});
            skCircle(sketch, "E2.30.20.0", {"center": v(200.68, -163.4) * mm, "radius": 6 * mm});
            skCircle(sketch, "E2.30.21.0", {"center": v(200.68, -183.4) * mm, "radius": 6 * mm});
            skCircle(sketch, "E2.30.22.0", {"center": v(200.68, -203.4) * mm, "radius": 6 * mm});
            skCircle(sketch, "E2.30.23.0", {"center": v(200.68, -223.4) * mm, "radius": 6 * mm});
            skCircle(sketch, "E2.30.24.0", {"center": v(200.68, -243.4) * mm, "radius": 6 * mm});
            skCircle(sketch, "E2.30.25.0", {"center": v(200.68, -263.4) * mm, "radius": 6 * mm});
            skCircle(sketch, "E2.30.26.0", {"center": v(200.68, -283.4) * mm, "radius": 6 * mm});
            skCircle(sketch, "E2.30.27.0", {"center": v(200.68, -303.4) * mm, "radius": 6 * mm});
            skCircle(sketch, "E2.30.28.0", {"center": v(200.68, -323.4) * mm, "radius": 6 * mm});
            skCircle(sketch, "E2.30.29.0", {"center": v(200.68, -343.4) * mm, "radius": 6 * mm});
            skCircle(sketch, "E2.30.30.0", {"center": v(200.68, -363.4) * mm, "radius": 6 * mm});
            skCircle(sketch, "E2.30.31.0", {"center": v(200.68, -383.4) * mm, "radius": 6 * mm});
            skCircle(sketch, "E2.30.32.0", {"center": v(200.68, -403.4) * mm, "radius": 6 * mm});
            skCircle(sketch, "E2.30.33.0", {"center": v(200.68, -423.4) * mm, "radius": 6 * mm});
            skCircle(sketch, "E2.30.34.0", {"center": v(200.68, -443.4) * mm, "radius": 6 * mm});
            skCircle(sketch, "E2.30.35.0", {"center": v(200.68, -463.4) * mm, "radius": 6 * mm});
            skCircle(sketch, "E2.30.36.0", {"center": v(200.68, -483.4) * mm, "radius": 6 * mm});
            skCircle(sketch, "E2.30.37.0", {"center": v(200.68, -503.4) * mm, "radius": 6 * mm});
            skCircle(sketch, "E2.30.38.0", {"center": v(200.68, -523.4) * mm, "radius": 6 * mm});
            skCircle(sketch, "E2.30.39.0", {"center": v(200.68, -543.4) * mm, "radius": 6 * mm});
            skCircle(sketch, "E2.30.40.0", {"center": v(200.68, -563.4) * mm, "radius": 6 * mm});
            skCircle(sketch, "E2.30.41.0", {"center": v(200.68, -583.4) * mm, "radius": 6 * mm});
            skCircle(sketch, "E2.30.42.0", {"center": v(200.68, -603.4) * mm, "radius": 6 * mm});
            skCircle(sketch, "E2.30.43.0", {"center": v(200.68, -623.4) * mm, "radius": 6 * mm});
            skCircle(sketch, "E2.30.44.0", {"center": v(200.68, -643.4) * mm, "radius": 6 * mm});
            skCircle(sketch, "E2.30.45.0", {"center": v(200.68, -663.4) * mm, "radius": 6 * mm});
            skCircle(sketch, "E2.30.46.0", {"center": v(200.68, -683.4) * mm, "radius": 6 * mm});
            skCircle(sketch, "E2.30.47.0", {"center": v(200.68, -703.4) * mm, "radius": 6 * mm});
            skCircle(sketch, "E2.30.48.0", {"center": v(200.68, -723.4) * mm, "radius": 6 * mm});
            skCircle(sketch, "E2.30.49.0", {"center": v(200.68, -743.4) * mm, "radius": 6 * mm});
            skCircle(sketch, "E2.31.0.0", {"center": v(220.68, 236.6) * mm, "radius": 6 * mm});
            skCircle(sketch, "E2.31.1.0", {"center": v(220.68, 216.6) * mm, "radius": 6 * mm});
            skCircle(sketch, "E2.31.2.0", {"center": v(220.68, 196.6) * mm, "radius": 6 * mm});
            skCircle(sketch, "E2.31.3.0", {"center": v(220.68, 176.6) * mm, "radius": 6 * mm});
            skCircle(sketch, "E2.31.4.0", {"center": v(220.68, 156.6) * mm, "radius": 6 * mm});
            skCircle(sketch, "E2.31.5.0", {"center": v(220.68, 136.6) * mm, "radius": 6 * mm});
            skCircle(sketch, "E2.31.6.0", {"center": v(220.68, 116.6) * mm, "radius": 6 * mm});
            skCircle(sketch, "E2.31.7.0", {"center": v(220.68, 96.6) * mm, "radius": 6 * mm});
            skCircle(sketch, "E2.31.8.0", {"center": v(220.68, 76.6) * mm, "radius": 6 * mm});
            skCircle(sketch, "E2.31.9.0", {"center": v(220.68, 56.6) * mm, "radius": 6 * mm});
            skCircle(sketch, "E2.31.10.0", {"center": v(220.68, 36.6) * mm, "radius": 6 * mm});
            skCircle(sketch, "E2.31.11.0", {"center": v(220.68, 16.6) * mm, "radius": 6 * mm});
            skCircle(sketch, "E2.31.12.0", {"center": v(220.68, -3.4) * mm, "radius": 6 * mm});
            skCircle(sketch, "E2.31.13.0", {"center": v(220.68, -23.4) * mm, "radius": 6 * mm});
            skCircle(sketch, "E2.31.14.0", {"center": v(220.68, -43.4) * mm, "radius": 6 * mm});
            skCircle(sketch, "E2.31.15.0", {"center": v(220.68, -63.4) * mm, "radius": 6 * mm});
            skCircle(sketch, "E2.31.16.0", {"center": v(220.68, -83.4) * mm, "radius": 6 * mm});
            skCircle(sketch, "E2.31.17.0", {"center": v(220.68, -103.4) * mm, "radius": 6 * mm});
            skCircle(sketch, "E2.31.18.0", {"center": v(220.68, -123.4) * mm, "radius": 6 * mm});
            skCircle(sketch, "E2.31.19.0", {"center": v(220.68, -143.4) * mm, "radius": 6 * mm});
            skCircle(sketch, "E2.31.20.0", {"center": v(220.68, -163.4) * mm, "radius": 6 * mm});
            skCircle(sketch, "E2.31.21.0", {"center": v(220.68, -183.4) * mm, "radius": 6 * mm});
            skCircle(sketch, "E2.31.22.0", {"center": v(220.68, -203.4) * mm, "radius": 6 * mm});
            skCircle(sketch, "E2.31.23.0", {"center": v(220.68, -223.4) * mm, "radius": 6 * mm});
            skCircle(sketch, "E2.31.24.0", {"center": v(220.68, -243.4) * mm, "radius": 6 * mm});
            skCircle(sketch, "E2.31.25.0", {"center": v(220.68, -263.4) * mm, "radius": 6 * mm});
            skCircle(sketch, "E2.31.26.0", {"center": v(220.68, -283.4) * mm, "radius": 6 * mm});
            skCircle(sketch, "E2.31.27.0", {"center": v(220.68, -303.4) * mm, "radius": 6 * mm});
            skCircle(sketch, "E2.31.28.0", {"center": v(220.68, -323.4) * mm, "radius": 6 * mm});
            skCircle(sketch, "E2.31.29.0", {"center": v(220.68, -343.4) * mm, "radius": 6 * mm});
            skCircle(sketch, "E2.31.30.0", {"center": v(220.68, -363.4) * mm, "radius": 6 * mm});
            skCircle(sketch, "E2.31.31.0", {"center": v(220.68, -383.4) * mm, "radius": 6 * mm});
            skCircle(sketch, "E2.31.32.0", {"center": v(220.68, -403.4) * mm, "radius": 6 * mm});
            skCircle(sketch, "E2.31.33.0", {"center": v(220.68, -423.4) * mm, "radius": 6 * mm});
            skCircle(sketch, "E2.31.34.0", {"center": v(220.68, -443.4) * mm, "radius": 6 * mm});
            skCircle(sketch, "E2.31.35.0", {"center": v(220.68, -463.4) * mm, "radius": 6 * mm});
            skCircle(sketch, "E2.31.36.0", {"center": v(220.68, -483.4) * mm, "radius": 6 * mm});
            skCircle(sketch, "E2.31.37.0", {"center": v(220.68, -503.4) * mm, "radius": 6 * mm});
            skCircle(sketch, "E2.31.38.0", {"center": v(220.68, -523.4) * mm, "radius": 6 * mm});
            skCircle(sketch, "E2.31.39.0", {"center": v(220.68, -543.4) * mm, "radius": 6 * mm});
            skCircle(sketch, "E2.31.40.0", {"center": v(220.68, -563.4) * mm, "radius": 6 * mm});
            skCircle(sketch, "E2.31.41.0", {"center": v(220.68, -583.4) * mm, "radius": 6 * mm});
            skCircle(sketch, "E2.31.42.0", {"center": v(220.68, -603.4) * mm, "radius": 6 * mm});
            skCircle(sketch, "E2.31.43.0", {"center": v(220.68, -623.4) * mm, "radius": 6 * mm});
            skCircle(sketch, "E2.31.44.0", {"center": v(220.68, -643.4) * mm, "radius": 6 * mm});
            skCircle(sketch, "E2.31.45.0", {"center": v(220.68, -663.4) * mm, "radius": 6 * mm});
            skCircle(sketch, "E2.31.46.0", {"center": v(220.68, -683.4) * mm, "radius": 6 * mm});
            skCircle(sketch, "E2.31.47.0", {"center": v(220.68, -703.4) * mm, "radius": 6 * mm});
            skCircle(sketch, "E2.31.48.0", {"center": v(220.68, -723.4) * mm, "radius": 6 * mm});
            skCircle(sketch, "E2.31.49.0", {"center": v(220.68, -743.4) * mm, "radius": 6 * mm});
            skCircle(sketch, "E2.32.0.0", {"center": v(240.68, 236.6) * mm, "radius": 6 * mm});
            skCircle(sketch, "E2.32.1.0", {"center": v(240.68, 216.6) * mm, "radius": 6 * mm});
            skCircle(sketch, "E2.32.2.0", {"center": v(240.68, 196.6) * mm, "radius": 6 * mm});
            skCircle(sketch, "E2.32.3.0", {"center": v(240.68, 176.6) * mm, "radius": 6 * mm});
            skCircle(sketch, "E2.32.4.0", {"center": v(240.68, 156.6) * mm, "radius": 6 * mm});
            skCircle(sketch, "E2.32.5.0", {"center": v(240.68, 136.6) * mm, "radius": 6 * mm});
            skCircle(sketch, "E2.32.6.0", {"center": v(240.68, 116.6) * mm, "radius": 6 * mm});
            skCircle(sketch, "E2.32.7.0", {"center": v(240.68, 96.6) * mm, "radius": 6 * mm});
            skCircle(sketch, "E2.32.8.0", {"center": v(240.68, 76.6) * mm, "radius": 6 * mm});
            skCircle(sketch, "E2.32.9.0", {"center": v(240.68, 56.6) * mm, "radius": 6 * mm});
            skCircle(sketch, "E2.32.10.0", {"center": v(240.68, 36.6) * mm, "radius": 6 * mm});
            skCircle(sketch, "E2.32.11.0", {"center": v(240.68, 16.6) * mm, "radius": 6 * mm});
            skCircle(sketch, "E2.32.12.0", {"center": v(240.68, -3.4) * mm, "radius": 6 * mm});
            skCircle(sketch, "E2.32.13.0", {"center": v(240.68, -23.4) * mm, "radius": 6 * mm});
            skCircle(sketch, "E2.32.14.0", {"center": v(240.68, -43.4) * mm, "radius": 6 * mm});
            skCircle(sketch, "E2.32.15.0", {"center": v(240.68, -63.4) * mm, "radius": 6 * mm});
            skCircle(sketch, "E2.32.16.0", {"center": v(240.68, -83.4) * mm, "radius": 6 * mm});
            skCircle(sketch, "E2.32.17.0", {"center": v(240.68, -103.4) * mm, "radius": 6 * mm});
            skCircle(sketch, "E2.32.18.0", {"center": v(240.68, -123.4) * mm, "radius": 6 * mm});
            skCircle(sketch, "E2.32.19.0", {"center": v(240.68, -143.4) * mm, "radius": 6 * mm});
            skCircle(sketch, "E2.32.20.0", {"center": v(240.68, -163.4) * mm, "radius": 6 * mm});
            skCircle(sketch, "E2.32.21.0", {"center": v(240.68, -183.4) * mm, "radius": 6 * mm});
            skCircle(sketch, "E2.32.22.0", {"center": v(240.68, -203.4) * mm, "radius": 6 * mm});
            skCircle(sketch, "E2.32.23.0", {"center": v(240.68, -223.4) * mm, "radius": 6 * mm});
            skCircle(sketch, "E2.32.24.0", {"center": v(240.68, -243.4) * mm, "radius": 6 * mm});
            skCircle(sketch, "E2.32.25.0", {"center": v(240.68, -263.4) * mm, "radius": 6 * mm});
            skCircle(sketch, "E2.32.26.0", {"center": v(240.68, -283.4) * mm, "radius": 6 * mm});
            skCircle(sketch, "E2.32.27.0", {"center": v(240.68, -303.4) * mm, "radius": 6 * mm});
            skCircle(sketch, "E2.32.28.0", {"center": v(240.68, -323.4) * mm, "radius": 6 * mm});
            skCircle(sketch, "E2.32.29.0", {"center": v(240.68, -343.4) * mm, "radius": 6 * mm});
            skCircle(sketch, "E2.32.30.0", {"center": v(240.68, -363.4) * mm, "radius": 6 * mm});
            skCircle(sketch, "E2.32.31.0", {"center": v(240.68, -383.4) * mm, "radius": 6 * mm});
            skCircle(sketch, "E2.32.32.0", {"center": v(240.68, -403.4) * mm, "radius": 6 * mm});
            skCircle(sketch, "E2.32.33.0", {"center": v(240.68, -423.4) * mm, "radius": 6 * mm});
            skCircle(sketch, "E2.32.34.0", {"center": v(240.68, -443.4) * mm, "radius": 6 * mm});
            skCircle(sketch, "E2.32.35.0", {"center": v(240.68, -463.4) * mm, "radius": 6 * mm});
            skCircle(sketch, "E2.32.36.0", {"center": v(240.68, -483.4) * mm, "radius": 6 * mm});
            skCircle(sketch, "E2.32.37.0", {"center": v(240.68, -503.4) * mm, "radius": 6 * mm});
            skCircle(sketch, "E2.32.38.0", {"center": v(240.68, -523.4) * mm, "radius": 6 * mm});
            skCircle(sketch, "E2.32.39.0", {"center": v(240.68, -543.4) * mm, "radius": 6 * mm});
            skCircle(sketch, "E2.32.40.0", {"center": v(240.68, -563.4) * mm, "radius": 6 * mm});
            skCircle(sketch, "E2.32.41.0", {"center": v(240.68, -583.4) * mm, "radius": 6 * mm});
            skCircle(sketch, "E2.32.42.0", {"center": v(240.68, -603.4) * mm, "radius": 6 * mm});
            skCircle(sketch, "E2.32.43.0", {"center": v(240.68, -623.4) * mm, "radius": 6 * mm});
            skCircle(sketch, "E2.32.44.0", {"center": v(240.68, -643.4) * mm, "radius": 6 * mm});
            skCircle(sketch, "E2.32.45.0", {"center": v(240.68, -663.4) * mm, "radius": 6 * mm});
            skCircle(sketch, "E2.32.46.0", {"center": v(240.68, -683.4) * mm, "radius": 6 * mm});
            skCircle(sketch, "E2.32.47.0", {"center": v(240.68, -703.4) * mm, "radius": 6 * mm});
            skCircle(sketch, "E2.32.48.0", {"center": v(240.68, -723.4) * mm, "radius": 6 * mm});
            skCircle(sketch, "E2.32.49.0", {"center": v(240.68, -743.4) * mm, "radius": 6 * mm});
            skCircle(sketch, "E2.33.0.0", {"center": v(260.68, 236.6) * mm, "radius": 6 * mm});
            skCircle(sketch, "E2.33.1.0", {"center": v(260.68, 216.6) * mm, "radius": 6 * mm});
            skCircle(sketch, "E2.33.2.0", {"center": v(260.68, 196.6) * mm, "radius": 6 * mm});
            skCircle(sketch, "E2.33.3.0", {"center": v(260.68, 176.6) * mm, "radius": 6 * mm});
            skCircle(sketch, "E2.33.4.0", {"center": v(260.68, 156.6) * mm, "radius": 6 * mm});
            skCircle(sketch, "E2.33.5.0", {"center": v(260.68, 136.6) * mm, "radius": 6 * mm});
            skCircle(sketch, "E2.33.6.0", {"center": v(260.68, 116.6) * mm, "radius": 6 * mm});
            skCircle(sketch, "E2.33.7.0", {"center": v(260.68, 96.6) * mm, "radius": 6 * mm});
            skCircle(sketch, "E2.33.8.0", {"center": v(260.68, 76.6) * mm, "radius": 6 * mm});
            skCircle(sketch, "E2.33.9.0", {"center": v(260.68, 56.6) * mm, "radius": 6 * mm});
            skCircle(sketch, "E2.33.10.0", {"center": v(260.68, 36.6) * mm, "radius": 6 * mm});
            skCircle(sketch, "E2.33.11.0", {"center": v(260.68, 16.6) * mm, "radius": 6 * mm});
            skCircle(sketch, "E2.33.12.0", {"center": v(260.68, -3.4) * mm, "radius": 6 * mm});
            skCircle(sketch, "E2.33.13.0", {"center": v(260.68, -23.4) * mm, "radius": 6 * mm});
            skCircle(sketch, "E2.33.14.0", {"center": v(260.68, -43.4) * mm, "radius": 6 * mm});
            skCircle(sketch, "E2.33.15.0", {"center": v(260.68, -63.4) * mm, "radius": 6 * mm});
            skCircle(sketch, "E2.33.16.0", {"center": v(260.68, -83.4) * mm, "radius": 6 * mm});
            skCircle(sketch, "E2.33.17.0", {"center": v(260.68, -103.4) * mm, "radius": 6 * mm});
            skCircle(sketch, "E2.33.18.0", {"center": v(260.68, -123.4) * mm, "radius": 6 * mm});
            skCircle(sketch, "E2.33.19.0", {"center": v(260.68, -143.4) * mm, "radius": 6 * mm});
            skCircle(sketch, "E2.33.20.0", {"center": v(260.68, -163.4) * mm, "radius": 6 * mm});
            skCircle(sketch, "E2.33.21.0", {"center": v(260.68, -183.4) * mm, "radius": 6 * mm});
            skCircle(sketch, "E2.33.22.0", {"center": v(260.68, -203.4) * mm, "radius": 6 * mm});
            skCircle(sketch, "E2.33.23.0", {"center": v(260.68, -223.4) * mm, "radius": 6 * mm});
            skCircle(sketch, "E2.33.24.0", {"center": v(260.68, -243.4) * mm, "radius": 6 * mm});
            skCircle(sketch, "E2.33.25.0", {"center": v(260.68, -263.4) * mm, "radius": 6 * mm});
            skCircle(sketch, "E2.33.26.0", {"center": v(260.68, -283.4) * mm, "radius": 6 * mm});
            skCircle(sketch, "E2.33.27.0", {"center": v(260.68, -303.4) * mm, "radius": 6 * mm});
            skCircle(sketch, "E2.33.28.0", {"center": v(260.68, -323.4) * mm, "radius": 6 * mm});
            skCircle(sketch, "E2.33.29.0", {"center": v(260.68, -343.4) * mm, "radius": 6 * mm});
            skCircle(sketch, "E2.33.30.0", {"center": v(260.68, -363.4) * mm, "radius": 6 * mm});
            skCircle(sketch, "E2.33.31.0", {"center": v(260.68, -383.4) * mm, "radius": 6 * mm});
            skCircle(sketch, "E2.33.32.0", {"center": v(260.68, -403.4) * mm, "radius": 6 * mm});
            skCircle(sketch, "E2.33.33.0", {"center": v(260.68, -423.4) * mm, "radius": 6 * mm});
            skCircle(sketch, "E2.33.34.0", {"center": v(260.68, -443.4) * mm, "radius": 6 * mm});
            skCircle(sketch, "E2.33.35.0", {"center": v(260.68, -463.4) * mm, "radius": 6 * mm});
            skCircle(sketch, "E2.33.36.0", {"center": v(260.68, -483.4) * mm, "radius": 6 * mm});
            skCircle(sketch, "E2.33.37.0", {"center": v(260.68, -503.4) * mm, "radius": 6 * mm});
            skCircle(sketch, "E2.33.38.0", {"center": v(260.68, -523.4) * mm, "radius": 6 * mm});
            skCircle(sketch, "E2.33.39.0", {"center": v(260.68, -543.4) * mm, "radius": 6 * mm});
            skCircle(sketch, "E2.33.40.0", {"center": v(260.68, -563.4) * mm, "radius": 6 * mm});
            skCircle(sketch, "E2.33.41.0", {"center": v(260.68, -583.4) * mm, "radius": 6 * mm});
            skCircle(sketch, "E2.33.42.0", {"center": v(260.68, -603.4) * mm, "radius": 6 * mm});
            skCircle(sketch, "E2.33.43.0", {"center": v(260.68, -623.4) * mm, "radius": 6 * mm});
            skCircle(sketch, "E2.33.44.0", {"center": v(260.68, -643.4) * mm, "radius": 6 * mm});
            skCircle(sketch, "E2.33.45.0", {"center": v(260.68, -663.4) * mm, "radius": 6 * mm});
            skCircle(sketch, "E2.33.46.0", {"center": v(260.68, -683.4) * mm, "radius": 6 * mm});
            skCircle(sketch, "E2.33.47.0", {"center": v(260.68, -703.4) * mm, "radius": 6 * mm});
            skCircle(sketch, "E2.33.48.0", {"center": v(260.68, -723.4) * mm, "radius": 6 * mm});
            skCircle(sketch, "E2.33.49.0", {"center": v(260.68, -743.4) * mm, "radius": 6 * mm});
            skCircle(sketch, "E2.34.0.0", {"center": v(280.68, 236.6) * mm, "radius": 6 * mm});
            skCircle(sketch, "E2.34.1.0", {"center": v(280.68, 216.6) * mm, "radius": 6 * mm});
            skCircle(sketch, "E2.34.2.0", {"center": v(280.68, 196.6) * mm, "radius": 6 * mm});
            skCircle(sketch, "E2.34.3.0", {"center": v(280.68, 176.6) * mm, "radius": 6 * mm});
            skCircle(sketch, "E2.34.4.0", {"center": v(280.68, 156.6) * mm, "radius": 6 * mm});
            skCircle(sketch, "E2.34.5.0", {"center": v(280.68, 136.6) * mm, "radius": 6 * mm});
            skCircle(sketch, "E2.34.6.0", {"center": v(280.68, 116.6) * mm, "radius": 6 * mm});
            skCircle(sketch, "E2.34.7.0", {"center": v(280.68, 96.6) * mm, "radius": 6 * mm});
            skCircle(sketch, "E2.34.8.0", {"center": v(280.68, 76.6) * mm, "radius": 6 * mm});
            skCircle(sketch, "E2.34.9.0", {"center": v(280.68, 56.6) * mm, "radius": 6 * mm});
            skCircle(sketch, "E2.34.10.0", {"center": v(280.68, 36.6) * mm, "radius": 6 * mm});
            skCircle(sketch, "E2.34.11.0", {"center": v(280.68, 16.6) * mm, "radius": 6 * mm});
            skCircle(sketch, "E2.34.12.0", {"center": v(280.68, -3.4) * mm, "radius": 6 * mm});
            skCircle(sketch, "E2.34.13.0", {"center": v(280.68, -23.4) * mm, "radius": 6 * mm});
            skCircle(sketch, "E2.34.14.0", {"center": v(280.68, -43.4) * mm, "radius": 6 * mm});
            skCircle(sketch, "E2.34.15.0", {"center": v(280.68, -63.4) * mm, "radius": 6 * mm});
            skCircle(sketch, "E2.34.16.0", {"center": v(280.68, -83.4) * mm, "radius": 6 * mm});
            skCircle(sketch, "E2.34.17.0", {"center": v(280.68, -103.4) * mm, "radius": 6 * mm});
            skCircle(sketch, "E2.34.18.0", {"center": v(280.68, -123.4) * mm, "radius": 6 * mm});
            skCircle(sketch, "E2.34.19.0", {"center": v(280.68, -143.4) * mm, "radius": 6 * mm});
            skCircle(sketch, "E2.34.20.0", {"center": v(280.68, -163.4) * mm, "radius": 6 * mm});
            skCircle(sketch, "E2.34.21.0", {"center": v(280.68, -183.4) * mm, "radius": 6 * mm});
            skCircle(sketch, "E2.34.22.0", {"center": v(280.68, -203.4) * mm, "radius": 6 * mm});
            skCircle(sketch, "E2.34.23.0", {"center": v(280.68, -223.4) * mm, "radius": 6 * mm});
            skCircle(sketch, "E2.34.24.0", {"center": v(280.68, -243.4) * mm, "radius": 6 * mm});
            skCircle(sketch, "E2.34.25.0", {"center": v(280.68, -263.4) * mm, "radius": 6 * mm});
            skCircle(sketch, "E2.34.26.0", {"center": v(280.68, -283.4) * mm, "radius": 6 * mm});
            skCircle(sketch, "E2.34.27.0", {"center": v(280.68, -303.4) * mm, "radius": 6 * mm});
            skCircle(sketch, "E2.34.28.0", {"center": v(280.68, -323.4) * mm, "radius": 6 * mm});
            skCircle(sketch, "E2.34.29.0", {"center": v(280.68, -343.4) * mm, "radius": 6 * mm});
            skCircle(sketch, "E2.34.30.0", {"center": v(280.68, -363.4) * mm, "radius": 6 * mm});
            skCircle(sketch, "E2.34.31.0", {"center": v(280.68, -383.4) * mm, "radius": 6 * mm});
            skCircle(sketch, "E2.34.32.0", {"center": v(280.68, -403.4) * mm, "radius": 6 * mm});
            skCircle(sketch, "E2.34.33.0", {"center": v(280.68, -423.4) * mm, "radius": 6 * mm});
            skCircle(sketch, "E2.34.34.0", {"center": v(280.68, -443.4) * mm, "radius": 6 * mm});
            skCircle(sketch, "E2.34.35.0", {"center": v(280.68, -463.4) * mm, "radius": 6 * mm});
            skCircle(sketch, "E2.34.36.0", {"center": v(280.68, -483.4) * mm, "radius": 6 * mm});
            skCircle(sketch, "E2.34.37.0", {"center": v(280.68, -503.4) * mm, "radius": 6 * mm});
            skCircle(sketch, "E2.34.38.0", {"center": v(280.68, -523.4) * mm, "radius": 6 * mm});
            skCircle(sketch, "E2.34.39.0", {"center": v(280.68, -543.4) * mm, "radius": 6 * mm});
            skCircle(sketch, "E2.34.40.0", {"center": v(280.68, -563.4) * mm, "radius": 6 * mm});
            skCircle(sketch, "E2.34.41.0", {"center": v(280.68, -583.4) * mm, "radius": 6 * mm});
            skCircle(sketch, "E2.34.42.0", {"center": v(280.68, -603.4) * mm, "radius": 6 * mm});
            skCircle(sketch, "E2.34.43.0", {"center": v(280.68, -623.4) * mm, "radius": 6 * mm});
            skCircle(sketch, "E2.34.44.0", {"center": v(280.68, -643.4) * mm, "radius": 6 * mm});
            skCircle(sketch, "E2.34.45.0", {"center": v(280.68, -663.4) * mm, "radius": 6 * mm});
            skCircle(sketch, "E2.34.46.0", {"center": v(280.68, -683.4) * mm, "radius": 6 * mm});
            skCircle(sketch, "E2.34.47.0", {"center": v(280.68, -703.4) * mm, "radius": 6 * mm});
            skCircle(sketch, "E2.34.48.0", {"center": v(280.68, -723.4) * mm, "radius": 6 * mm});
            skCircle(sketch, "E2.34.49.0", {"center": v(280.68, -743.4) * mm, "radius": 6 * mm});
            skCircle(sketch, "E2.35.0.0", {"center": v(300.68, 236.6) * mm, "radius": 6 * mm});
            skCircle(sketch, "E2.35.1.0", {"center": v(300.68, 216.6) * mm, "radius": 6 * mm});
            skCircle(sketch, "E2.35.2.0", {"center": v(300.68, 196.6) * mm, "radius": 6 * mm});
            skCircle(sketch, "E2.35.3.0", {"center": v(300.68, 176.6) * mm, "radius": 6 * mm});
            skCircle(sketch, "E2.35.4.0", {"center": v(300.68, 156.6) * mm, "radius": 6 * mm});
            skCircle(sketch, "E2.35.5.0", {"center": v(300.68, 136.6) * mm, "radius": 6 * mm});
            skCircle(sketch, "E2.35.6.0", {"center": v(300.68, 116.6) * mm, "radius": 6 * mm});
            skCircle(sketch, "E2.35.7.0", {"center": v(300.68, 96.6) * mm, "radius": 6 * mm});
            skCircle(sketch, "E2.35.8.0", {"center": v(300.68, 76.6) * mm, "radius": 6 * mm});
            skCircle(sketch, "E2.35.9.0", {"center": v(300.68, 56.6) * mm, "radius": 6 * mm});
            skCircle(sketch, "E2.35.10.0", {"center": v(300.68, 36.6) * mm, "radius": 6 * mm});
            skCircle(sketch, "E2.35.11.0", {"center": v(300.68, 16.6) * mm, "radius": 6 * mm});
            skCircle(sketch, "E2.35.12.0", {"center": v(300.68, -3.4) * mm, "radius": 6 * mm});
            skCircle(sketch, "E2.35.13.0", {"center": v(300.68, -23.4) * mm, "radius": 6 * mm});
            skCircle(sketch, "E2.35.14.0", {"center": v(300.68, -43.4) * mm, "radius": 6 * mm});
            skCircle(sketch, "E2.35.15.0", {"center": v(300.68, -63.4) * mm, "radius": 6 * mm});
            skCircle(sketch, "E2.35.16.0", {"center": v(300.68, -83.4) * mm, "radius": 6 * mm});
            skCircle(sketch, "E2.35.17.0", {"center": v(300.68, -103.4) * mm, "radius": 6 * mm});
            skCircle(sketch, "E2.35.18.0", {"center": v(300.68, -123.4) * mm, "radius": 6 * mm});
            skCircle(sketch, "E2.35.19.0", {"center": v(300.68, -143.4) * mm, "radius": 6 * mm});
            skCircle(sketch, "E2.35.20.0", {"center": v(300.68, -163.4) * mm, "radius": 6 * mm});
            skCircle(sketch, "E2.35.21.0", {"center": v(300.68, -183.4) * mm, "radius": 6 * mm});
            skCircle(sketch, "E2.35.22.0", {"center": v(300.68, -203.4) * mm, "radius": 6 * mm});
            skCircle(sketch, "E2.35.23.0", {"center": v(300.68, -223.4) * mm, "radius": 6 * mm});
            skCircle(sketch, "E2.35.24.0", {"center": v(300.68, -243.4) * mm, "radius": 6 * mm});
            skCircle(sketch, "E2.35.25.0", {"center": v(300.68, -263.4) * mm, "radius": 6 * mm});
            skCircle(sketch, "E2.35.26.0", {"center": v(300.68, -283.4) * mm, "radius": 6 * mm});
            skCircle(sketch, "E2.35.27.0", {"center": v(300.68, -303.4) * mm, "radius": 6 * mm});
            skCircle(sketch, "E2.35.28.0", {"center": v(300.68, -323.4) * mm, "radius": 6 * mm});
            skCircle(sketch, "E2.35.29.0", {"center": v(300.68, -343.4) * mm, "radius": 6 * mm});
            skCircle(sketch, "E2.35.30.0", {"center": v(300.68, -363.4) * mm, "radius": 6 * mm});
            skCircle(sketch, "E2.35.31.0", {"center": v(300.68, -383.4) * mm, "radius": 6 * mm});
            skCircle(sketch, "E2.35.32.0", {"center": v(300.68, -403.4) * mm, "radius": 6 * mm});
            skCircle(sketch, "E2.35.33.0", {"center": v(300.68, -423.4) * mm, "radius": 6 * mm});
            skCircle(sketch, "E2.35.34.0", {"center": v(300.68, -443.4) * mm, "radius": 6 * mm});
            skCircle(sketch, "E2.35.35.0", {"center": v(300.68, -463.4) * mm, "radius": 6 * mm});
            skCircle(sketch, "E2.35.36.0", {"center": v(300.68, -483.4) * mm, "radius": 6 * mm});
            skCircle(sketch, "E2.35.37.0", {"center": v(300.68, -503.4) * mm, "radius": 6 * mm});
            skCircle(sketch, "E2.35.38.0", {"center": v(300.68, -523.4) * mm, "radius": 6 * mm});
            skCircle(sketch, "E2.35.39.0", {"center": v(300.68, -543.4) * mm, "radius": 6 * mm});
            skCircle(sketch, "E2.35.40.0", {"center": v(300.68, -563.4) * mm, "radius": 6 * mm});
            skCircle(sketch, "E2.35.41.0", {"center": v(300.68, -583.4) * mm, "radius": 6 * mm});
            skCircle(sketch, "E2.35.42.0", {"center": v(300.68, -603.4) * mm, "radius": 6 * mm});
            skCircle(sketch, "E2.35.43.0", {"center": v(300.68, -623.4) * mm, "radius": 6 * mm});
            skCircle(sketch, "E2.35.44.0", {"center": v(300.68, -643.4) * mm, "radius": 6 * mm});
            skCircle(sketch, "E2.35.45.0", {"center": v(300.68, -663.4) * mm, "radius": 6 * mm});
            skCircle(sketch, "E2.35.46.0", {"center": v(300.68, -683.4) * mm, "radius": 6 * mm});
            skCircle(sketch, "E2.35.47.0", {"center": v(300.68, -703.4) * mm, "radius": 6 * mm});
            skCircle(sketch, "E2.35.48.0", {"center": v(300.68, -723.4) * mm, "radius": 6 * mm});
            skCircle(sketch, "E2.35.49.0", {"center": v(300.68, -743.4) * mm, "radius": 6 * mm});
            skCircle(sketch, "E2.36.0.0", {"center": v(320.68, 236.6) * mm, "radius": 6 * mm});
            skCircle(sketch, "E2.36.1.0", {"center": v(320.68, 216.6) * mm, "radius": 6 * mm});
            skCircle(sketch, "E2.36.2.0", {"center": v(320.68, 196.6) * mm, "radius": 6 * mm});
            skCircle(sketch, "E2.36.3.0", {"center": v(320.68, 176.6) * mm, "radius": 6 * mm});
            skCircle(sketch, "E2.36.4.0", {"center": v(320.68, 156.6) * mm, "radius": 6 * mm});
            skCircle(sketch, "E2.36.5.0", {"center": v(320.68, 136.6) * mm, "radius": 6 * mm});
            skCircle(sketch, "E2.36.6.0", {"center": v(320.68, 116.6) * mm, "radius": 6 * mm});
            skCircle(sketch, "E2.36.7.0", {"center": v(320.68, 96.6) * mm, "radius": 6 * mm});
            skCircle(sketch, "E2.36.8.0", {"center": v(320.68, 76.6) * mm, "radius": 6 * mm});
            skCircle(sketch, "E2.36.9.0", {"center": v(320.68, 56.6) * mm, "radius": 6 * mm});
            skCircle(sketch, "E2.36.10.0", {"center": v(320.68, 36.6) * mm, "radius": 6 * mm});
            skCircle(sketch, "E2.36.11.0", {"center": v(320.68, 16.6) * mm, "radius": 6 * mm});
            skCircle(sketch, "E2.36.12.0", {"center": v(320.68, -3.4) * mm, "radius": 6 * mm});
            skCircle(sketch, "E2.36.13.0", {"center": v(320.68, -23.4) * mm, "radius": 6 * mm});
            skCircle(sketch, "E2.36.14.0", {"center": v(320.68, -43.4) * mm, "radius": 6 * mm});
            skCircle(sketch, "E2.36.15.0", {"center": v(320.68, -63.4) * mm, "radius": 6 * mm});
            skCircle(sketch, "E2.36.16.0", {"center": v(320.68, -83.4) * mm, "radius": 6 * mm});
            skCircle(sketch, "E2.36.17.0", {"center": v(320.68, -103.4) * mm, "radius": 6 * mm});
            skCircle(sketch, "E2.36.18.0", {"center": v(320.68, -123.4) * mm, "radius": 6 * mm});
            skCircle(sketch, "E2.36.19.0", {"center": v(320.68, -143.4) * mm, "radius": 6 * mm});
            skCircle(sketch, "E2.36.20.0", {"center": v(320.68, -163.4) * mm, "radius": 6 * mm});
            skCircle(sketch, "E2.36.21.0", {"center": v(320.68, -183.4) * mm, "radius": 6 * mm});
            skCircle(sketch, "E2.36.22.0", {"center": v(320.68, -203.4) * mm, "radius": 6 * mm});
            skCircle(sketch, "E2.36.23.0", {"center": v(320.68, -223.4) * mm, "radius": 6 * mm});
            skCircle(sketch, "E2.36.24.0", {"center": v(320.68, -243.4) * mm, "radius": 6 * mm});
            skCircle(sketch, "E2.36.25.0", {"center": v(320.68, -263.4) * mm, "radius": 6 * mm});
            skCircle(sketch, "E2.36.26.0", {"center": v(320.68, -283.4) * mm, "radius": 6 * mm});
            skCircle(sketch, "E2.36.27.0", {"center": v(320.68, -303.4) * mm, "radius": 6 * mm});
            skCircle(sketch, "E2.36.28.0", {"center": v(320.68, -323.4) * mm, "radius": 6 * mm});
            skCircle(sketch, "E2.36.29.0", {"center": v(320.68, -343.4) * mm, "radius": 6 * mm});
            skCircle(sketch, "E2.36.30.0", {"center": v(320.68, -363.4) * mm, "radius": 6 * mm});
            skCircle(sketch, "E2.36.31.0", {"center": v(320.68, -383.4) * mm, "radius": 6 * mm});
            skCircle(sketch, "E2.36.32.0", {"center": v(320.68, -403.4) * mm, "radius": 6 * mm});
            skCircle(sketch, "E2.36.33.0", {"center": v(320.68, -423.4) * mm, "radius": 6 * mm});
            skCircle(sketch, "E2.36.34.0", {"center": v(320.68, -443.4) * mm, "radius": 6 * mm});
            skCircle(sketch, "E2.36.35.0", {"center": v(320.68, -463.4) * mm, "radius": 6 * mm});
            skCircle(sketch, "E2.36.36.0", {"center": v(320.68, -483.4) * mm, "radius": 6 * mm});
            skCircle(sketch, "E2.36.37.0", {"center": v(320.68, -503.4) * mm, "radius": 6 * mm});
            skCircle(sketch, "E2.36.38.0", {"center": v(320.68, -523.4) * mm, "radius": 6 * mm});
            skCircle(sketch, "E2.36.39.0", {"center": v(320.68, -543.4) * mm, "radius": 6 * mm});
            skCircle(sketch, "E2.36.40.0", {"center": v(320.68, -563.4) * mm, "radius": 6 * mm});
            skCircle(sketch, "E2.36.41.0", {"center": v(320.68, -583.4) * mm, "radius": 6 * mm});
            skCircle(sketch, "E2.36.42.0", {"center": v(320.68, -603.4) * mm, "radius": 6 * mm});
            skCircle(sketch, "E2.36.43.0", {"center": v(320.68, -623.4) * mm, "radius": 6 * mm});
            skCircle(sketch, "E2.36.44.0", {"center": v(320.68, -643.4) * mm, "radius": 6 * mm});
            skCircle(sketch, "E2.36.45.0", {"center": v(320.68, -663.4) * mm, "radius": 6 * mm});
            skCircle(sketch, "E2.36.46.0", {"center": v(320.68, -683.4) * mm, "radius": 6 * mm});
            skCircle(sketch, "E2.36.47.0", {"center": v(320.68, -703.4) * mm, "radius": 6 * mm});
            skCircle(sketch, "E2.36.48.0", {"center": v(320.68, -723.4) * mm, "radius": 6 * mm});
            skCircle(sketch, "E2.36.49.0", {"center": v(320.68, -743.4) * mm, "radius": 6 * mm});
            skCircle(sketch, "E2.37.0.0", {"center": v(340.68, 236.6) * mm, "radius": 6 * mm});
            skCircle(sketch, "E2.37.1.0", {"center": v(340.68, 216.6) * mm, "radius": 6 * mm});
            skCircle(sketch, "E2.37.2.0", {"center": v(340.68, 196.6) * mm, "radius": 6 * mm});
            skCircle(sketch, "E2.37.3.0", {"center": v(340.68, 176.6) * mm, "radius": 6 * mm});
            skCircle(sketch, "E2.37.4.0", {"center": v(340.68, 156.6) * mm, "radius": 6 * mm});
            skCircle(sketch, "E2.37.5.0", {"center": v(340.68, 136.6) * mm, "radius": 6 * mm});
            skCircle(sketch, "E2.37.6.0", {"center": v(340.68, 116.6) * mm, "radius": 6 * mm});
            skCircle(sketch, "E2.37.7.0", {"center": v(340.68, 96.6) * mm, "radius": 6 * mm});
            skCircle(sketch, "E2.37.8.0", {"center": v(340.68, 76.6) * mm, "radius": 6 * mm});
            skCircle(sketch, "E2.37.9.0", {"center": v(340.68, 56.6) * mm, "radius": 6 * mm});
            skCircle(sketch, "E2.37.10.0", {"center": v(340.68, 36.6) * mm, "radius": 6 * mm});
            skCircle(sketch, "E2.37.11.0", {"center": v(340.68, 16.6) * mm, "radius": 6 * mm});
            skCircle(sketch, "E2.37.12.0", {"center": v(340.68, -3.4) * mm, "radius": 6 * mm});
            skCircle(sketch, "E2.37.13.0", {"center": v(340.68, -23.4) * mm, "radius": 6 * mm});
            skCircle(sketch, "E2.37.14.0", {"center": v(340.68, -43.4) * mm, "radius": 6 * mm});
            skCircle(sketch, "E2.37.15.0", {"center": v(340.68, -63.4) * mm, "radius": 6 * mm});
            skCircle(sketch, "E2.37.16.0", {"center": v(340.68, -83.4) * mm, "radius": 6 * mm});
            skCircle(sketch, "E2.37.17.0", {"center": v(340.68, -103.4) * mm, "radius": 6 * mm});
            skCircle(sketch, "E2.37.18.0", {"center": v(340.68, -123.4) * mm, "radius": 6 * mm});
            skCircle(sketch, "E2.37.19.0", {"center": v(340.68, -143.4) * mm, "radius": 6 * mm});
            skCircle(sketch, "E2.37.20.0", {"center": v(340.68, -163.4) * mm, "radius": 6 * mm});
            skCircle(sketch, "E2.37.21.0", {"center": v(340.68, -183.4) * mm, "radius": 6 * mm});
            skCircle(sketch, "E2.37.22.0", {"center": v(340.68, -203.4) * mm, "radius": 6 * mm});
            skCircle(sketch, "E2.37.23.0", {"center": v(340.68, -223.4) * mm, "radius": 6 * mm});
            skCircle(sketch, "E2.37.24.0", {"center": v(340.68, -243.4) * mm, "radius": 6 * mm});
            skCircle(sketch, "E2.37.25.0", {"center": v(340.68, -263.4) * mm, "radius": 6 * mm});
            skCircle(sketch, "E2.37.26.0", {"center": v(340.68, -283.4) * mm, "radius": 6 * mm});
            skCircle(sketch, "E2.37.27.0", {"center": v(340.68, -303.4) * mm, "radius": 6 * mm});
            skCircle(sketch, "E2.37.28.0", {"center": v(340.68, -323.4) * mm, "radius": 6 * mm});
            skCircle(sketch, "E2.37.29.0", {"center": v(340.68, -343.4) * mm, "radius": 6 * mm});
            skCircle(sketch, "E2.37.30.0", {"center": v(340.68, -363.4) * mm, "radius": 6 * mm});
            skCircle(sketch, "E2.37.31.0", {"center": v(340.68, -383.4) * mm, "radius": 6 * mm});
            skCircle(sketch, "E2.37.32.0", {"center": v(340.68, -403.4) * mm, "radius": 6 * mm});
            skCircle(sketch, "E2.37.33.0", {"center": v(340.68, -423.4) * mm, "radius": 6 * mm});
            skCircle(sketch, "E2.37.34.0", {"center": v(340.68, -443.4) * mm, "radius": 6 * mm});
            skCircle(sketch, "E2.37.35.0", {"center": v(340.68, -463.4) * mm, "radius": 6 * mm});
            skCircle(sketch, "E2.37.36.0", {"center": v(340.68, -483.4) * mm, "radius": 6 * mm});
            skCircle(sketch, "E2.37.37.0", {"center": v(340.68, -503.4) * mm, "radius": 6 * mm});
            skCircle(sketch, "E2.37.38.0", {"center": v(340.68, -523.4) * mm, "radius": 6 * mm});
            skCircle(sketch, "E2.37.39.0", {"center": v(340.68, -543.4) * mm, "radius": 6 * mm});
            skCircle(sketch, "E2.37.40.0", {"center": v(340.68, -563.4) * mm, "radius": 6 * mm});
            skCircle(sketch, "E2.37.41.0", {"center": v(340.68, -583.4) * mm, "radius": 6 * mm});
            skCircle(sketch, "E2.37.42.0", {"center": v(340.68, -603.4) * mm, "radius": 6 * mm});
            skCircle(sketch, "E2.37.43.0", {"center": v(340.68, -623.4) * mm, "radius": 6 * mm});
            skCircle(sketch, "E2.37.44.0", {"center": v(340.68, -643.4) * mm, "radius": 6 * mm});
            skCircle(sketch, "E2.37.45.0", {"center": v(340.68, -663.4) * mm, "radius": 6 * mm});
            skCircle(sketch, "E2.37.46.0", {"center": v(340.68, -683.4) * mm, "radius": 6 * mm});
            skCircle(sketch, "E2.37.47.0", {"center": v(340.68, -703.4) * mm, "radius": 6 * mm});
            skCircle(sketch, "E2.37.48.0", {"center": v(340.68, -723.4) * mm, "radius": 6 * mm});
            skCircle(sketch, "E2.37.49.0", {"center": v(340.68, -743.4) * mm, "radius": 6 * mm});
            skCircle(sketch, "E2.38.0.0", {"center": v(360.68, 236.6) * mm, "radius": 6 * mm});
            skCircle(sketch, "E2.38.1.0", {"center": v(360.68, 216.6) * mm, "radius": 6 * mm});
            skCircle(sketch, "E2.38.2.0", {"center": v(360.68, 196.6) * mm, "radius": 6 * mm});
            skCircle(sketch, "E2.38.3.0", {"center": v(360.68, 176.6) * mm, "radius": 6 * mm});
            skCircle(sketch, "E2.38.4.0", {"center": v(360.68, 156.6) * mm, "radius": 6 * mm});
            skCircle(sketch, "E2.38.5.0", {"center": v(360.68, 136.6) * mm, "radius": 6 * mm});
            skCircle(sketch, "E2.38.6.0", {"center": v(360.68, 116.6) * mm, "radius": 6 * mm});
            skCircle(sketch, "E2.38.7.0", {"center": v(360.68, 96.6) * mm, "radius": 6 * mm});
            skCircle(sketch, "E2.38.8.0", {"center": v(360.68, 76.6) * mm, "radius": 6 * mm});
            skCircle(sketch, "E2.38.9.0", {"center": v(360.68, 56.6) * mm, "radius": 6 * mm});
            skCircle(sketch, "E2.38.10.0", {"center": v(360.68, 36.6) * mm, "radius": 6 * mm});
            skCircle(sketch, "E2.38.11.0", {"center": v(360.68, 16.6) * mm, "radius": 6 * mm});
            skCircle(sketch, "E2.38.12.0", {"center": v(360.68, -3.4) * mm, "radius": 6 * mm});
            skCircle(sketch, "E2.38.13.0", {"center": v(360.68, -23.4) * mm, "radius": 6 * mm});
            skCircle(sketch, "E2.38.14.0", {"center": v(360.68, -43.4) * mm, "radius": 6 * mm});
            skCircle(sketch, "E2.38.15.0", {"center": v(360.68, -63.4) * mm, "radius": 6 * mm});
            skCircle(sketch, "E2.38.16.0", {"center": v(360.68, -83.4) * mm, "radius": 6 * mm});
            skCircle(sketch, "E2.38.17.0", {"center": v(360.68, -103.4) * mm, "radius": 6 * mm});
            skCircle(sketch, "E2.38.18.0", {"center": v(360.68, -123.4) * mm, "radius": 6 * mm});
            skCircle(sketch, "E2.38.19.0", {"center": v(360.68, -143.4) * mm, "radius": 6 * mm});
            skCircle(sketch, "E2.38.20.0", {"center": v(360.68, -163.4) * mm, "radius": 6 * mm});
            skCircle(sketch, "E2.38.21.0", {"center": v(360.68, -183.4) * mm, "radius": 6 * mm});
            skCircle(sketch, "E2.38.22.0", {"center": v(360.68, -203.4) * mm, "radius": 6 * mm});
            skCircle(sketch, "E2.38.23.0", {"center": v(360.68, -223.4) * mm, "radius": 6 * mm});
            skCircle(sketch, "E2.38.24.0", {"center": v(360.68, -243.4) * mm, "radius": 6 * mm});
            skCircle(sketch, "E2.38.25.0", {"center": v(360.68, -263.4) * mm, "radius": 6 * mm});
            skCircle(sketch, "E2.38.26.0", {"center": v(360.68, -283.4) * mm, "radius": 6 * mm});
            skCircle(sketch, "E2.38.27.0", {"center": v(360.68, -303.4) * mm, "radius": 6 * mm});
            skCircle(sketch, "E2.38.28.0", {"center": v(360.68, -323.4) * mm, "radius": 6 * mm});
            skCircle(sketch, "E2.38.29.0", {"center": v(360.68, -343.4) * mm, "radius": 6 * mm});
            skCircle(sketch, "E2.38.30.0", {"center": v(360.68, -363.4) * mm, "radius": 6 * mm});
            skCircle(sketch, "E2.38.31.0", {"center": v(360.68, -383.4) * mm, "radius": 6 * mm});
            skCircle(sketch, "E2.38.32.0", {"center": v(360.68, -403.4) * mm, "radius": 6 * mm});
            skCircle(sketch, "E2.38.33.0", {"center": v(360.68, -423.4) * mm, "radius": 6 * mm});
            skCircle(sketch, "E2.38.34.0", {"center": v(360.68, -443.4) * mm, "radius": 6 * mm});
            skCircle(sketch, "E2.38.35.0", {"center": v(360.68, -463.4) * mm, "radius": 6 * mm});
            skCircle(sketch, "E2.38.36.0", {"center": v(360.68, -483.4) * mm, "radius": 6 * mm});
            skCircle(sketch, "E2.38.37.0", {"center": v(360.68, -503.4) * mm, "radius": 6 * mm});
            skCircle(sketch, "E2.38.38.0", {"center": v(360.68, -523.4) * mm, "radius": 6 * mm});
            skCircle(sketch, "E2.38.39.0", {"center": v(360.68, -543.4) * mm, "radius": 6 * mm});
            skCircle(sketch, "E2.38.40.0", {"center": v(360.68, -563.4) * mm, "radius": 6 * mm});
            skCircle(sketch, "E2.38.41.0", {"center": v(360.68, -583.4) * mm, "radius": 6 * mm});
            skCircle(sketch, "E2.38.42.0", {"center": v(360.68, -603.4) * mm, "radius": 6 * mm});
            skCircle(sketch, "E2.38.43.0", {"center": v(360.68, -623.4) * mm, "radius": 6 * mm});
            skCircle(sketch, "E2.38.44.0", {"center": v(360.68, -643.4) * mm, "radius": 6 * mm});
            skCircle(sketch, "E2.38.45.0", {"center": v(360.68, -663.4) * mm, "radius": 6 * mm});
            skCircle(sketch, "E2.38.46.0", {"center": v(360.68, -683.4) * mm, "radius": 6 * mm});
            skCircle(sketch, "E2.38.47.0", {"center": v(360.68, -703.4) * mm, "radius": 6 * mm});
            skCircle(sketch, "E2.38.48.0", {"center": v(360.68, -723.4) * mm, "radius": 6 * mm});
            skCircle(sketch, "E2.38.49.0", {"center": v(360.68, -743.4) * mm, "radius": 6 * mm});
            skCircle(sketch, "E2.39.0.0", {"center": v(380.68, 236.6) * mm, "radius": 6 * mm});
            skCircle(sketch, "E2.39.1.0", {"center": v(380.68, 216.6) * mm, "radius": 6 * mm});
            skCircle(sketch, "E2.39.2.0", {"center": v(380.68, 196.6) * mm, "radius": 6 * mm});
            skCircle(sketch, "E2.39.3.0", {"center": v(380.68, 176.6) * mm, "radius": 6 * mm});
            skCircle(sketch, "E2.39.4.0", {"center": v(380.68, 156.6) * mm, "radius": 6 * mm});
            skCircle(sketch, "E2.39.5.0", {"center": v(380.68, 136.6) * mm, "radius": 6 * mm});
            skCircle(sketch, "E2.39.6.0", {"center": v(380.68, 116.6) * mm, "radius": 6 * mm});
            skCircle(sketch, "E2.39.7.0", {"center": v(380.68, 96.6) * mm, "radius": 6 * mm});
            skCircle(sketch, "E2.39.8.0", {"center": v(380.68, 76.6) * mm, "radius": 6 * mm});
            skCircle(sketch, "E2.39.9.0", {"center": v(380.68, 56.6) * mm, "radius": 6 * mm});
            skCircle(sketch, "E2.39.10.0", {"center": v(380.68, 36.6) * mm, "radius": 6 * mm});
            skCircle(sketch, "E2.39.11.0", {"center": v(380.68, 16.6) * mm, "radius": 6 * mm});
            skCircle(sketch, "E2.39.12.0", {"center": v(380.68, -3.4) * mm, "radius": 6 * mm});
            skCircle(sketch, "E2.39.13.0", {"center": v(380.68, -23.4) * mm, "radius": 6 * mm});
            skCircle(sketch, "E2.39.14.0", {"center": v(380.68, -43.4) * mm, "radius": 6 * mm});
            skCircle(sketch, "E2.39.15.0", {"center": v(380.68, -63.4) * mm, "radius": 6 * mm});
            skCircle(sketch, "E2.39.16.0", {"center": v(380.68, -83.4) * mm, "radius": 6 * mm});
            skCircle(sketch, "E2.39.17.0", {"center": v(380.68, -103.4) * mm, "radius": 6 * mm});
            skCircle(sketch, "E2.39.18.0", {"center": v(380.68, -123.4) * mm, "radius": 6 * mm});
            skCircle(sketch, "E2.39.19.0", {"center": v(380.68, -143.4) * mm, "radius": 6 * mm});
            skCircle(sketch, "E2.39.20.0", {"center": v(380.68, -163.4) * mm, "radius": 6 * mm});
            skCircle(sketch, "E2.39.21.0", {"center": v(380.68, -183.4) * mm, "radius": 6 * mm});
            skCircle(sketch, "E2.39.22.0", {"center": v(380.68, -203.4) * mm, "radius": 6 * mm});
            skCircle(sketch, "E2.39.23.0", {"center": v(380.68, -223.4) * mm, "radius": 6 * mm});
            skCircle(sketch, "E2.39.24.0", {"center": v(380.68, -243.4) * mm, "radius": 6 * mm});
            skCircle(sketch, "E2.39.25.0", {"center": v(380.68, -263.4) * mm, "radius": 6 * mm});
            skCircle(sketch, "E2.39.26.0", {"center": v(380.68, -283.4) * mm, "radius": 6 * mm});
            skCircle(sketch, "E2.39.27.0", {"center": v(380.68, -303.4) * mm, "radius": 6 * mm});
            skCircle(sketch, "E2.39.28.0", {"center": v(380.68, -323.4) * mm, "radius": 6 * mm});
            skCircle(sketch, "E2.39.29.0", {"center": v(380.68, -343.4) * mm, "radius": 6 * mm});
            skCircle(sketch, "E2.39.30.0", {"center": v(380.68, -363.4) * mm, "radius": 6 * mm});
            skCircle(sketch, "E2.39.31.0", {"center": v(380.68, -383.4) * mm, "radius": 6 * mm});
            skCircle(sketch, "E2.39.32.0", {"center": v(380.68, -403.4) * mm, "radius": 6 * mm});
            skCircle(sketch, "E2.39.33.0", {"center": v(380.68, -423.4) * mm, "radius": 6 * mm});
            skCircle(sketch, "E2.39.34.0", {"center": v(380.68, -443.4) * mm, "radius": 6 * mm});
            skCircle(sketch, "E2.39.35.0", {"center": v(380.68, -463.4) * mm, "radius": 6 * mm});
            skCircle(sketch, "E2.39.36.0", {"center": v(380.68, -483.4) * mm, "radius": 6 * mm});
            skCircle(sketch, "E2.39.37.0", {"center": v(380.68, -503.4) * mm, "radius": 6 * mm});
            skCircle(sketch, "E2.39.38.0", {"center": v(380.68, -523.4) * mm, "radius": 6 * mm});
            skCircle(sketch, "E2.39.39.0", {"center": v(380.68, -543.4) * mm, "radius": 6 * mm});
            skCircle(sketch, "E2.39.40.0", {"center": v(380.68, -563.4) * mm, "radius": 6 * mm});
            skCircle(sketch, "E2.39.41.0", {"center": v(380.68, -583.4) * mm, "radius": 6 * mm});
            skCircle(sketch, "E2.39.42.0", {"center": v(380.68, -603.4) * mm, "radius": 6 * mm});
            skCircle(sketch, "E2.39.43.0", {"center": v(380.68, -623.4) * mm, "radius": 6 * mm});
            skCircle(sketch, "E2.39.44.0", {"center": v(380.68, -643.4) * mm, "radius": 6 * mm});
            skCircle(sketch, "E2.39.45.0", {"center": v(380.68, -663.4) * mm, "radius": 6 * mm});
            skCircle(sketch, "E2.39.46.0", {"center": v(380.68, -683.4) * mm, "radius": 6 * mm});
            skCircle(sketch, "E2.39.47.0", {"center": v(380.68, -703.4) * mm, "radius": 6 * mm});
            skCircle(sketch, "E2.39.48.0", {"center": v(380.68, -723.4) * mm, "radius": 6 * mm});
            skCircle(sketch, "E2.39.49.0", {"center": v(380.68, -743.4) * mm, "radius": 6 * mm});
            skLineSegment(sketch, "E2.direction1", {"start": v(-399.32, 236.6) * mm, "end": v(-379.32, 236.6) * mm, "construction": true});
            skLineSegment(sketch, "E2.direction2", {"start": v(-399.32, 236.6) * mm, "end": v(-399.32, 216.6) * mm, "construction": true});
            skSolve(sketch);
        }
        {
            var Q0;
            Q0 = qSketchRegion(id + "F2", true);
            extrude(context, id + "F3", {"entities" : qUnion([Q0]), "operationType" : NewBodyOperationType.REMOVE, "oppositeDirection" : true, "depth" : 25 * mm, "offsetDistance" : 25 * mm});
        }
    });
